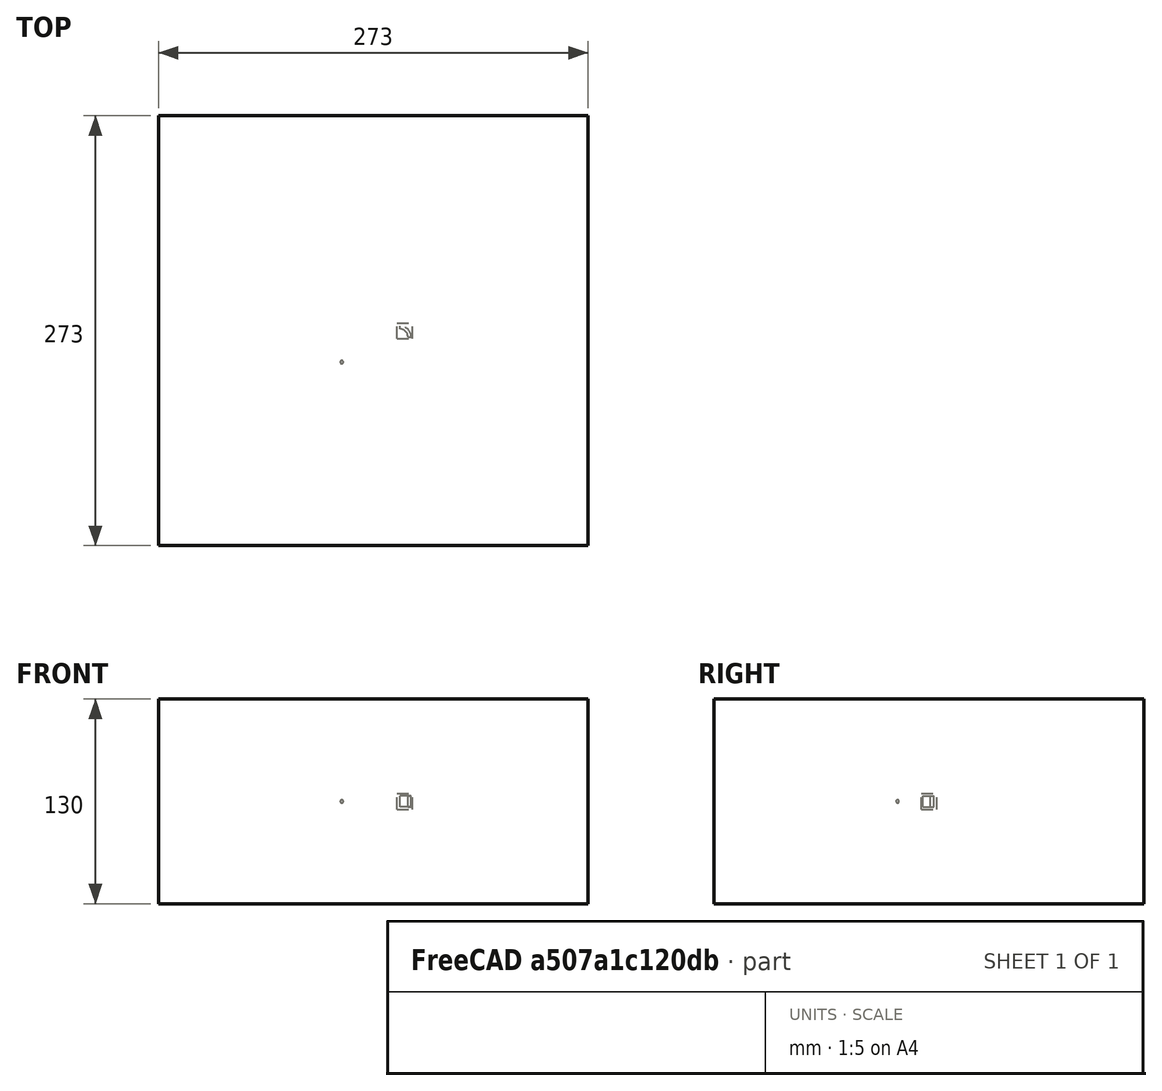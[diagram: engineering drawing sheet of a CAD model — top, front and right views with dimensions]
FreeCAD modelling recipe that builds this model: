
FCSTD DOCUMENT  (FreeCAD 0.21R33694 (Git))
Label: polarArray-of-Part-array-xformed
License: All rights reserved
LicenseURL: http://en.wikipedia.org/wiki/All_rights_reserved
objects: App::DocumentObjectGroupPython×1251, App::Part×5, Part::FeaturePython×4, Part::Sphere×1
note: 4 computed .brp shape members not serialized (recipe doc carries the construction recipe); baked Part::Feature solids carry a one-line shape summary decoded from their .brp

FEATURE [App::DocumentObjectGroupPython] HALFPI  # scripted group (container) (typed FeaturePython)
  name = HALFPI
  value = pi/2.
FEATURE [App::DocumentObjectGroupPython] PI  # scripted group (container) (typed FeaturePython)
  name = PI
  value = 1.*pi
FEATURE [App::DocumentObjectGroupPython] TWOPI  # scripted group (container) (typed FeaturePython)
  name = TWOPI
  value = 2.*pi
FEATURE [App::DocumentObjectGroupPython] Constants  # scripted group (container) (typed FeaturePython)
  Group = -> [HALFPI,PI,TWOPI]
FEATURE [App::DocumentObjectGroupPython] Variables  # scripted group (container) (typed FeaturePython)
FEATURE [App::DocumentObjectGroupPython] Quantities  # scripted group (container) (typed FeaturePython)
FEATURE [App::DocumentObjectGroupPython] Isotopes  # scripted group (container) (typed FeaturePython)
FEATURE [App::DocumentObjectGroupPython] Elements  # scripted group (container) (typed FeaturePython)
FEATURE [App::DocumentObjectGroupPython] Matrix  # scripted group (container) (typed FeaturePython)
FEATURE [App::DocumentObjectGroupPython] Surfaces  # scripted group (container) (typed FeaturePython)
FEATURE [App::DocumentObjectGroupPython] Opticals  # scripted group (container) (typed FeaturePython)
  Group = -> [Matrix,Surfaces]
FEATURE [App::DocumentObjectGroupPython] G4Isotopes  # scripted group (container) (typed FeaturePython)
FEATURE [App::DocumentObjectGroupPython] H_element  # scripted group (container) (typed FeaturePython)
  Z = 1
  atom_value = 1.008
  formula = H
  name = H_element
FEATURE [App::DocumentObjectGroupPython] He_element  # scripted group (container) (typed FeaturePython)
  Z = 2
  atom_value = 4.0026
  formula = He
  name = He_element
FEATURE [App::DocumentObjectGroupPython] Li_element  # scripted group (container) (typed FeaturePython)
  Z = 3
  atom_value = 6.94
  formula = Li
  name = Li_element
FEATURE [App::DocumentObjectGroupPython] Be_element  # scripted group (container) (typed FeaturePython)
  Z = 4
  atom_value = 9.01218
  formula = Be
  name = Be_element
FEATURE [App::DocumentObjectGroupPython] B_element  # scripted group (container) (typed FeaturePython)
  Z = 5
  atom_value = 10.81
  formula = B
  name = B_element
FEATURE [App::DocumentObjectGroupPython] C_element  # scripted group (container) (typed FeaturePython)
  Z = 6
  atom_value = 12.011
  formula = C
  name = C_element
FEATURE [App::DocumentObjectGroupPython] N_element  # scripted group (container) (typed FeaturePython)
  Z = 7
  atom_value = 14.007
  formula = N
  name = N_element
FEATURE [App::DocumentObjectGroupPython] O_element  # scripted group (container) (typed FeaturePython)
  Z = 8
  atom_value = 15.999
  formula = O
  name = O_element
FEATURE [App::DocumentObjectGroupPython] F_element  # scripted group (container) (typed FeaturePython)
  Z = 9
  atom_value = 18.9984
  formula = F
  name = F_element
FEATURE [App::DocumentObjectGroupPython] Ne_element  # scripted group (container) (typed FeaturePython)
  Z = 10
  atom_value = 20.1797
  formula = Ne
  name = Ne_element
FEATURE [App::DocumentObjectGroupPython] Na_element  # scripted group (container) (typed FeaturePython)
  Z = 11
  atom_value = 22.9898
  formula = Na
  name = Na_element
FEATURE [App::DocumentObjectGroupPython] Mg_element  # scripted group (container) (typed FeaturePython)
  Z = 12
  atom_value = 24.305
  formula = Mg
  name = Mg_element
FEATURE [App::DocumentObjectGroupPython] Al_element  # scripted group (container) (typed FeaturePython)
  Z = 13
  atom_value = 26.9815
  formula = Al
  name = Al_element
FEATURE [App::DocumentObjectGroupPython] Si_element  # scripted group (container) (typed FeaturePython)
  Z = 14
  atom_value = 28.085
  formula = Si
  name = Si_element
FEATURE [App::DocumentObjectGroupPython] P_element  # scripted group (container) (typed FeaturePython)
  Z = 15
  atom_value = 30.9738
  formula = P
  name = P_element
FEATURE [App::DocumentObjectGroupPython] S_element  # scripted group (container) (typed FeaturePython)
  Z = 16
  atom_value = 32.06
  formula = S
  name = S_element
FEATURE [App::DocumentObjectGroupPython] Cl_element  # scripted group (container) (typed FeaturePython)
  Z = 17
  atom_value = 35.45
  formula = Cl
  name = Cl_element
FEATURE [App::DocumentObjectGroupPython] Ar_element  # scripted group (container) (typed FeaturePython)
  Z = 18
  atom_value = 39.95
  formula = Ar
  name = Ar_element
FEATURE [App::DocumentObjectGroupPython] K_element  # scripted group (container) (typed FeaturePython)
  Z = 19
  atom_value = 39.0983
  formula = K
  name = K_element
FEATURE [App::DocumentObjectGroupPython] Ca_element  # scripted group (container) (typed FeaturePython)
  Z = 20
  atom_value = 40.078
  formula = Ca
  name = Ca_element
FEATURE [App::DocumentObjectGroupPython] Sc_element  # scripted group (container) (typed FeaturePython)
  Z = 21
  atom_value = 44.9559
  formula = Sc
  name = Sc_element
FEATURE [App::DocumentObjectGroupPython] Ti_element  # scripted group (container) (typed FeaturePython)
  Z = 22
  atom_value = 47.867
  formula = Ti
  name = Ti_element
FEATURE [App::DocumentObjectGroupPython] V_element  # scripted group (container) (typed FeaturePython)
  Z = 23
  atom_value = 50.9415
  formula = V
  name = V_element
FEATURE [App::DocumentObjectGroupPython] Cr_element  # scripted group (container) (typed FeaturePython)
  Z = 24
  atom_value = 51.9961
  formula = Cr
  name = Cr_element
FEATURE [App::DocumentObjectGroupPython] Mn_element  # scripted group (container) (typed FeaturePython)
  Z = 25
  atom_value = 54.938
  formula = Mn
  name = Mn_element
FEATURE [App::DocumentObjectGroupPython] Fe_element  # scripted group (container) (typed FeaturePython)
  Z = 26
  atom_value = 55.845
  formula = Fe
  name = Fe_element
FEATURE [App::DocumentObjectGroupPython] Co_element  # scripted group (container) (typed FeaturePython)
  Z = 27
  atom_value = 58.9332
  formula = Co
  name = Co_element
FEATURE [App::DocumentObjectGroupPython] Ni_element  # scripted group (container) (typed FeaturePython)
  Z = 28
  atom_value = 58.6934
  formula = Ni
  name = Ni_element
FEATURE [App::DocumentObjectGroupPython] Cu_element  # scripted group (container) (typed FeaturePython)
  Z = 29
  atom_value = 63.546
  formula = Cu
  name = Cu_element
FEATURE [App::DocumentObjectGroupPython] Zn_element  # scripted group (container) (typed FeaturePython)
  Z = 30
  atom_value = 65.38
  formula = Zn
  name = Zn_element
FEATURE [App::DocumentObjectGroupPython] Ga_element  # scripted group (container) (typed FeaturePython)
  Z = 31
  atom_value = 69.723
  formula = Ga
  name = Ga_element
FEATURE [App::DocumentObjectGroupPython] Ge_element  # scripted group (container) (typed FeaturePython)
  Z = 32
  atom_value = 72.63
  formula = Ge
  name = Ge_element
FEATURE [App::DocumentObjectGroupPython] As_element  # scripted group (container) (typed FeaturePython)
  Z = 33
  atom_value = 74.9216
  formula = As
  name = As_element
FEATURE [App::DocumentObjectGroupPython] Se_element  # scripted group (container) (typed FeaturePython)
  Z = 34
  atom_value = 78.971
  formula = Se
  name = Se_element
FEATURE [App::DocumentObjectGroupPython] Br_element  # scripted group (container) (typed FeaturePython)
  Z = 35
  atom_value = 79.904
  formula = Br
  name = Br_element
FEATURE [App::DocumentObjectGroupPython] Kr_element  # scripted group (container) (typed FeaturePython)
  Z = 36
  atom_value = 83.798
  formula = Kr
  name = Kr_element
FEATURE [App::DocumentObjectGroupPython] Rb_element  # scripted group (container) (typed FeaturePython)
  Z = 37
  atom_value = 85.4678
  formula = Rb
  name = Rb_element
FEATURE [App::DocumentObjectGroupPython] Sr_element  # scripted group (container) (typed FeaturePython)
  Z = 38
  atom_value = 87.62
  formula = Sr
  name = Sr_element
FEATURE [App::DocumentObjectGroupPython] Y_element  # scripted group (container) (typed FeaturePython)
  Z = 39
  atom_value = 88.9058
  formula = Y
  name = Y_element
FEATURE [App::DocumentObjectGroupPython] Zr_element  # scripted group (container) (typed FeaturePython)
  Z = 40
  atom_value = 91.224
  formula = Zr
  name = Zr_element
FEATURE [App::DocumentObjectGroupPython] Nb_element  # scripted group (container) (typed FeaturePython)
  Z = 41
  atom_value = 92.9064
  formula = Nb
  name = Nb_element
FEATURE [App::DocumentObjectGroupPython] Mo_element  # scripted group (container) (typed FeaturePython)
  Z = 42
  atom_value = 95.95
  formula = Mo
  name = Mo_element
FEATURE [App::DocumentObjectGroupPython] Tc_element  # scripted group (container) (typed FeaturePython)
  Z = 43
  atom_value = 97
  formula = Tc
  name = Tc_element
FEATURE [App::DocumentObjectGroupPython] Ru_element  # scripted group (container) (typed FeaturePython)
  Z = 44
  atom_value = 101.07
  formula = Ru
  name = Ru_element
FEATURE [App::DocumentObjectGroupPython] Rh_element  # scripted group (container) (typed FeaturePython)
  Z = 45
  atom_value = 102.905
  formula = Rh
  name = Rh_element
FEATURE [App::DocumentObjectGroupPython] Pd_element  # scripted group (container) (typed FeaturePython)
  Z = 46
  atom_value = 106.42
  formula = Pd
  name = Pd_element
FEATURE [App::DocumentObjectGroupPython] Ag_element  # scripted group (container) (typed FeaturePython)
  Z = 47
  atom_value = 107.868
  formula = Ag
  name = Ag_element
FEATURE [App::DocumentObjectGroupPython] Cd_element  # scripted group (container) (typed FeaturePython)
  Z = 48
  atom_value = 112.414
  formula = Cd
  name = Cd_element
FEATURE [App::DocumentObjectGroupPython] In_element  # scripted group (container) (typed FeaturePython)
  Z = 49
  atom_value = 114.818
  formula = In
  name = In_element
FEATURE [App::DocumentObjectGroupPython] Sn_element  # scripted group (container) (typed FeaturePython)
  Z = 50
  atom_value = 118.71
  formula = Sn
  name = Sn_element
FEATURE [App::DocumentObjectGroupPython] Sb_element  # scripted group (container) (typed FeaturePython)
  Z = 51
  atom_value = 121.76
  formula = Sb
  name = Sb_element
FEATURE [App::DocumentObjectGroupPython] Te_element  # scripted group (container) (typed FeaturePython)
  Z = 52
  atom_value = 127.6
  formula = Te
  name = Te_element
FEATURE [App::DocumentObjectGroupPython] I_element  # scripted group (container) (typed FeaturePython)
  Z = 53
  atom_value = 126.904
  formula = I
  name = I_element
FEATURE [App::DocumentObjectGroupPython] Xe_element  # scripted group (container) (typed FeaturePython)
  Z = 54
  atom_value = 131.293
  formula = Xe
  name = Xe_element
FEATURE [App::DocumentObjectGroupPython] Cs_element  # scripted group (container) (typed FeaturePython)
  Z = 55
  atom_value = 132.905
  formula = Cs
  name = Cs_element
FEATURE [App::DocumentObjectGroupPython] Ba_element  # scripted group (container) (typed FeaturePython)
  Z = 56
  atom_value = 137.327
  formula = Ba
  name = Ba_element
FEATURE [App::DocumentObjectGroupPython] La_element  # scripted group (container) (typed FeaturePython)
  Z = 57
  atom_value = 138.905
  formula = La
  name = La_element
FEATURE [App::DocumentObjectGroupPython] Ce_element  # scripted group (container) (typed FeaturePython)
  Z = 58
  atom_value = 140.116
  formula = Ce
  name = Ce_element
FEATURE [App::DocumentObjectGroupPython] Pr_element  # scripted group (container) (typed FeaturePython)
  Z = 59
  atom_value = 140.908
  formula = Pr
  name = Pr_element
FEATURE [App::DocumentObjectGroupPython] Nd_element  # scripted group (container) (typed FeaturePython)
  Z = 60
  atom_value = 144.242
  formula = Nd
  name = Nd_element
FEATURE [App::DocumentObjectGroupPython] Pm_element  # scripted group (container) (typed FeaturePython)
  Z = 61
  atom_value = 145
  formula = Pm
  name = Pm_element
FEATURE [App::DocumentObjectGroupPython] Sm_element  # scripted group (container) (typed FeaturePython)
  Z = 62
  atom_value = 150.36
  formula = Sm
  name = Sm_element
FEATURE [App::DocumentObjectGroupPython] Eu_element  # scripted group (container) (typed FeaturePython)
  Z = 63
  atom_value = 151.964
  formula = Eu
  name = Eu_element
FEATURE [App::DocumentObjectGroupPython] Gd_element  # scripted group (container) (typed FeaturePython)
  Z = 64
  atom_value = 157.25
  formula = Gd
  name = Gd_element
FEATURE [App::DocumentObjectGroupPython] Tb_element  # scripted group (container) (typed FeaturePython)
  Z = 65
  atom_value = 158.925
  formula = Tb
  name = Tb_element
FEATURE [App::DocumentObjectGroupPython] Dy_element  # scripted group (container) (typed FeaturePython)
  Z = 66
  atom_value = 162.5
  formula = Dy
  name = Dy_element
FEATURE [App::DocumentObjectGroupPython] Ho_element  # scripted group (container) (typed FeaturePython)
  Z = 67
  atom_value = 164.93
  formula = Ho
  name = Ho_element
FEATURE [App::DocumentObjectGroupPython] Er_element  # scripted group (container) (typed FeaturePython)
  Z = 68
  atom_value = 167.259
  formula = Er
  name = Er_element
FEATURE [App::DocumentObjectGroupPython] Tm_element  # scripted group (container) (typed FeaturePython)
  Z = 69
  atom_value = 168.934
  formula = Tm
  name = Tm_element
FEATURE [App::DocumentObjectGroupPython] Yb_element  # scripted group (container) (typed FeaturePython)
  Z = 70
  atom_value = 173.045
  formula = Yb
  name = Yb_element
FEATURE [App::DocumentObjectGroupPython] Lu_element  # scripted group (container) (typed FeaturePython)
  Z = 71
  atom_value = 174.967
  formula = Lu
  name = Lu_element
FEATURE [App::DocumentObjectGroupPython] Hf_element  # scripted group (container) (typed FeaturePython)
  Z = 72
  atom_value = 178.49
  formula = Hf
  name = Hf_element
FEATURE [App::DocumentObjectGroupPython] Ta_element  # scripted group (container) (typed FeaturePython)
  Z = 73
  atom_value = 180.948
  formula = Ta
  name = Ta_element
FEATURE [App::DocumentObjectGroupPython] W_element  # scripted group (container) (typed FeaturePython)
  Z = 74
  atom_value = 183.84
  formula = W
  name = W_element
FEATURE [App::DocumentObjectGroupPython] Re_element  # scripted group (container) (typed FeaturePython)
  Z = 75
  atom_value = 186.207
  formula = Re
  name = Re_element
FEATURE [App::DocumentObjectGroupPython] Os_element  # scripted group (container) (typed FeaturePython)
  Z = 76
  atom_value = 190.23
  formula = Os
  name = Os_element
FEATURE [App::DocumentObjectGroupPython] Ir_element  # scripted group (container) (typed FeaturePython)
  Z = 77
  atom_value = 192.217
  formula = Ir
  name = Ir_element
FEATURE [App::DocumentObjectGroupPython] Pt_element  # scripted group (container) (typed FeaturePython)
  Z = 78
  atom_value = 195.084
  formula = Pt
  name = Pt_element
FEATURE [App::DocumentObjectGroupPython] Au_element  # scripted group (container) (typed FeaturePython)
  Z = 79
  atom_value = 196.967
  formula = Au
  name = Au_element
FEATURE [App::DocumentObjectGroupPython] Hg_element  # scripted group (container) (typed FeaturePython)
  Z = 80
  atom_value = 200.592
  formula = Hg
  name = Hg_element
FEATURE [App::DocumentObjectGroupPython] Tl_element  # scripted group (container) (typed FeaturePython)
  Z = 81
  atom_value = 204.38
  formula = Tl
  name = Tl_element
FEATURE [App::DocumentObjectGroupPython] Pb_element  # scripted group (container) (typed FeaturePython)
  Z = 82
  atom_value = 207.2
  formula = Pb
  name = Pb_element
FEATURE [App::DocumentObjectGroupPython] Bi_element  # scripted group (container) (typed FeaturePython)
  Z = 83
  atom_value = 208.98
  formula = Bi
  name = Bi_element
FEATURE [App::DocumentObjectGroupPython] Po_element  # scripted group (container) (typed FeaturePython)
  Z = 84
  atom_value = 209
  formula = Po
  name = Po_element
FEATURE [App::DocumentObjectGroupPython] At_element  # scripted group (container) (typed FeaturePython)
  Z = 85
  atom_value = 210
  formula = At
  name = At_element
FEATURE [App::DocumentObjectGroupPython] Rn_element  # scripted group (container) (typed FeaturePython)
  Z = 86
  atom_value = 222
  formula = Rn
  name = Rn_element
FEATURE [App::DocumentObjectGroupPython] Fr_element  # scripted group (container) (typed FeaturePython)
  Z = 87
  atom_value = 223
  formula = Fr
  name = Fr_element
FEATURE [App::DocumentObjectGroupPython] Ra_element  # scripted group (container) (typed FeaturePython)
  Z = 88
  atom_value = 226
  formula = Ra
  name = Ra_element
FEATURE [App::DocumentObjectGroupPython] Ac_element  # scripted group (container) (typed FeaturePython)
  Z = 89
  atom_value = 227
  formula = Ac
  name = Ac_element
FEATURE [App::DocumentObjectGroupPython] Th_element  # scripted group (container) (typed FeaturePython)
  Z = 90
  atom_value = 232.038
  formula = Th
  name = Th_element
FEATURE [App::DocumentObjectGroupPython] Pa_element  # scripted group (container) (typed FeaturePython)
  Z = 91
  atom_value = 231.036
  formula = Pa
  name = Pa_element
FEATURE [App::DocumentObjectGroupPython] U_element  # scripted group (container) (typed FeaturePython)
  Z = 92
  atom_value = 238.029
  formula = U
  name = U_element
FEATURE [App::DocumentObjectGroupPython] Np_element  # scripted group (container) (typed FeaturePython)
  Z = 93
  atom_value = 237
  formula = Np
  name = Np_element
FEATURE [App::DocumentObjectGroupPython] Pu_element  # scripted group (container) (typed FeaturePython)
  Z = 94
  atom_value = 244
  formula = Pu
  name = Pu_element
FEATURE [App::DocumentObjectGroupPython] Am_element  # scripted group (container) (typed FeaturePython)
  Z = 95
  atom_value = 243
  formula = Am
  name = Am_element
FEATURE [App::DocumentObjectGroupPython] Cm_element  # scripted group (container) (typed FeaturePython)
  Z = 96
  atom_value = 247
  formula = Cm
  name = Cm_element
FEATURE [App::DocumentObjectGroupPython] Bk_element  # scripted group (container) (typed FeaturePython)
  Z = 97
  atom_value = 247
  formula = Bk
  name = Bk_element
FEATURE [App::DocumentObjectGroupPython] Cf_element  # scripted group (container) (typed FeaturePython)
  Z = 98
  atom_value = 251
  formula = Cf
  name = Cf_element
FEATURE [App::DocumentObjectGroupPython] G4Elements  # scripted group (container) (typed FeaturePython)
  Group = -> [H_element,He_element,Li_element,Be_element,B_element,C_element,N_element,O_element,F_element,Ne_element,Na_element,Mg_element,Al_element,Si_element,P_element,S_element,Cl_element,Ar_element,K_element,Ca_element,Sc_element,Ti_element,V_element,Cr_element,Mn_element,Fe_element,Co_element,Ni_element,Cu_element,Zn_element,Ga_element,Ge_element,As_element,Se_element,Br_element,Kr_element,Rb_element,+61 more]
FEATURE [App::DocumentObjectGroupPython] H_element001  label="H_element : 0.101"  # scripted group (container) (typed FeaturePython)
  n = 0.101327
FEATURE [App::DocumentObjectGroupPython] C_element001  label="C_element : 0.775"  # scripted group (container) (typed FeaturePython)
  n = 0.7755
FEATURE [App::DocumentObjectGroupPython] N_element001  label="N_element : 0.035"  # scripted group (container) (typed FeaturePython)
  n = 0.035057
FEATURE [App::DocumentObjectGroupPython] O_element001  label="O_element : 0.052"  # scripted group (container) (typed FeaturePython)
  n = 0.0523159
FEATURE [App::DocumentObjectGroupPython] F_element001  label="F_element : 0.017"  # scripted group (container) (typed FeaturePython)
  n = 0.017422
FEATURE [App::DocumentObjectGroupPython] Ca_element001  label="Ca_element : 0.018"  # scripted group (container) (typed FeaturePython)
  n = 0.018378
FEATURE [App::DocumentObjectGroupPython] G4_A_150_TISSUE  label="G4_A-150_TISSUE"  # scripted group (container) (typed FeaturePython)
  Dunit = g/cm3
  Dvalue = 1.127
  Group = -> [H_element001,C_element001,N_element001,O_element001,F_element001,Ca_element001]
  conduct = 2
  density = 1
  expand = 3
  formula = G4_A-150_TISSUE
  name = G4_A-150_TISSUE
  specific = 4
FEATURE [App::DocumentObjectGroupPython] C_element002  label="C_element : 3"  # scripted group (container) (typed FeaturePython)
  n = 3
  ref = C_element
FEATURE [App::DocumentObjectGroupPython] H_element002  label="H_element : 6"  # scripted group (container) (typed FeaturePython)
  n = 6
  ref = H_element
FEATURE [App::DocumentObjectGroupPython] O_element002  label="O_element : 1"  # scripted group (container) (typed FeaturePython)
  n = 1
  ref = O_element
FEATURE [App::DocumentObjectGroupPython] G4_ACETONE  # scripted group (container) (typed FeaturePython)
  Dunit = g/cm3
  Dvalue = 0.7899
  Group = -> [C_element002,H_element002,O_element002]
  conduct = 2
  density = 1
  expand = 3
  formula = G4_ACETONE
  name = G4_ACETONE
  specific = 4
FEATURE [App::DocumentObjectGroupPython] C_element003  label="C_element : 2"  # scripted group (container) (typed FeaturePython)
  n = 2
  ref = C_element
FEATURE [App::DocumentObjectGroupPython] H_element003  label="H_element : 2"  # scripted group (container) (typed FeaturePython)
  n = 2
  ref = H_element
FEATURE [App::DocumentObjectGroupPython] G4_ACETYLENE  # scripted group (container) (typed FeaturePython)
  Dunit = g/cm3
  Dvalue = 0.0010967
  Group = -> [C_element003,H_element003]
  conduct = 2
  density = 1
  expand = 3
  formula = G4_ACETYLENE
  name = G4_ACETYLENE
  specific = 4
FEATURE [App::DocumentObjectGroupPython] C_element004  label="C_element : 5"  # scripted group (container) (typed FeaturePython)
  n = 5
  ref = C_element
FEATURE [App::DocumentObjectGroupPython] H_element004  label="H_element : 5"  # scripted group (container) (typed FeaturePython)
  n = 5
  ref = H_element
FEATURE [App::DocumentObjectGroupPython] N_element002  label="N_element : 5"  # scripted group (container) (typed FeaturePython)
  n = 5
  ref = N_element
FEATURE [App::DocumentObjectGroupPython] G4_ADENINE  # scripted group (container) (typed FeaturePython)
  Dunit = g/cm3
  Dvalue = 1.6
  Group = -> [C_element004,H_element004,N_element002]
  conduct = 2
  density = 1
  expand = 3
  formula = G4_ADENINE
  name = G4_ADENINE
  specific = 4
FEATURE [App::DocumentObjectGroupPython] H_element005  label="H_element : 0.114"  # scripted group (container) (typed FeaturePython)
  n = 0.114
FEATURE [App::DocumentObjectGroupPython] C_element005  label="C_element : 0.598"  # scripted group (container) (typed FeaturePython)
  n = 0.598
FEATURE [App::DocumentObjectGroupPython] N_element003  label="N_element : 0.007"  # scripted group (container) (typed FeaturePython)
  n = 0.007
FEATURE [App::DocumentObjectGroupPython] O_element003  label="O_element : 0.278"  # scripted group (container) (typed FeaturePython)
  n = 0.278
FEATURE [App::DocumentObjectGroupPython] Na_element001  label="Na_element : 0.001"  # scripted group (container) (typed FeaturePython)
  n = 0.001
FEATURE [App::DocumentObjectGroupPython] S_element001  label="S_element : 0.001"  # scripted group (container) (typed FeaturePython)
  n = 0.001
FEATURE [App::DocumentObjectGroupPython] Cl_element001  label="Cl_element : 0.001"  # scripted group (container) (typed FeaturePython)
  n = 0.001
FEATURE [App::DocumentObjectGroupPython] G4_ADIPOSE_TISSUE_ICRP  # scripted group (container) (typed FeaturePython)
  Dunit = g/cm3
  Dvalue = 0.95
  Group = -> [H_element005,C_element005,N_element003,O_element003,Na_element001,S_element001,Cl_element001]
  conduct = 2
  density = 1
  expand = 3
  formula = G4_ADIPOSE_TISSUE_ICRP
  name = G4_ADIPOSE_TISSUE_ICRP
  specific = 4
FEATURE [App::DocumentObjectGroupPython] C_element006  label="C_element : 0.000"  # scripted group (container) (typed FeaturePython)
  n = 0.000124
FEATURE [App::DocumentObjectGroupPython] N_element004  label="N_element : 0.755"  # scripted group (container) (typed FeaturePython)
  n = 0.755268
FEATURE [App::DocumentObjectGroupPython] O_element004  label="O_element : 0.232"  # scripted group (container) (typed FeaturePython)
  n = 0.231781
FEATURE [App::DocumentObjectGroupPython] Ar_element001  label="Ar_element : 0.013"  # scripted group (container) (typed FeaturePython)
  n = 0.012827
FEATURE [App::DocumentObjectGroupPython] G4_AIR  # scripted group (container) (typed FeaturePython)
  Dunit = g/cm3
  Dvalue = 0.00120479
  Group = -> [C_element006,N_element004,O_element004,Ar_element001]
  conduct = 2
  density = 1
  expand = 3
  formula = G4_AIR
  name = G4_AIR
  specific = 4
FEATURE [App::DocumentObjectGroupPython] C_element007  label="C_element : 006"  # scripted group (container) (typed FeaturePython)
  n = 3
  ref = C_element
FEATURE [App::DocumentObjectGroupPython] H_element006  label="H_element : 7"  # scripted group (container) (typed FeaturePython)
  n = 7
  ref = H_element
FEATURE [App::DocumentObjectGroupPython] N_element005  label="N_element : 1"  # scripted group (container) (typed FeaturePython)
  n = 1
  ref = N_element
FEATURE [App::DocumentObjectGroupPython] O_element005  label="O_element : 2"  # scripted group (container) (typed FeaturePython)
  n = 2
  ref = O_element
FEATURE [App::DocumentObjectGroupPython] G4_ALANINE  # scripted group (container) (typed FeaturePython)
  Dunit = g/cm3
  Dvalue = 1.42
  Group = -> [C_element007,H_element006,N_element005,O_element005]
  conduct = 2
  density = 1
  expand = 3
  formula = G4_ALANINE
  name = G4_ALANINE
  specific = 4
FEATURE [App::DocumentObjectGroupPython] Al_element001  label="Al_element : 2"  # scripted group (container) (typed FeaturePython)
  n = 2
  ref = Al_element
FEATURE [App::DocumentObjectGroupPython] O_element006  label="O_element : 3"  # scripted group (container) (typed FeaturePython)
  n = 3
  ref = O_element
FEATURE [App::DocumentObjectGroupPython] G4_ALUMINUM_OXIDE  # scripted group (container) (typed FeaturePython)
  Dunit = g/cm3
  Dvalue = 3.97
  Group = -> [Al_element001,O_element006]
  conduct = 2
  density = 1
  expand = 3
  formula = G4_ALUMINUM_OXIDE
  name = G4_ALUMINUM_OXIDE
  specific = 4
FEATURE [App::DocumentObjectGroupPython] H_element007  label="H_element : 0.106"  # scripted group (container) (typed FeaturePython)
  n = 0.10593
FEATURE [App::DocumentObjectGroupPython] C_element008  label="C_element : 0.789"  # scripted group (container) (typed FeaturePython)
  n = 0.788974
FEATURE [App::DocumentObjectGroupPython] O_element007  label="O_element : 0.105"  # scripted group (container) (typed FeaturePython)
  n = 0.105096
FEATURE [App::DocumentObjectGroupPython] G4_AMBER  # scripted group (container) (typed FeaturePython)
  Dunit = g/cm3
  Dvalue = 1.1
  Group = -> [H_element007,C_element008,O_element007]
  conduct = 2
  density = 1
  expand = 3
  formula = G4_AMBER
  name = G4_AMBER
  specific = 4
FEATURE [App::DocumentObjectGroupPython] N_element006  label="N_element : 006"  # scripted group (container) (typed FeaturePython)
  n = 1
  ref = N_element
FEATURE [App::DocumentObjectGroupPython] H_element008  label="H_element : 3"  # scripted group (container) (typed FeaturePython)
  n = 3
  ref = H_element
FEATURE [App::DocumentObjectGroupPython] G4_AMMONIA  # scripted group (container) (typed FeaturePython)
  Dunit = g/cm3
  Dvalue = 0.000826019
  Group = -> [N_element006,H_element008]
  conduct = 2
  density = 1
  expand = 3
  formula = G4_AMMONIA
  name = G4_AMMONIA
  specific = 4
FEATURE [App::DocumentObjectGroupPython] C_element009  label="C_element : 6"  # scripted group (container) (typed FeaturePython)
  n = 6
  ref = C_element
FEATURE [App::DocumentObjectGroupPython] H_element009  label="H_element : 008"  # scripted group (container) (typed FeaturePython)
  n = 7
  ref = H_element
FEATURE [App::DocumentObjectGroupPython] N_element007  label="N_element : 007"  # scripted group (container) (typed FeaturePython)
  n = 1
  ref = N_element
FEATURE [App::DocumentObjectGroupPython] G4_ANILINE  # scripted group (container) (typed FeaturePython)
  Dunit = g/cm3
  Dvalue = 1.0235
  Group = -> [C_element009,H_element009,N_element007]
  conduct = 2
  density = 1
  expand = 3
  formula = G4_ANILINE
  name = G4_ANILINE
  specific = 4
FEATURE [App::DocumentObjectGroupPython] C_element010  label="C_element : 14"  # scripted group (container) (typed FeaturePython)
  n = 14
  ref = C_element
FEATURE [App::DocumentObjectGroupPython] H_element010  label="H_element : 10"  # scripted group (container) (typed FeaturePython)
  n = 10
  ref = H_element
FEATURE [App::DocumentObjectGroupPython] G4_ANTHRACENE  # scripted group (container) (typed FeaturePython)
  Dunit = g/cm3
  Dvalue = 1.283
  Group = -> [C_element010,H_element010]
  conduct = 2
  density = 1
  expand = 3
  formula = G4_ANTHRACENE
  name = G4_ANTHRACENE
  specific = 4
FEATURE [App::DocumentObjectGroupPython] H_element011  label="H_element : 0.065"  # scripted group (container) (typed FeaturePython)
  n = 0.0654709
FEATURE [App::DocumentObjectGroupPython] C_element011  label="C_element : 0.537"  # scripted group (container) (typed FeaturePython)
  n = 0.536944
FEATURE [App::DocumentObjectGroupPython] N_element008  label="N_element : 0.021"  # scripted group (container) (typed FeaturePython)
  n = 0.0215
FEATURE [App::DocumentObjectGroupPython] O_element008  label="O_element : 0.032"  # scripted group (container) (typed FeaturePython)
  n = 0.032085
FEATURE [App::DocumentObjectGroupPython] F_element002  label="F_element : 0.167"  # scripted group (container) (typed FeaturePython)
  n = 0.167411
FEATURE [App::DocumentObjectGroupPython] Ca_element002  label="Ca_element : 0.177"  # scripted group (container) (typed FeaturePython)
  n = 0.176589
FEATURE [App::DocumentObjectGroupPython] G4_B_100_BONE  label="G4_B-100_BONE"  # scripted group (container) (typed FeaturePython)
  Dunit = g/cm3
  Dvalue = 1.45
  Group = -> [H_element011,C_element011,N_element008,O_element008,F_element002,Ca_element002]
  conduct = 2
  density = 1
  expand = 3
  formula = G4_B-100_BONE
  name = G4_B-100_BONE
  specific = 4
FEATURE [App::DocumentObjectGroupPython] H_element012  label="H_element : 0.057"  # scripted group (container) (typed FeaturePython)
  n = 0.057441
FEATURE [App::DocumentObjectGroupPython] C_element012  label="C_element : 0.790"  # scripted group (container) (typed FeaturePython)
  n = 0.774591
FEATURE [App::DocumentObjectGroupPython] O_element009  label="O_element : 0.168"  # scripted group (container) (typed FeaturePython)
  n = 0.167968
FEATURE [App::DocumentObjectGroupPython] G4_BAKELITE  # scripted group (container) (typed FeaturePython)
  Dunit = g/cm3
  Dvalue = 1.25
  Group = -> [H_element012,C_element012,O_element009]
  conduct = 2
  density = 1
  expand = 3
  formula = G4_BAKELITE
  name = G4_BAKELITE
  specific = 4
FEATURE [App::DocumentObjectGroupPython] Ba_element001  label="Ba_element : 1"  # scripted group (container) (typed FeaturePython)
  n = 1
  ref = Ba_element
FEATURE [App::DocumentObjectGroupPython] F_element003  label="F_element : 2"  # scripted group (container) (typed FeaturePython)
  n = 2
  ref = F_element
FEATURE [App::DocumentObjectGroupPython] G4_BARIUM_FLUORIDE  # scripted group (container) (typed FeaturePython)
  Dunit = g/cm3
  Dvalue = 4.89
  Group = -> [Ba_element001,F_element003]
  conduct = 2
  density = 1
  expand = 3
  formula = G4_BARIUM_FLUORIDE
  name = G4_BARIUM_FLUORIDE
  specific = 4
FEATURE [App::DocumentObjectGroupPython] Ba_element002  label="Ba_element : 002"  # scripted group (container) (typed FeaturePython)
  n = 1
  ref = Ba_element
FEATURE [App::DocumentObjectGroupPython] S_element002  label="S_element : 1"  # scripted group (container) (typed FeaturePython)
  n = 1
  ref = S_element
FEATURE [App::DocumentObjectGroupPython] O_element010  label="O_element : 4"  # scripted group (container) (typed FeaturePython)
  n = 4
  ref = O_element
FEATURE [App::DocumentObjectGroupPython] G4_BARIUM_SULFATE  # scripted group (container) (typed FeaturePython)
  Dunit = g/cm3
  Dvalue = 4.5
  Group = -> [Ba_element002,S_element002,O_element010]
  conduct = 2
  density = 1
  expand = 3
  formula = G4_BARIUM_SULFATE
  name = G4_BARIUM_SULFATE
  specific = 4
FEATURE [App::DocumentObjectGroupPython] C_element013  label="C_element : 007"  # scripted group (container) (typed FeaturePython)
  n = 6
  ref = C_element
FEATURE [App::DocumentObjectGroupPython] H_element013  label="H_element : 009"  # scripted group (container) (typed FeaturePython)
  n = 6
  ref = H_element
FEATURE [App::DocumentObjectGroupPython] G4_BENZENE  # scripted group (container) (typed FeaturePython)
  Dunit = g/cm3
  Dvalue = 0.87865
  Group = -> [C_element013,H_element013]
  conduct = 2
  density = 1
  expand = 3
  formula = G4_BENZENE
  name = G4_BENZENE
  specific = 4
FEATURE [App::DocumentObjectGroupPython] Be_element001  label="Be_element : 1"  # scripted group (container) (typed FeaturePython)
  n = 1
  ref = Be_element
FEATURE [App::DocumentObjectGroupPython] O_element011  label="O_element : 005"  # scripted group (container) (typed FeaturePython)
  n = 1
  ref = O_element
FEATURE [App::DocumentObjectGroupPython] G4_BERYLLIUM_OXIDE  # scripted group (container) (typed FeaturePython)
  Dunit = g/cm3
  Dvalue = 3.01
  Group = -> [Be_element001,O_element011]
  conduct = 2
  density = 1
  expand = 3
  formula = G4_BERYLLIUM_OXIDE
  name = G4_BERYLLIUM_OXIDE
  specific = 4
FEATURE [App::DocumentObjectGroupPython] Bi_element001  label="Bi_element : 4"  # scripted group (container) (typed FeaturePython)
  n = 4
  ref = Bi_element
FEATURE [App::DocumentObjectGroupPython] Ge_element001  label="Ge_element : 3"  # scripted group (container) (typed FeaturePython)
  n = 3
  ref = Ge_element
FEATURE [App::DocumentObjectGroupPython] O_element012  label="O_element : 12"  # scripted group (container) (typed FeaturePython)
  n = 12
  ref = O_element
FEATURE [App::DocumentObjectGroupPython] G4_BGO  # scripted group (container) (typed FeaturePython)
  Dunit = g/cm3
  Dvalue = 7.13
  Group = -> [Bi_element001,Ge_element001,O_element012]
  conduct = 2
  density = 1
  expand = 3
  formula = G4_BGO
  name = G4_BGO
  specific = 4
FEATURE [App::DocumentObjectGroupPython] H_element014  label="H_element : 0.102"  # scripted group (container) (typed FeaturePython)
  n = 0.102
FEATURE [App::DocumentObjectGroupPython] C_element014  label="C_element : 0.110"  # scripted group (container) (typed FeaturePython)
  n = 0.11
FEATURE [App::DocumentObjectGroupPython] N_element009  label="N_element : 0.033"  # scripted group (container) (typed FeaturePython)
  n = 0.033
FEATURE [App::DocumentObjectGroupPython] O_element013  label="O_element : 0.745"  # scripted group (container) (typed FeaturePython)
  n = 0.745
FEATURE [App::DocumentObjectGroupPython] Na_element002  label="Na_element : 0.002"  # scripted group (container) (typed FeaturePython)
  n = 0.001
FEATURE [App::DocumentObjectGroupPython] P_element001  label="P_element : 0.001"  # scripted group (container) (typed FeaturePython)
  n = 0.001
FEATURE [App::DocumentObjectGroupPython] S_element003  label="S_element : 0.002"  # scripted group (container) (typed FeaturePython)
  n = 0.002
FEATURE [App::DocumentObjectGroupPython] Cl_element002  label="Cl_element : 0.003"  # scripted group (container) (typed FeaturePython)
  n = 0.003
FEATURE [App::DocumentObjectGroupPython] K_element001  label="K_element : 0.002"  # scripted group (container) (typed FeaturePython)
  n = 0.002
FEATURE [App::DocumentObjectGroupPython] Fe_element001  label="Fe_element : 0.001"  # scripted group (container) (typed FeaturePython)
  n = 0.001
FEATURE [App::DocumentObjectGroupPython] G4_BLOOD_ICRP  # scripted group (container) (typed FeaturePython)
  Dunit = g/cm3
  Dvalue = 1.06
  Group = -> [H_element014,C_element014,N_element009,O_element013,Na_element002,P_element001,S_element003,Cl_element002,K_element001,Fe_element001]
  conduct = 2
  density = 1
  expand = 3
  formula = G4_BLOOD_ICRP
  name = G4_BLOOD_ICRP
  specific = 4
FEATURE [App::DocumentObjectGroupPython] H_element015  label="H_element : 0.064"  # scripted group (container) (typed FeaturePython)
  n = 0.064
FEATURE [App::DocumentObjectGroupPython] C_element015  label="C_element : 0.278"  # scripted group (container) (typed FeaturePython)
  n = 0.278
FEATURE [App::DocumentObjectGroupPython] N_element010  label="N_element : 0.027"  # scripted group (container) (typed FeaturePython)
  n = 0.027
FEATURE [App::DocumentObjectGroupPython] O_element014  label="O_element : 0.410"  # scripted group (container) (typed FeaturePython)
  n = 0.41
FEATURE [App::DocumentObjectGroupPython] Mg_element001  label="Mg_element : 0.002"  # scripted group (container) (typed FeaturePython)
  n = 0.002
FEATURE [App::DocumentObjectGroupPython] P_element002  label="P_element : 0.070"  # scripted group (container) (typed FeaturePython)
  n = 0.07
FEATURE [App::DocumentObjectGroupPython] S_element004  label="S_element : 0.003"  # scripted group (container) (typed FeaturePython)
  n = 0.002
FEATURE [App::DocumentObjectGroupPython] Ca_element003  label="Ca_element : 0.147"  # scripted group (container) (typed FeaturePython)
  n = 0.147
FEATURE [App::DocumentObjectGroupPython] G4_BONE_COMPACT_ICRU  # scripted group (container) (typed FeaturePython)
  Dunit = g/cm3
  Dvalue = 1.85
  Group = -> [H_element015,C_element015,N_element010,O_element014,Mg_element001,P_element002,S_element004,Ca_element003]
  conduct = 2
  density = 1
  expand = 3
  formula = G4_BONE_COMPACT_ICRU
  name = G4_BONE_COMPACT_ICRU
  specific = 4
FEATURE [App::DocumentObjectGroupPython] H_element016  label="H_element : 0.034"  # scripted group (container) (typed FeaturePython)
  n = 0.034
FEATURE [App::DocumentObjectGroupPython] C_element016  label="C_element : 0.155"  # scripted group (container) (typed FeaturePython)
  n = 0.155
FEATURE [App::DocumentObjectGroupPython] N_element011  label="N_element : 0.042"  # scripted group (container) (typed FeaturePython)
  n = 0.042
FEATURE [App::DocumentObjectGroupPython] O_element015  label="O_element : 0.435"  # scripted group (container) (typed FeaturePython)
  n = 0.435
FEATURE [App::DocumentObjectGroupPython] Na_element003  label="Na_element : 0.003"  # scripted group (container) (typed FeaturePython)
  n = 0.001
FEATURE [App::DocumentObjectGroupPython] Mg_element002  label="Mg_element : 0.003"  # scripted group (container) (typed FeaturePython)
  n = 0.002
FEATURE [App::DocumentObjectGroupPython] P_element003  label="P_element : 0.103"  # scripted group (container) (typed FeaturePython)
  n = 0.103
FEATURE [App::DocumentObjectGroupPython] S_element005  label="S_element : 0.004"  # scripted group (container) (typed FeaturePython)
  n = 0.003
FEATURE [App::DocumentObjectGroupPython] Ca_element004  label="Ca_element : 0.225"  # scripted group (container) (typed FeaturePython)
  n = 0.225
FEATURE [App::DocumentObjectGroupPython] G4_BONE_CORTICAL_ICRP  # scripted group (container) (typed FeaturePython)
  Dunit = g/cm3
  Dvalue = 1.92
  Group = -> [H_element016,C_element016,N_element011,O_element015,Na_element003,Mg_element002,P_element003,S_element005,Ca_element004]
  conduct = 2
  density = 1
  expand = 3
  formula = G4_BONE_CORTICAL_ICRP
  name = G4_BONE_CORTICAL_ICRP
  specific = 4
FEATURE [App::DocumentObjectGroupPython] B_element001  label="B_element : 4"  # scripted group (container) (typed FeaturePython)
  n = 4
  ref = B_element
FEATURE [App::DocumentObjectGroupPython] C_element017  label="C_element : 1"  # scripted group (container) (typed FeaturePython)
  n = 1
  ref = C_element
FEATURE [App::DocumentObjectGroupPython] G4_BORON_CARBIDE  # scripted group (container) (typed FeaturePython)
  Dunit = g/cm3
  Dvalue = 2.52
  Group = -> [B_element001,C_element017]
  conduct = 2
  density = 1
  expand = 3
  formula = G4_BORON_CARBIDE
  name = G4_BORON_CARBIDE
  specific = 4
FEATURE [App::DocumentObjectGroupPython] B_element002  label="B_element : 2"  # scripted group (container) (typed FeaturePython)
  n = 2
  ref = B_element
FEATURE [App::DocumentObjectGroupPython] O_element016  label="O_element : 006"  # scripted group (container) (typed FeaturePython)
  n = 3
  ref = O_element
FEATURE [App::DocumentObjectGroupPython] G4_BORON_OXIDE  # scripted group (container) (typed FeaturePython)
  Dunit = g/cm3
  Dvalue = 1.812
  Group = -> [B_element002,O_element016]
  conduct = 2
  density = 1
  expand = 3
  formula = G4_BORON_OXIDE
  name = G4_BORON_OXIDE
  specific = 4
FEATURE [App::DocumentObjectGroupPython] H_element017  label="H_element : 0.107"  # scripted group (container) (typed FeaturePython)
  n = 0.107
FEATURE [App::DocumentObjectGroupPython] C_element018  label="C_element : 0.145"  # scripted group (container) (typed FeaturePython)
  n = 0.145
FEATURE [App::DocumentObjectGroupPython] N_element012  label="N_element : 0.022"  # scripted group (container) (typed FeaturePython)
  n = 0.022
FEATURE [App::DocumentObjectGroupPython] O_element017  label="O_element : 0.712"  # scripted group (container) (typed FeaturePython)
  n = 0.712
FEATURE [App::DocumentObjectGroupPython] Na_element004  label="Na_element : 0.004"  # scripted group (container) (typed FeaturePython)
  n = 0.002
FEATURE [App::DocumentObjectGroupPython] P_element004  label="P_element : 0.004"  # scripted group (container) (typed FeaturePython)
  n = 0.004
FEATURE [App::DocumentObjectGroupPython] S_element006  label="S_element : 0.005"  # scripted group (container) (typed FeaturePython)
  n = 0.002
FEATURE [App::DocumentObjectGroupPython] Cl_element003  label="Cl_element : 0.004"  # scripted group (container) (typed FeaturePython)
  n = 0.003
FEATURE [App::DocumentObjectGroupPython] K_element002  label="K_element : 0.003"  # scripted group (container) (typed FeaturePython)
  n = 0.003
FEATURE [App::DocumentObjectGroupPython] G4_BRAIN_ICRP  # scripted group (container) (typed FeaturePython)
  Dunit = g/cm3
  Dvalue = 1.04
  Group = -> [H_element017,C_element018,N_element012,O_element017,Na_element004,P_element004,S_element006,Cl_element003,K_element002]
  conduct = 2
  density = 1
  expand = 3
  formula = G4_BRAIN_ICRP
  name = G4_BRAIN_ICRP
  specific = 4
FEATURE [App::DocumentObjectGroupPython] C_element019  label="C_element : 4"  # scripted group (container) (typed FeaturePython)
  n = 4
  ref = C_element
FEATURE [App::DocumentObjectGroupPython] H_element018  label="H_element : 010"  # scripted group (container) (typed FeaturePython)
  n = 10
  ref = H_element
FEATURE [App::DocumentObjectGroupPython] G4_BUTANE  # scripted group (container) (typed FeaturePython)
  Dunit = g/cm3
  Dvalue = 0.00249343
  Group = -> [C_element019,H_element018]
  conduct = 2
  density = 1
  expand = 3
  formula = G4_BUTANE
  name = G4_BUTANE
  specific = 4
FEATURE [App::DocumentObjectGroupPython] C_element020  label="C_element : 008"  # scripted group (container) (typed FeaturePython)
  n = 4
  ref = C_element
FEATURE [App::DocumentObjectGroupPython] H_element019  label="H_element : 011"  # scripted group (container) (typed FeaturePython)
  n = 10
  ref = H_element
FEATURE [App::DocumentObjectGroupPython] O_element018  label="O_element : 007"  # scripted group (container) (typed FeaturePython)
  n = 1
  ref = O_element
FEATURE [App::DocumentObjectGroupPython] G4_N_BUTYL_ALCOHOL  label="G4_N-BUTYL_ALCOHOL"  # scripted group (container) (typed FeaturePython)
  Dunit = g/cm3
  Dvalue = 0.8098
  Group = -> [C_element020,H_element019,O_element018]
  conduct = 2
  density = 1
  expand = 3
  formula = G4_N-BUTYL_ALCOHOL
  name = G4_N-BUTYL_ALCOHOL
  specific = 4
FEATURE [App::DocumentObjectGroupPython] H_element020  label="H_element : 0.025"  # scripted group (container) (typed FeaturePython)
  n = 0.02468
FEATURE [App::DocumentObjectGroupPython] C_element021  label="C_element : 0.502"  # scripted group (container) (typed FeaturePython)
  n = 0.501611
FEATURE [App::DocumentObjectGroupPython] O_element019  label="O_element : 0.005"  # scripted group (container) (typed FeaturePython)
  n = 0.004527
FEATURE [App::DocumentObjectGroupPython] F_element004  label="F_element : 0.465"  # scripted group (container) (typed FeaturePython)
  n = 0.465209
FEATURE [App::DocumentObjectGroupPython] Si_element001  label="Si_element : 0.004"  # scripted group (container) (typed FeaturePython)
  n = 0.003973
FEATURE [App::DocumentObjectGroupPython] G4_C_552  label="G4_C-552"  # scripted group (container) (typed FeaturePython)
  Dunit = g/cm3
  Dvalue = 1.76
  Group = -> [H_element020,C_element021,O_element019,F_element004,Si_element001]
  conduct = 2
  density = 1
  expand = 3
  formula = G4_C-552
  name = G4_C-552
  specific = 4
FEATURE [App::DocumentObjectGroupPython] Cd_element001  label="Cd_element : 1"  # scripted group (container) (typed FeaturePython)
  n = 1
  ref = Cd_element
FEATURE [App::DocumentObjectGroupPython] Te_element001  label="Te_element : 1"  # scripted group (container) (typed FeaturePython)
  n = 1
  ref = Te_element
FEATURE [App::DocumentObjectGroupPython] G4_CADMIUM_TELLURIDE  # scripted group (container) (typed FeaturePython)
  Dunit = g/cm3
  Dvalue = 6.2
  Group = -> [Cd_element001,Te_element001]
  conduct = 2
  density = 1
  expand = 3
  formula = G4_CADMIUM_TELLURIDE
  name = G4_CADMIUM_TELLURIDE
  specific = 4
FEATURE [App::DocumentObjectGroupPython] Cd_element002  label="Cd_element : 002"  # scripted group (container) (typed FeaturePython)
  n = 1
  ref = Cd_element
FEATURE [App::DocumentObjectGroupPython] W_element001  label="W_element : 1"  # scripted group (container) (typed FeaturePython)
  n = 1
  ref = W_element
FEATURE [App::DocumentObjectGroupPython] O_element020  label="O_element : 008"  # scripted group (container) (typed FeaturePython)
  n = 4
  ref = O_element
FEATURE [App::DocumentObjectGroupPython] G4_CADMIUM_TUNGSTATE  # scripted group (container) (typed FeaturePython)
  Dunit = g/cm3
  Dvalue = 7.9
  Group = -> [Cd_element002,W_element001,O_element020]
  conduct = 2
  density = 1
  expand = 3
  formula = G4_CADMIUM_TUNGSTATE
  name = G4_CADMIUM_TUNGSTATE
  specific = 4
FEATURE [App::DocumentObjectGroupPython] Ca_element005  label="Ca_element : 1"  # scripted group (container) (typed FeaturePython)
  n = 1
  ref = Ca_element
FEATURE [App::DocumentObjectGroupPython] C_element022  label="C_element : 009"  # scripted group (container) (typed FeaturePython)
  n = 1
  ref = C_element
FEATURE [App::DocumentObjectGroupPython] O_element021  label="O_element : 009"  # scripted group (container) (typed FeaturePython)
  n = 3
  ref = O_element
FEATURE [App::DocumentObjectGroupPython] G4_CALCIUM_CARBONATE  # scripted group (container) (typed FeaturePython)
  Dunit = g/cm3
  Dvalue = 2.8
  Group = -> [Ca_element005,C_element022,O_element021]
  conduct = 2
  density = 1
  expand = 3
  formula = G4_CALCIUM_CARBONATE
  name = G4_CALCIUM_CARBONATE
  specific = 4
FEATURE [App::DocumentObjectGroupPython] Ca_element006  label="Ca_element : 002"  # scripted group (container) (typed FeaturePython)
  n = 1
  ref = Ca_element
FEATURE [App::DocumentObjectGroupPython] F_element005  label="F_element : 003"  # scripted group (container) (typed FeaturePython)
  n = 2
  ref = F_element
FEATURE [App::DocumentObjectGroupPython] G4_CALCIUM_FLUORIDE  # scripted group (container) (typed FeaturePython)
  Dunit = g/cm3
  Dvalue = 3.18
  Group = -> [Ca_element006,F_element005]
  conduct = 2
  density = 1
  expand = 3
  formula = G4_CALCIUM_FLUORIDE
  name = G4_CALCIUM_FLUORIDE
  specific = 4
FEATURE [App::DocumentObjectGroupPython] Ca_element007  label="Ca_element : 003"  # scripted group (container) (typed FeaturePython)
  n = 1
  ref = Ca_element
FEATURE [App::DocumentObjectGroupPython] O_element022  label="O_element : 010"  # scripted group (container) (typed FeaturePython)
  n = 1
  ref = O_element
FEATURE [App::DocumentObjectGroupPython] G4_CALCIUM_OXIDE  # scripted group (container) (typed FeaturePython)
  Dunit = g/cm3
  Dvalue = 3.3
  Group = -> [Ca_element007,O_element022]
  conduct = 2
  density = 1
  expand = 3
  formula = G4_CALCIUM_OXIDE
  name = G4_CALCIUM_OXIDE
  specific = 4
FEATURE [App::DocumentObjectGroupPython] Ca_element008  label="Ca_element : 004"  # scripted group (container) (typed FeaturePython)
  n = 1
  ref = Ca_element
FEATURE [App::DocumentObjectGroupPython] S_element007  label="S_element : 002"  # scripted group (container) (typed FeaturePython)
  n = 1
  ref = S_element
FEATURE [App::DocumentObjectGroupPython] O_element023  label="O_element : 011"  # scripted group (container) (typed FeaturePython)
  n = 4
  ref = O_element
FEATURE [App::DocumentObjectGroupPython] G4_CALCIUM_SULFATE  # scripted group (container) (typed FeaturePython)
  Dunit = g/cm3
  Dvalue = 2.96
  Group = -> [Ca_element008,S_element007,O_element023]
  conduct = 2
  density = 1
  expand = 3
  formula = G4_CALCIUM_SULFATE
  name = G4_CALCIUM_SULFATE
  specific = 4
FEATURE [App::DocumentObjectGroupPython] Ca_element009  label="Ca_element : 005"  # scripted group (container) (typed FeaturePython)
  n = 1
  ref = Ca_element
FEATURE [App::DocumentObjectGroupPython] W_element002  label="W_element : 002"  # scripted group (container) (typed FeaturePython)
  n = 1
  ref = W_element
FEATURE [App::DocumentObjectGroupPython] O_element024  label="O_element : 012"  # scripted group (container) (typed FeaturePython)
  n = 4
  ref = O_element
FEATURE [App::DocumentObjectGroupPython] G4_CALCIUM_TUNGSTATE  # scripted group (container) (typed FeaturePython)
  Dunit = g/cm3
  Dvalue = 6.062
  Group = -> [Ca_element009,W_element002,O_element024]
  conduct = 2
  density = 1
  expand = 3
  formula = G4_CALCIUM_TUNGSTATE
  name = G4_CALCIUM_TUNGSTATE
  specific = 4
FEATURE [App::DocumentObjectGroupPython] C_element023  label="C_element : 010"  # scripted group (container) (typed FeaturePython)
  n = 1
  ref = C_element
FEATURE [App::DocumentObjectGroupPython] O_element025  label="O_element : 013"  # scripted group (container) (typed FeaturePython)
  n = 2
  ref = O_element
FEATURE [App::DocumentObjectGroupPython] G4_CARBON_DIOXIDE  # scripted group (container) (typed FeaturePython)
  Dunit = g/cm3
  Dvalue = 0.00184212
  Group = -> [C_element023,O_element025]
  conduct = 2
  density = 1
  expand = 3
  formula = G4_CARBON_DIOXIDE
  name = G4_CARBON_DIOXIDE
  specific = 4
FEATURE [App::DocumentObjectGroupPython] C_element024  label="C_element : 011"  # scripted group (container) (typed FeaturePython)
  n = 1
  ref = C_element
FEATURE [App::DocumentObjectGroupPython] Cl_element004  label="Cl_element : 4"  # scripted group (container) (typed FeaturePython)
  n = 4
  ref = Cl_element
FEATURE [App::DocumentObjectGroupPython] G4_CARBON_TETRACHLORIDE  # scripted group (container) (typed FeaturePython)
  Dunit = g/cm3
  Dvalue = 1.594
  Group = -> [C_element024,Cl_element004]
  conduct = 2
  density = 1
  expand = 3
  formula = G4_CARBON_TETRACHLORIDE
  name = G4_CARBON_TETRACHLORIDE
  specific = 4
FEATURE [App::DocumentObjectGroupPython] C_element025  label="C_element : 012"  # scripted group (container) (typed FeaturePython)
  n = 6
  ref = C_element
FEATURE [App::DocumentObjectGroupPython] H_element021  label="H_element : 012"  # scripted group (container) (typed FeaturePython)
  n = 10
  ref = H_element
FEATURE [App::DocumentObjectGroupPython] O_element026  label="O_element : 5"  # scripted group (container) (typed FeaturePython)
  n = 5
  ref = O_element
FEATURE [App::DocumentObjectGroupPython] G4_CELLULOSE_CELLOPHANE  # scripted group (container) (typed FeaturePython)
  Dunit = g/cm3
  Dvalue = 1.42
  Group = -> [C_element025,H_element021,O_element026]
  conduct = 2
  density = 1
  expand = 3
  formula = G4_CELLULOSE_CELLOPHANE
  name = G4_CELLULOSE_CELLOPHANE
  specific = 4
FEATURE [App::DocumentObjectGroupPython] H_element022  label="H_element : 0.067"  # scripted group (container) (typed FeaturePython)
  n = 0.067125
FEATURE [App::DocumentObjectGroupPython] C_element026  label="C_element : 0.545"  # scripted group (container) (typed FeaturePython)
  n = 0.545403
FEATURE [App::DocumentObjectGroupPython] O_element027  label="O_element : 0.387"  # scripted group (container) (typed FeaturePython)
  n = 0.387472
FEATURE [App::DocumentObjectGroupPython] G4_CELLULOSE_BUTYRATE  # scripted group (container) (typed FeaturePython)
  Dunit = g/cm3
  Dvalue = 1.2
  Group = -> [H_element022,C_element026,O_element027]
  conduct = 2
  density = 1
  expand = 3
  formula = G4_CELLULOSE_BUTYRATE
  name = G4_CELLULOSE_BUTYRATE
  specific = 4
FEATURE [App::DocumentObjectGroupPython] H_element023  label="H_element : 0.029"  # scripted group (container) (typed FeaturePython)
  n = 0.029216
FEATURE [App::DocumentObjectGroupPython] C_element027  label="C_element : 0.271"  # scripted group (container) (typed FeaturePython)
  n = 0.271296
FEATURE [App::DocumentObjectGroupPython] N_element013  label="N_element : 0.121"  # scripted group (container) (typed FeaturePython)
  n = 0.121276
FEATURE [App::DocumentObjectGroupPython] O_element028  label="O_element : 0.578"  # scripted group (container) (typed FeaturePython)
  n = 0.578212
FEATURE [App::DocumentObjectGroupPython] G4_CELLULOSE_NITRATE  # scripted group (container) (typed FeaturePython)
  Dunit = g/cm3
  Dvalue = 1.49
  Group = -> [H_element023,C_element027,N_element013,O_element028]
  conduct = 2
  density = 1
  expand = 3
  formula = G4_CELLULOSE_NITRATE
  name = G4_CELLULOSE_NITRATE
  specific = 4
FEATURE [App::DocumentObjectGroupPython] H_element024  label="H_element : 0.108"  # scripted group (container) (typed FeaturePython)
  n = 0.107596
FEATURE [App::DocumentObjectGroupPython] N_element014  label="N_element : 0.001"  # scripted group (container) (typed FeaturePython)
  n = 0.0008
FEATURE [App::DocumentObjectGroupPython] O_element029  label="O_element : 0.875"  # scripted group (container) (typed FeaturePython)
  n = 0.874976
FEATURE [App::DocumentObjectGroupPython] S_element008  label="S_element : 0.015"  # scripted group (container) (typed FeaturePython)
  n = 0.014627
FEATURE [App::DocumentObjectGroupPython] Ce_element001  label="Ce_element : 0.002"  # scripted group (container) (typed FeaturePython)
  n = 0.002001
FEATURE [App::DocumentObjectGroupPython] G4_CERIC_SULFATE  # scripted group (container) (typed FeaturePython)
  Dunit = g/cm3
  Dvalue = 1.03
  Group = -> [H_element024,N_element014,O_element029,S_element008,Ce_element001]
  conduct = 2
  density = 1
  expand = 3
  formula = G4_CERIC_SULFATE
  name = G4_CERIC_SULFATE
  specific = 4
FEATURE [App::DocumentObjectGroupPython] Cs_element001  label="Cs_element : 1"  # scripted group (container) (typed FeaturePython)
  n = 1
  ref = Cs_element
FEATURE [App::DocumentObjectGroupPython] F_element006  label="F_element : 1"  # scripted group (container) (typed FeaturePython)
  n = 1
  ref = F_element
FEATURE [App::DocumentObjectGroupPython] G4_CESIUM_FLUORIDE  # scripted group (container) (typed FeaturePython)
  Dunit = g/cm3
  Dvalue = 4.115
  Group = -> [Cs_element001,F_element006]
  conduct = 2
  density = 1
  expand = 3
  formula = G4_CESIUM_FLUORIDE
  name = G4_CESIUM_FLUORIDE
  specific = 4
FEATURE [App::DocumentObjectGroupPython] Cs_element002  label="Cs_element : 002"  # scripted group (container) (typed FeaturePython)
  n = 1
  ref = Cs_element
FEATURE [App::DocumentObjectGroupPython] I_element001  label="I_element : 1"  # scripted group (container) (typed FeaturePython)
  n = 1
  ref = I_element
FEATURE [App::DocumentObjectGroupPython] G4_CESIUM_IODIDE  # scripted group (container) (typed FeaturePython)
  Dunit = g/cm3
  Dvalue = 4.51
  Group = -> [Cs_element002,I_element001]
  conduct = 2
  density = 1
  expand = 3
  formula = G4_CESIUM_IODIDE
  name = G4_CESIUM_IODIDE
  specific = 4
FEATURE [App::DocumentObjectGroupPython] C_element028  label="C_element : 013"  # scripted group (container) (typed FeaturePython)
  n = 6
  ref = C_element
FEATURE [App::DocumentObjectGroupPython] H_element025  label="H_element : 013"  # scripted group (container) (typed FeaturePython)
  n = 5
  ref = H_element
FEATURE [App::DocumentObjectGroupPython] Cl_element005  label="Cl_element : 1"  # scripted group (container) (typed FeaturePython)
  n = 1
  ref = Cl_element
FEATURE [App::DocumentObjectGroupPython] G4_CHLOROBENZENE  # scripted group (container) (typed FeaturePython)
  Dunit = g/cm3
  Dvalue = 1.1058
  Group = -> [C_element028,H_element025,Cl_element005]
  conduct = 2
  density = 1
  expand = 3
  formula = G4_CHLOROBENZENE
  name = G4_CHLOROBENZENE
  specific = 4
FEATURE [App::DocumentObjectGroupPython] C_element029  label="C_element : 014"  # scripted group (container) (typed FeaturePython)
  n = 1
  ref = C_element
FEATURE [App::DocumentObjectGroupPython] H_element026  label="H_element : 1"  # scripted group (container) (typed FeaturePython)
  n = 1
  ref = H_element
FEATURE [App::DocumentObjectGroupPython] Cl_element006  label="Cl_element : 3"  # scripted group (container) (typed FeaturePython)
  n = 3
  ref = Cl_element
FEATURE [App::DocumentObjectGroupPython] G4_CHLOROFORM  # scripted group (container) (typed FeaturePython)
  Dunit = g/cm3
  Dvalue = 1.4832
  Group = -> [C_element029,H_element026,Cl_element006]
  conduct = 2
  density = 1
  expand = 3
  formula = G4_CHLOROFORM
  name = G4_CHLOROFORM
  specific = 4
FEATURE [App::DocumentObjectGroupPython] H_element027  label="H_element : 0.010"  # scripted group (container) (typed FeaturePython)
  n = 0.01
FEATURE [App::DocumentObjectGroupPython] C_element030  label="C_element : 0.001"  # scripted group (container) (typed FeaturePython)
  n = 0.001
FEATURE [App::DocumentObjectGroupPython] O_element030  label="O_element : 0.529"  # scripted group (container) (typed FeaturePython)
  n = 0.529107
FEATURE [App::DocumentObjectGroupPython] Na_element005  label="Na_element : 0.016"  # scripted group (container) (typed FeaturePython)
  n = 0.016
FEATURE [App::DocumentObjectGroupPython] Mg_element003  label="Mg_element : 0.004"  # scripted group (container) (typed FeaturePython)
  n = 0.002
FEATURE [App::DocumentObjectGroupPython] Al_element002  label="Al_element : 0.034"  # scripted group (container) (typed FeaturePython)
  n = 0.033872
FEATURE [App::DocumentObjectGroupPython] Si_element002  label="Si_element : 0.337"  # scripted group (container) (typed FeaturePython)
  n = 0.337021
FEATURE [App::DocumentObjectGroupPython] K_element003  label="K_element : 0.013"  # scripted group (container) (typed FeaturePython)
  n = 0.013
FEATURE [App::DocumentObjectGroupPython] Ca_element010  label="Ca_element : 0.044"  # scripted group (container) (typed FeaturePython)
  n = 0.044
FEATURE [App::DocumentObjectGroupPython] Fe_element002  label="Fe_element : 0.014"  # scripted group (container) (typed FeaturePython)
  n = 0.014
FEATURE [App::DocumentObjectGroupPython] G4_CONCRETE  # scripted group (container) (typed FeaturePython)
  Dunit = g/cm3
  Dvalue = 2.3
  Group = -> [H_element027,C_element030,O_element030,Na_element005,Mg_element003,Al_element002,Si_element002,K_element003,Ca_element010,Fe_element002]
  conduct = 2
  density = 1
  expand = 3
  formula = G4_CONCRETE
  name = G4_CONCRETE
  specific = 4
FEATURE [App::DocumentObjectGroupPython] C_element031  label="C_element : 015"  # scripted group (container) (typed FeaturePython)
  n = 6
  ref = C_element
FEATURE [App::DocumentObjectGroupPython] H_element028  label="H_element : 12"  # scripted group (container) (typed FeaturePython)
  n = 12
  ref = H_element
FEATURE [App::DocumentObjectGroupPython] G4_CYCLOHEXANE  # scripted group (container) (typed FeaturePython)
  Dunit = g/cm3
  Dvalue = 0.779
  Group = -> [C_element031,H_element028]
  conduct = 2
  density = 1
  expand = 3
  formula = G4_CYCLOHEXANE
  name = G4_CYCLOHEXANE
  specific = 4
FEATURE [App::DocumentObjectGroupPython] C_element032  label="C_element : 016"  # scripted group (container) (typed FeaturePython)
  n = 6
  ref = C_element
FEATURE [App::DocumentObjectGroupPython] H_element029  label="H_element : 4"  # scripted group (container) (typed FeaturePython)
  n = 4
  ref = H_element
FEATURE [App::DocumentObjectGroupPython] Cl_element007  label="Cl_element : 2"  # scripted group (container) (typed FeaturePython)
  n = 2
  ref = Cl_element
FEATURE [App::DocumentObjectGroupPython] G4_1_2_DICHLOROBENZENE  label="G4_1.2-DICHLOROBENZENE"  # scripted group (container) (typed FeaturePython)
  Dunit = g/cm3
  Dvalue = 1.3048
  Group = -> [C_element032,H_element029,Cl_element007]
  conduct = 2
  density = 1
  expand = 3
  formula = G4_1.2-DICHLOROBENZENE
  name = G4_1.2-DICHLOROBENZENE
  specific = 4
FEATURE [App::DocumentObjectGroupPython] C_element033  label="C_element : 017"  # scripted group (container) (typed FeaturePython)
  n = 4
  ref = C_element
FEATURE [App::DocumentObjectGroupPython] H_element030  label="H_element : 8"  # scripted group (container) (typed FeaturePython)
  n = 8
  ref = H_element
FEATURE [App::DocumentObjectGroupPython] O_element031  label="O_element : 014"  # scripted group (container) (typed FeaturePython)
  n = 1
  ref = O_element
FEATURE [App::DocumentObjectGroupPython] Cl_element008  label="Cl_element : 005"  # scripted group (container) (typed FeaturePython)
  n = 2
  ref = Cl_element
FEATURE [App::DocumentObjectGroupPython] G4_DICHLORODIETHYL_ETHER  # scripted group (container) (typed FeaturePython)
  Dunit = g/cm3
  Dvalue = 1.2199
  Group = -> [C_element033,H_element030,O_element031,Cl_element008]
  conduct = 2
  density = 1
  expand = 3
  formula = G4_DICHLORODIETHYL_ETHER
  name = G4_DICHLORODIETHYL_ETHER
  specific = 4
FEATURE [App::DocumentObjectGroupPython] C_element034  label="C_element : 018"  # scripted group (container) (typed FeaturePython)
  n = 2
  ref = C_element
FEATURE [App::DocumentObjectGroupPython] H_element031  label="H_element : 014"  # scripted group (container) (typed FeaturePython)
  n = 4
  ref = H_element
FEATURE [App::DocumentObjectGroupPython] Cl_element009  label="Cl_element : 006"  # scripted group (container) (typed FeaturePython)
  n = 2
  ref = Cl_element
FEATURE [App::DocumentObjectGroupPython] G4_1_2_DICHLOROETHANE  label="G4_1.2-DICHLOROETHANE"  # scripted group (container) (typed FeaturePython)
  Dunit = g/cm3
  Dvalue = 1.2351
  Group = -> [C_element034,H_element031,Cl_element009]
  conduct = 2
  density = 1
  expand = 3
  formula = G4_1.2-DICHLOROETHANE
  name = G4_1.2-DICHLOROETHANE
  specific = 4
FEATURE [App::DocumentObjectGroupPython] C_element035  label="C_element : 019"  # scripted group (container) (typed FeaturePython)
  n = 4
  ref = C_element
FEATURE [App::DocumentObjectGroupPython] H_element032  label="H_element : 015"  # scripted group (container) (typed FeaturePython)
  n = 10
  ref = H_element
FEATURE [App::DocumentObjectGroupPython] O_element032  label="O_element : 015"  # scripted group (container) (typed FeaturePython)
  n = 1
  ref = O_element
FEATURE [App::DocumentObjectGroupPython] G4_DIETHYL_ETHER  # scripted group (container) (typed FeaturePython)
  Dunit = g/cm3
  Dvalue = 0.71378
  Group = -> [C_element035,H_element032,O_element032]
  conduct = 2
  density = 1
  expand = 3
  formula = G4_DIETHYL_ETHER
  name = G4_DIETHYL_ETHER
  specific = 4
FEATURE [App::DocumentObjectGroupPython] C_element036  label="C_element : 020"  # scripted group (container) (typed FeaturePython)
  n = 3
  ref = C_element
FEATURE [App::DocumentObjectGroupPython] H_element033  label="H_element : 016"  # scripted group (container) (typed FeaturePython)
  n = 7
  ref = H_element
FEATURE [App::DocumentObjectGroupPython] N_element015  label="N_element : 008"  # scripted group (container) (typed FeaturePython)
  n = 1
  ref = N_element
FEATURE [App::DocumentObjectGroupPython] O_element033  label="O_element : 016"  # scripted group (container) (typed FeaturePython)
  n = 1
  ref = O_element
FEATURE [App::DocumentObjectGroupPython] G4_N_N_DIMETHYL_FORMAMIDE  label="G4_N.N-DIMETHYL_FORMAMIDE"  # scripted group (container) (typed FeaturePython)
  Dunit = g/cm3
  Dvalue = 0.9487
  Group = -> [C_element036,H_element033,N_element015,O_element033]
  conduct = 2
  density = 1
  expand = 3
  formula = G4_N.N-DIMETHYL_FORMAMIDE
  name = G4_N.N-DIMETHYL_FORMAMIDE
  specific = 4
FEATURE [App::DocumentObjectGroupPython] C_element037  label="C_element : 021"  # scripted group (container) (typed FeaturePython)
  n = 2
  ref = C_element
FEATURE [App::DocumentObjectGroupPython] H_element034  label="H_element : 017"  # scripted group (container) (typed FeaturePython)
  n = 6
  ref = H_element
FEATURE [App::DocumentObjectGroupPython] O_element034  label="O_element : 017"  # scripted group (container) (typed FeaturePython)
  n = 1
  ref = O_element
FEATURE [App::DocumentObjectGroupPython] S_element009  label="S_element : 003"  # scripted group (container) (typed FeaturePython)
  n = 1
  ref = S_element
FEATURE [App::DocumentObjectGroupPython] G4_DIMETHYL_SULFOXIDE  # scripted group (container) (typed FeaturePython)
  Dunit = g/cm3
  Dvalue = 1.1014
  Group = -> [C_element037,H_element034,O_element034,S_element009]
  conduct = 2
  density = 1
  expand = 3
  formula = G4_DIMETHYL_SULFOXIDE
  name = G4_DIMETHYL_SULFOXIDE
  specific = 4
FEATURE [App::DocumentObjectGroupPython] C_element038  label="C_element : 022"  # scripted group (container) (typed FeaturePython)
  n = 2
  ref = C_element
FEATURE [App::DocumentObjectGroupPython] H_element035  label="H_element : 018"  # scripted group (container) (typed FeaturePython)
  n = 6
  ref = H_element
FEATURE [App::DocumentObjectGroupPython] G4_ETHANE  # scripted group (container) (typed FeaturePython)
  Dunit = g/cm3
  Dvalue = 0.00125324
  Group = -> [C_element038,H_element035]
  conduct = 2
  density = 1
  expand = 3
  formula = G4_ETHANE
  name = G4_ETHANE
  specific = 4
FEATURE [App::DocumentObjectGroupPython] C_element039  label="C_element : 023"  # scripted group (container) (typed FeaturePython)
  n = 2
  ref = C_element
FEATURE [App::DocumentObjectGroupPython] H_element036  label="H_element : 019"  # scripted group (container) (typed FeaturePython)
  n = 6
  ref = H_element
FEATURE [App::DocumentObjectGroupPython] O_element035  label="O_element : 018"  # scripted group (container) (typed FeaturePython)
  n = 1
  ref = O_element
FEATURE [App::DocumentObjectGroupPython] G4_ETHYL_ALCOHOL  # scripted group (container) (typed FeaturePython)
  Dunit = g/cm3
  Dvalue = 0.7893
  Group = -> [C_element039,H_element036,O_element035]
  conduct = 2
  density = 1
  expand = 3
  formula = G4_ETHYL_ALCOHOL
  name = G4_ETHYL_ALCOHOL
  specific = 4
FEATURE [App::DocumentObjectGroupPython] H_element037  label="H_element : 0.090"  # scripted group (container) (typed FeaturePython)
  n = 0.090027
FEATURE [App::DocumentObjectGroupPython] C_element040  label="C_element : 0.585"  # scripted group (container) (typed FeaturePython)
  n = 0.585182
FEATURE [App::DocumentObjectGroupPython] O_element036  label="O_element : 0.325"  # scripted group (container) (typed FeaturePython)
  n = 0.324791
FEATURE [App::DocumentObjectGroupPython] G4_ETHYL_CELLULOSE  # scripted group (container) (typed FeaturePython)
  Dunit = g/cm3
  Dvalue = 1.13
  Group = -> [H_element037,C_element040,O_element036]
  conduct = 2
  density = 1
  expand = 3
  formula = G4_ETHYL_CELLULOSE
  name = G4_ETHYL_CELLULOSE
  specific = 4
FEATURE [App::DocumentObjectGroupPython] C_element041  label="C_element : 024"  # scripted group (container) (typed FeaturePython)
  n = 2
  ref = C_element
FEATURE [App::DocumentObjectGroupPython] H_element038  label="H_element : 020"  # scripted group (container) (typed FeaturePython)
  n = 4
  ref = H_element
FEATURE [App::DocumentObjectGroupPython] G4_ETHYLENE  # scripted group (container) (typed FeaturePython)
  Dunit = g/cm3
  Dvalue = 0.00117497
  Group = -> [C_element041,H_element038]
  conduct = 2
  density = 1
  expand = 3
  formula = G4_ETHYLENE
  name = G4_ETHYLENE
  specific = 4
FEATURE [App::DocumentObjectGroupPython] H_element039  label="H_element : 0.096"  # scripted group (container) (typed FeaturePython)
  n = 0.096
FEATURE [App::DocumentObjectGroupPython] C_element042  label="C_element : 0.195"  # scripted group (container) (typed FeaturePython)
  n = 0.195
FEATURE [App::DocumentObjectGroupPython] N_element016  label="N_element : 0.057"  # scripted group (container) (typed FeaturePython)
  n = 0.057
FEATURE [App::DocumentObjectGroupPython] O_element037  label="O_element : 0.646"  # scripted group (container) (typed FeaturePython)
  n = 0.646
FEATURE [App::DocumentObjectGroupPython] Na_element006  label="Na_element : 0.017"  # scripted group (container) (typed FeaturePython)
  n = 0.001
FEATURE [App::DocumentObjectGroupPython] P_element005  label="P_element : 0.104"  # scripted group (container) (typed FeaturePython)
  n = 0.001
FEATURE [App::DocumentObjectGroupPython] S_element010  label="S_element : 0.016"  # scripted group (container) (typed FeaturePython)
  n = 0.003
FEATURE [App::DocumentObjectGroupPython] Cl_element010  label="Cl_element : 0.005"  # scripted group (container) (typed FeaturePython)
  n = 0.001
FEATURE [App::DocumentObjectGroupPython] G4_EYE_LENS_ICRP  # scripted group (container) (typed FeaturePython)
  Dunit = g/cm3
  Dvalue = 1.07
  Group = -> [H_element039,C_element042,N_element016,O_element037,Na_element006,P_element005,S_element010,Cl_element010]
  conduct = 2
  density = 1
  expand = 3
  formula = G4_EYE_LENS_ICRP
  name = G4_EYE_LENS_ICRP
  specific = 4
FEATURE [App::DocumentObjectGroupPython] Fe_element003  label="Fe_element : 2"  # scripted group (container) (typed FeaturePython)
  n = 2
  ref = Fe_element
FEATURE [App::DocumentObjectGroupPython] O_element038  label="O_element : 019"  # scripted group (container) (typed FeaturePython)
  n = 3
  ref = O_element
FEATURE [App::DocumentObjectGroupPython] G4_FERRIC_OXIDE  # scripted group (container) (typed FeaturePython)
  Dunit = g/cm3
  Dvalue = 5.2
  Group = -> [Fe_element003,O_element038]
  conduct = 2
  density = 1
  expand = 3
  formula = G4_FERRIC_OXIDE
  name = G4_FERRIC_OXIDE
  specific = 4
FEATURE [App::DocumentObjectGroupPython] Fe_element004  label="Fe_element : 1"  # scripted group (container) (typed FeaturePython)
  n = 1
  ref = Fe_element
FEATURE [App::DocumentObjectGroupPython] B_element003  label="B_element : 1"  # scripted group (container) (typed FeaturePython)
  n = 1
  ref = B_element
FEATURE [App::DocumentObjectGroupPython] G4_FERROBORIDE  # scripted group (container) (typed FeaturePython)
  Dunit = g/cm3
  Dvalue = 7.15
  Group = -> [Fe_element004,B_element003]
  conduct = 2
  density = 1
  expand = 3
  formula = G4_FERROBORIDE
  name = G4_FERROBORIDE
  specific = 4
FEATURE [App::DocumentObjectGroupPython] Fe_element005  label="Fe_element : 003"  # scripted group (container) (typed FeaturePython)
  n = 1
  ref = Fe_element
FEATURE [App::DocumentObjectGroupPython] O_element039  label="O_element : 020"  # scripted group (container) (typed FeaturePython)
  n = 1
  ref = O_element
FEATURE [App::DocumentObjectGroupPython] G4_FERROUS_OXIDE  # scripted group (container) (typed FeaturePython)
  Dunit = g/cm3
  Dvalue = 5.7
  Group = -> [Fe_element005,O_element039]
  conduct = 2
  density = 1
  expand = 3
  formula = G4_FERROUS_OXIDE
  name = G4_FERROUS_OXIDE
  specific = 4
FEATURE [App::DocumentObjectGroupPython] H_element040  label="H_element : 0.115"  # scripted group (container) (typed FeaturePython)
  n = 0.108259
FEATURE [App::DocumentObjectGroupPython] N_element017  label="N_element : 0.000"  # scripted group (container) (typed FeaturePython)
  n = 2.7e-05
FEATURE [App::DocumentObjectGroupPython] O_element040  label="O_element : 0.879"  # scripted group (container) (typed FeaturePython)
  n = 0.878636
FEATURE [App::DocumentObjectGroupPython] Na_element007  label="Na_element : 0.000"  # scripted group (container) (typed FeaturePython)
  n = 2.2e-05
FEATURE [App::DocumentObjectGroupPython] S_element011  label="S_element : 0.013"  # scripted group (container) (typed FeaturePython)
  n = 0.012968
FEATURE [App::DocumentObjectGroupPython] Cl_element011  label="Cl_element : 0.000"  # scripted group (container) (typed FeaturePython)
  n = 3.4e-05
FEATURE [App::DocumentObjectGroupPython] Fe_element006  label="Fe_element : 0.000"  # scripted group (container) (typed FeaturePython)
  n = 5.4e-05
FEATURE [App::DocumentObjectGroupPython] G4_FERROUS_SULFATE  # scripted group (container) (typed FeaturePython)
  Dunit = g/cm3
  Dvalue = 1.024
  Group = -> [H_element040,N_element017,O_element040,Na_element007,S_element011,Cl_element011,Fe_element006]
  conduct = 2
  density = 1
  expand = 3
  formula = G4_FERROUS_SULFATE
  name = G4_FERROUS_SULFATE
  specific = 4
FEATURE [App::DocumentObjectGroupPython] C_element043  label="C_element : 0.099"  # scripted group (container) (typed FeaturePython)
  n = 0.099335
FEATURE [App::DocumentObjectGroupPython] F_element007  label="F_element : 0.314"  # scripted group (container) (typed FeaturePython)
  n = 0.314247
FEATURE [App::DocumentObjectGroupPython] Cl_element012  label="Cl_element : 0.586"  # scripted group (container) (typed FeaturePython)
  n = 0.586418
FEATURE [App::DocumentObjectGroupPython] G4_FREON_12  label="G4_FREON-12"  # scripted group (container) (typed FeaturePython)
  Dunit = g/cm3
  Dvalue = 1.12
  Group = -> [C_element043,F_element007,Cl_element012]
  conduct = 2
  density = 1
  expand = 3
  formula = G4_FREON-12
  name = G4_FREON-12
  specific = 4
FEATURE [App::DocumentObjectGroupPython] C_element044  label="C_element : 0.057"  # scripted group (container) (typed FeaturePython)
  n = 0.057245
FEATURE [App::DocumentObjectGroupPython] F_element008  label="F_element : 0.181"  # scripted group (container) (typed FeaturePython)
  n = 0.181096
FEATURE [App::DocumentObjectGroupPython] Br_element001  label="Br_element : 0.762"  # scripted group (container) (typed FeaturePython)
  n = 0.761659
FEATURE [App::DocumentObjectGroupPython] G4_FREON_12B2  label="G4_FREON-12B2"  # scripted group (container) (typed FeaturePython)
  Dunit = g/cm3
  Dvalue = 1.8
  Group = -> [C_element044,F_element008,Br_element001]
  conduct = 2
  density = 1
  expand = 3
  formula = G4_FREON-12B2
  name = G4_FREON-12B2
  specific = 4
FEATURE [App::DocumentObjectGroupPython] C_element045  label="C_element : 0.115"  # scripted group (container) (typed FeaturePython)
  n = 0.114983
FEATURE [App::DocumentObjectGroupPython] F_element009  label="F_element : 0.546"  # scripted group (container) (typed FeaturePython)
  n = 0.545621
FEATURE [App::DocumentObjectGroupPython] Cl_element013  label="Cl_element : 0.339"  # scripted group (container) (typed FeaturePython)
  n = 0.339396
FEATURE [App::DocumentObjectGroupPython] G4_FREON_13  label="G4_FREON-13"  # scripted group (container) (typed FeaturePython)
  Dunit = g/cm3
  Dvalue = 0.95
  Group = -> [C_element045,F_element009,Cl_element013]
  conduct = 2
  density = 1
  expand = 3
  formula = G4_FREON-13
  name = G4_FREON-13
  specific = 4
FEATURE [App::DocumentObjectGroupPython] C_element046  label="C_element : 025"  # scripted group (container) (typed FeaturePython)
  n = 1
  ref = C_element
FEATURE [App::DocumentObjectGroupPython] F_element010  label="F_element : 3"  # scripted group (container) (typed FeaturePython)
  n = 3
  ref = F_element
FEATURE [App::DocumentObjectGroupPython] Br_element002  label="Br_element : 1"  # scripted group (container) (typed FeaturePython)
  n = 1
  ref = Br_element
FEATURE [App::DocumentObjectGroupPython] G4_FREON_13B1  label="G4_FREON-13B1"  # scripted group (container) (typed FeaturePython)
  Dunit = g/cm3
  Dvalue = 1.5
  Group = -> [C_element046,F_element010,Br_element002]
  conduct = 2
  density = 1
  expand = 3
  formula = G4_FREON-13B1
  name = G4_FREON-13B1
  specific = 4
FEATURE [App::DocumentObjectGroupPython] C_element047  label="C_element : 0.061"  # scripted group (container) (typed FeaturePython)
  n = 0.061309
FEATURE [App::DocumentObjectGroupPython] F_element011  label="F_element : 0.291"  # scripted group (container) (typed FeaturePython)
  n = 0.290924
FEATURE [App::DocumentObjectGroupPython] I_element002  label="I_element : 0.648"  # scripted group (container) (typed FeaturePython)
  n = 0.647767
FEATURE [App::DocumentObjectGroupPython] G4_FREON_13I1  label="G4_FREON-13I1"  # scripted group (container) (typed FeaturePython)
  Dunit = g/cm3
  Dvalue = 1.8
  Group = -> [C_element047,F_element011,I_element002]
  conduct = 2
  density = 1
  expand = 3
  formula = G4_FREON-13I1
  name = G4_FREON-13I1
  specific = 4
FEATURE [App::DocumentObjectGroupPython] Gd_element001  label="Gd_element : 2"  # scripted group (container) (typed FeaturePython)
  n = 2
  ref = Gd_element
FEATURE [App::DocumentObjectGroupPython] O_element041  label="O_element : 021"  # scripted group (container) (typed FeaturePython)
  n = 2
  ref = O_element
FEATURE [App::DocumentObjectGroupPython] S_element012  label="S_element : 004"  # scripted group (container) (typed FeaturePython)
  n = 1
  ref = S_element
FEATURE [App::DocumentObjectGroupPython] G4_GADOLINIUM_OXYSULFIDE  # scripted group (container) (typed FeaturePython)
  Dunit = g/cm3
  Dvalue = 7.44
  Group = -> [Gd_element001,O_element041,S_element012]
  conduct = 2
  density = 1
  expand = 3
  formula = G4_GADOLINIUM_OXYSULFIDE
  name = G4_GADOLINIUM_OXYSULFIDE
  specific = 4
FEATURE [App::DocumentObjectGroupPython] Ga_element001  label="Ga_element : 1"  # scripted group (container) (typed FeaturePython)
  n = 1
  ref = Ga_element
FEATURE [App::DocumentObjectGroupPython] As_element001  label="As_element : 1"  # scripted group (container) (typed FeaturePython)
  n = 1
  ref = As_element
FEATURE [App::DocumentObjectGroupPython] G4_GALLIUM_ARSENIDE  # scripted group (container) (typed FeaturePython)
  Dunit = g/cm3
  Dvalue = 5.31
  Group = -> [Ga_element001,As_element001]
  conduct = 2
  density = 1
  expand = 3
  formula = G4_GALLIUM_ARSENIDE
  name = G4_GALLIUM_ARSENIDE
  specific = 4
FEATURE [App::DocumentObjectGroupPython] H_element041  label="H_element : 0.081"  # scripted group (container) (typed FeaturePython)
  n = 0.08118
FEATURE [App::DocumentObjectGroupPython] C_element048  label="C_element : 0.416"  # scripted group (container) (typed FeaturePython)
  n = 0.41606
FEATURE [App::DocumentObjectGroupPython] N_element018  label="N_element : 0.111"  # scripted group (container) (typed FeaturePython)
  n = 0.11124
FEATURE [App::DocumentObjectGroupPython] O_element042  label="O_element : 0.381"  # scripted group (container) (typed FeaturePython)
  n = 0.38064
FEATURE [App::DocumentObjectGroupPython] S_element013  label="S_element : 0.011"  # scripted group (container) (typed FeaturePython)
  n = 0.01088
FEATURE [App::DocumentObjectGroupPython] G4_GEL_PHOTO_EMULSION  # scripted group (container) (typed FeaturePython)
  Dunit = g/cm3
  Dvalue = 1.2914
  Group = -> [H_element041,C_element048,N_element018,O_element042,S_element013]
  conduct = 2
  density = 1
  expand = 3
  formula = G4_GEL_PHOTO_EMULSION
  name = G4_GEL_PHOTO_EMULSION
  specific = 4
FEATURE [App::DocumentObjectGroupPython] B_element004  label="B_element : 0.040"  # scripted group (container) (typed FeaturePython)
  n = 0.0400639
FEATURE [App::DocumentObjectGroupPython] O_element043  label="O_element : 0.540"  # scripted group (container) (typed FeaturePython)
  n = 0.539561
FEATURE [App::DocumentObjectGroupPython] Na_element008  label="Na_element : 0.028"  # scripted group (container) (typed FeaturePython)
  n = 0.0281909
FEATURE [App::DocumentObjectGroupPython] Al_element003  label="Al_element : 0.012"  # scripted group (container) (typed FeaturePython)
  n = 0.011644
FEATURE [App::DocumentObjectGroupPython] Si_element003  label="Si_element : 0.377"  # scripted group (container) (typed FeaturePython)
  n = 0.377219
FEATURE [App::DocumentObjectGroupPython] K_element004  label="K_element : 0.014"  # scripted group (container) (typed FeaturePython)
  n = 0.00332099
FEATURE [App::DocumentObjectGroupPython] G4_Pyrex_Glass  # scripted group (container) (typed FeaturePython)
  Dunit = g/cm3
  Dvalue = 2.23
  Group = -> [B_element004,O_element043,Na_element008,Al_element003,Si_element003,K_element004]
  conduct = 2
  density = 1
  expand = 3
  formula = G4_Pyrex_Glass
  name = G4_Pyrex_Glass
  specific = 4
FEATURE [App::DocumentObjectGroupPython] O_element044  label="O_element : 0.156"  # scripted group (container) (typed FeaturePython)
  n = 0.156453
FEATURE [App::DocumentObjectGroupPython] Si_element004  label="Si_element : 0.081"  # scripted group (container) (typed FeaturePython)
  n = 0.080866
FEATURE [App::DocumentObjectGroupPython] Ti_element001  label="Ti_element : 0.008"  # scripted group (container) (typed FeaturePython)
  n = 0.008092
FEATURE [App::DocumentObjectGroupPython] As_element002  label="As_element : 0.003"  # scripted group (container) (typed FeaturePython)
  n = 0.002651
FEATURE [App::DocumentObjectGroupPython] Pb_element001  label="Pb_element : 0.752"  # scripted group (container) (typed FeaturePython)
  n = 0.751938
FEATURE [App::DocumentObjectGroupPython] G4_GLASS_LEAD  # scripted group (container) (typed FeaturePython)
  Dunit = g/cm3
  Dvalue = 6.22
  Group = -> [O_element044,Si_element004,Ti_element001,As_element002,Pb_element001]
  conduct = 2
  density = 1
  expand = 3
  formula = G4_GLASS_LEAD
  name = G4_GLASS_LEAD
  specific = 4
FEATURE [App::DocumentObjectGroupPython] O_element045  label="O_element : 0.460"  # scripted group (container) (typed FeaturePython)
  n = 0.4598
FEATURE [App::DocumentObjectGroupPython] Na_element009  label="Na_element : 0.096"  # scripted group (container) (typed FeaturePython)
  n = 0.0964411
FEATURE [App::DocumentObjectGroupPython] Si_element005  label="Si_element : 0.378"  # scripted group (container) (typed FeaturePython)
  n = 0.336553
FEATURE [App::DocumentObjectGroupPython] Ca_element011  label="Ca_element : 0.107"  # scripted group (container) (typed FeaturePython)
  n = 0.107205
FEATURE [App::DocumentObjectGroupPython] G4_GLASS_PLATE  # scripted group (container) (typed FeaturePython)
  Dunit = g/cm3
  Dvalue = 2.4
  Group = -> [O_element045,Na_element009,Si_element005,Ca_element011]
  conduct = 2
  density = 1
  expand = 3
  formula = G4_GLASS_PLATE
  name = G4_GLASS_PLATE
  specific = 4
FEATURE [App::DocumentObjectGroupPython] C_element049  label="C_element : 026"  # scripted group (container) (typed FeaturePython)
  n = 5
  ref = C_element
FEATURE [App::DocumentObjectGroupPython] H_element042  label="H_element : 021"  # scripted group (container) (typed FeaturePython)
  n = 10
  ref = H_element
FEATURE [App::DocumentObjectGroupPython] N_element019  label="N_element : 2"  # scripted group (container) (typed FeaturePython)
  n = 2
  ref = N_element
FEATURE [App::DocumentObjectGroupPython] O_element046  label="O_element : 022"  # scripted group (container) (typed FeaturePython)
  n = 3
  ref = O_element
FEATURE [App::DocumentObjectGroupPython] G4_GLUTAMINE  # scripted group (container) (typed FeaturePython)
  Dunit = g/cm3
  Dvalue = 1.46
  Group = -> [C_element049,H_element042,N_element019,O_element046]
  conduct = 2
  density = 1
  expand = 3
  formula = G4_GLUTAMINE
  name = G4_GLUTAMINE
  specific = 4
FEATURE [App::DocumentObjectGroupPython] C_element050  label="C_element : 027"  # scripted group (container) (typed FeaturePython)
  n = 3
  ref = C_element
FEATURE [App::DocumentObjectGroupPython] H_element043  label="H_element : 022"  # scripted group (container) (typed FeaturePython)
  n = 8
  ref = H_element
FEATURE [App::DocumentObjectGroupPython] O_element047  label="O_element : 023"  # scripted group (container) (typed FeaturePython)
  n = 3
  ref = O_element
FEATURE [App::DocumentObjectGroupPython] G4_GLYCEROL  # scripted group (container) (typed FeaturePython)
  Dunit = g/cm3
  Dvalue = 1.2613
  Group = -> [C_element050,H_element043,O_element047]
  conduct = 2
  density = 1
  expand = 3
  formula = G4_GLYCEROL
  name = G4_GLYCEROL
  specific = 4
FEATURE [App::DocumentObjectGroupPython] C_element051  label="C_element : 028"  # scripted group (container) (typed FeaturePython)
  n = 5
  ref = C_element
FEATURE [App::DocumentObjectGroupPython] H_element044  label="H_element : 023"  # scripted group (container) (typed FeaturePython)
  n = 5
  ref = H_element
FEATURE [App::DocumentObjectGroupPython] N_element020  label="N_element : 009"  # scripted group (container) (typed FeaturePython)
  n = 5
  ref = N_element
FEATURE [App::DocumentObjectGroupPython] O_element048  label="O_element : 024"  # scripted group (container) (typed FeaturePython)
  n = 1
  ref = O_element
FEATURE [App::DocumentObjectGroupPython] G4_GUANINE  # scripted group (container) (typed FeaturePython)
  Dunit = g/cm3
  Dvalue = 2.2
  Group = -> [C_element051,H_element044,N_element020,O_element048]
  conduct = 2
  density = 1
  expand = 3
  formula = G4_GUANINE
  name = G4_GUANINE
  specific = 4
FEATURE [App::DocumentObjectGroupPython] Ca_element012  label="Ca_element : 006"  # scripted group (container) (typed FeaturePython)
  n = 1
  ref = Ca_element
FEATURE [App::DocumentObjectGroupPython] S_element014  label="S_element : 005"  # scripted group (container) (typed FeaturePython)
  n = 1
  ref = S_element
FEATURE [App::DocumentObjectGroupPython] O_element049  label="O_element : 6"  # scripted group (container) (typed FeaturePython)
  n = 6
  ref = O_element
FEATURE [App::DocumentObjectGroupPython] H_element045  label="H_element : 024"  # scripted group (container) (typed FeaturePython)
  n = 4
  ref = H_element
FEATURE [App::DocumentObjectGroupPython] G4_GYPSUM  # scripted group (container) (typed FeaturePython)
  Dunit = g/cm3
  Dvalue = 2.32
  Group = -> [Ca_element012,S_element014,O_element049,H_element045]
  conduct = 2
  density = 1
  expand = 3
  formula = G4_GYPSUM
  name = G4_GYPSUM
  specific = 4
FEATURE [App::DocumentObjectGroupPython] C_element052  label="C_element : 7"  # scripted group (container) (typed FeaturePython)
  n = 7
  ref = C_element
FEATURE [App::DocumentObjectGroupPython] H_element046  label="H_element : 16"  # scripted group (container) (typed FeaturePython)
  n = 16
  ref = H_element
FEATURE [App::DocumentObjectGroupPython] G4_N_HEPTANE  label="G4_N-HEPTANE"  # scripted group (container) (typed FeaturePython)
  Dunit = g/cm3
  Dvalue = 0.68376
  Group = -> [C_element052,H_element046]
  conduct = 2
  density = 1
  expand = 3
  formula = G4_N-HEPTANE
  name = G4_N-HEPTANE
  specific = 4
FEATURE [App::DocumentObjectGroupPython] C_element053  label="C_element : 029"  # scripted group (container) (typed FeaturePython)
  n = 6
  ref = C_element
FEATURE [App::DocumentObjectGroupPython] H_element047  label="H_element : 14"  # scripted group (container) (typed FeaturePython)
  n = 14
  ref = H_element
FEATURE [App::DocumentObjectGroupPython] G4_N_HEXANE  label="G4_N-HEXANE"  # scripted group (container) (typed FeaturePython)
  Dunit = g/cm3
  Dvalue = 0.6603
  Group = -> [C_element053,H_element047]
  conduct = 2
  density = 1
  expand = 3
  formula = G4_N-HEXANE
  name = G4_N-HEXANE
  specific = 4
FEATURE [App::DocumentObjectGroupPython] C_element054  label="C_element : 22"  # scripted group (container) (typed FeaturePython)
  n = 22
  ref = C_element
FEATURE [App::DocumentObjectGroupPython] H_element048  label="H_element : 025"  # scripted group (container) (typed FeaturePython)
  n = 10
  ref = H_element
FEATURE [App::DocumentObjectGroupPython] N_element021  label="N_element : 010"  # scripted group (container) (typed FeaturePython)
  n = 2
  ref = N_element
FEATURE [App::DocumentObjectGroupPython] O_element050  label="O_element : 025"  # scripted group (container) (typed FeaturePython)
  n = 5
  ref = O_element
FEATURE [App::DocumentObjectGroupPython] G4_KAPTON  # scripted group (container) (typed FeaturePython)
  Dunit = g/cm3
  Dvalue = 1.42
  Group = -> [C_element054,H_element048,N_element021,O_element050]
  conduct = 2
  density = 1
  expand = 3
  formula = G4_KAPTON
  name = G4_KAPTON
  specific = 4
FEATURE [App::DocumentObjectGroupPython] La_element001  label="La_element : 1"  # scripted group (container) (typed FeaturePython)
  n = 1
  ref = La_element
FEATURE [App::DocumentObjectGroupPython] Br_element003  label="Br_element : 002"  # scripted group (container) (typed FeaturePython)
  n = 1
  ref = Br_element
FEATURE [App::DocumentObjectGroupPython] O_element051  label="O_element : 026"  # scripted group (container) (typed FeaturePython)
  n = 1
  ref = O_element
FEATURE [App::DocumentObjectGroupPython] G4_LANTHANUM_OXYBROMIDE  # scripted group (container) (typed FeaturePython)
  Dunit = g/cm3
  Dvalue = 6.28
  Group = -> [La_element001,Br_element003,O_element051]
  conduct = 2
  density = 1
  expand = 3
  formula = G4_LANTHANUM_OXYBROMIDE
  name = G4_LANTHANUM_OXYBROMIDE
  specific = 4
FEATURE [App::DocumentObjectGroupPython] La_element002  label="La_element : 2"  # scripted group (container) (typed FeaturePython)
  n = 2
  ref = La_element
FEATURE [App::DocumentObjectGroupPython] O_element052  label="O_element : 027"  # scripted group (container) (typed FeaturePython)
  n = 2
  ref = O_element
FEATURE [App::DocumentObjectGroupPython] S_element015  label="S_element : 006"  # scripted group (container) (typed FeaturePython)
  n = 1
  ref = S_element
FEATURE [App::DocumentObjectGroupPython] G4_LANTHANUM_OXYSULFIDE  # scripted group (container) (typed FeaturePython)
  Dunit = g/cm3
  Dvalue = 5.86
  Group = -> [La_element002,O_element052,S_element015]
  conduct = 2
  density = 1
  expand = 3
  formula = G4_LANTHANUM_OXYSULFIDE
  name = G4_LANTHANUM_OXYSULFIDE
  specific = 4
FEATURE [App::DocumentObjectGroupPython] O_element053  label="O_element : 0.072"  # scripted group (container) (typed FeaturePython)
  n = 0.071682
FEATURE [App::DocumentObjectGroupPython] Pb_element002  label="Pb_element : 0.928"  # scripted group (container) (typed FeaturePython)
  n = 0.928318
FEATURE [App::DocumentObjectGroupPython] G4_LEAD_OXIDE  # scripted group (container) (typed FeaturePython)
  Dunit = g/cm3
  Dvalue = 9.53
  Group = -> [O_element053,Pb_element002]
  conduct = 2
  density = 1
  expand = 3
  formula = G4_LEAD_OXIDE
  name = G4_LEAD_OXIDE
  specific = 4
FEATURE [App::DocumentObjectGroupPython] Li_element001  label="Li_element : 1"  # scripted group (container) (typed FeaturePython)
  n = 1
  ref = Li_element
FEATURE [App::DocumentObjectGroupPython] N_element022  label="N_element : 011"  # scripted group (container) (typed FeaturePython)
  n = 1
  ref = N_element
FEATURE [App::DocumentObjectGroupPython] H_element049  label="H_element : 026"  # scripted group (container) (typed FeaturePython)
  n = 2
  ref = H_element
FEATURE [App::DocumentObjectGroupPython] G4_LITHIUM_AMIDE  # scripted group (container) (typed FeaturePython)
  Dunit = g/cm3
  Dvalue = 1.178
  Group = -> [Li_element001,N_element022,H_element049]
  conduct = 2
  density = 1
  expand = 3
  formula = G4_LITHIUM_AMIDE
  name = G4_LITHIUM_AMIDE
  specific = 4
FEATURE [App::DocumentObjectGroupPython] Li_element002  label="Li_element : 2"  # scripted group (container) (typed FeaturePython)
  n = 2
  ref = Li_element
FEATURE [App::DocumentObjectGroupPython] C_element055  label="C_element : 030"  # scripted group (container) (typed FeaturePython)
  n = 1
  ref = C_element
FEATURE [App::DocumentObjectGroupPython] O_element054  label="O_element : 028"  # scripted group (container) (typed FeaturePython)
  n = 3
  ref = O_element
FEATURE [App::DocumentObjectGroupPython] G4_LITHIUM_CARBONATE  # scripted group (container) (typed FeaturePython)
  Dunit = g/cm3
  Dvalue = 2.11
  Group = -> [Li_element002,C_element055,O_element054]
  conduct = 2
  density = 1
  expand = 3
  formula = G4_LITHIUM_CARBONATE
  name = G4_LITHIUM_CARBONATE
  specific = 4
FEATURE [App::DocumentObjectGroupPython] Li_element003  label="Li_element : 003"  # scripted group (container) (typed FeaturePython)
  n = 1
  ref = Li_element
FEATURE [App::DocumentObjectGroupPython] F_element012  label="F_element : 004"  # scripted group (container) (typed FeaturePython)
  n = 1
  ref = F_element
FEATURE [App::DocumentObjectGroupPython] G4_LITHIUM_FLUORIDE  # scripted group (container) (typed FeaturePython)
  Dunit = g/cm3
  Dvalue = 2.635
  Group = -> [Li_element003,F_element012]
  conduct = 2
  density = 1
  expand = 3
  formula = G4_LITHIUM_FLUORIDE
  name = G4_LITHIUM_FLUORIDE
  specific = 4
FEATURE [App::DocumentObjectGroupPython] Li_element004  label="Li_element : 004"  # scripted group (container) (typed FeaturePython)
  n = 1
  ref = Li_element
FEATURE [App::DocumentObjectGroupPython] H_element050  label="H_element : 027"  # scripted group (container) (typed FeaturePython)
  n = 1
  ref = H_element
FEATURE [App::DocumentObjectGroupPython] G4_LITHIUM_HYDRIDE  # scripted group (container) (typed FeaturePython)
  Dunit = g/cm3
  Dvalue = 0.82
  Group = -> [Li_element004,H_element050]
  conduct = 2
  density = 1
  expand = 3
  formula = G4_LITHIUM_HYDRIDE
  name = G4_LITHIUM_HYDRIDE
  specific = 4
FEATURE [App::DocumentObjectGroupPython] Li_element005  label="Li_element : 005"  # scripted group (container) (typed FeaturePython)
  n = 1
  ref = Li_element
FEATURE [App::DocumentObjectGroupPython] I_element003  label="I_element : 002"  # scripted group (container) (typed FeaturePython)
  n = 1
  ref = I_element
FEATURE [App::DocumentObjectGroupPython] G4_LITHIUM_IODIDE  # scripted group (container) (typed FeaturePython)
  Dunit = g/cm3
  Dvalue = 3.494
  Group = -> [Li_element005,I_element003]
  conduct = 2
  density = 1
  expand = 3
  formula = G4_LITHIUM_IODIDE
  name = G4_LITHIUM_IODIDE
  specific = 4
FEATURE [App::DocumentObjectGroupPython] Li_element006  label="Li_element : 006"  # scripted group (container) (typed FeaturePython)
  n = 2
  ref = Li_element
FEATURE [App::DocumentObjectGroupPython] O_element055  label="O_element : 029"  # scripted group (container) (typed FeaturePython)
  n = 1
  ref = O_element
FEATURE [App::DocumentObjectGroupPython] G4_LITHIUM_OXIDE  # scripted group (container) (typed FeaturePython)
  Dunit = g/cm3
  Dvalue = 2.013
  Group = -> [Li_element006,O_element055]
  conduct = 2
  density = 1
  expand = 3
  formula = G4_LITHIUM_OXIDE
  name = G4_LITHIUM_OXIDE
  specific = 4
FEATURE [App::DocumentObjectGroupPython] Li_element007  label="Li_element : 007"  # scripted group (container) (typed FeaturePython)
  n = 2
  ref = Li_element
FEATURE [App::DocumentObjectGroupPython] B_element005  label="B_element : 005"  # scripted group (container) (typed FeaturePython)
  n = 4
  ref = B_element
FEATURE [App::DocumentObjectGroupPython] O_element056  label="O_element : 7"  # scripted group (container) (typed FeaturePython)
  n = 7
  ref = O_element
FEATURE [App::DocumentObjectGroupPython] G4_LITHIUM_TETRABORATE  # scripted group (container) (typed FeaturePython)
  Dunit = g/cm3
  Dvalue = 2.44
  Group = -> [Li_element007,B_element005,O_element056]
  conduct = 2
  density = 1
  expand = 3
  formula = G4_LITHIUM_TETRABORATE
  name = G4_LITHIUM_TETRABORATE
  specific = 4
FEATURE [App::DocumentObjectGroupPython] H_element051  label="H_element : 0.105"  # scripted group (container) (typed FeaturePython)
  n = 0.105
FEATURE [App::DocumentObjectGroupPython] C_element056  label="C_element : 0.083"  # scripted group (container) (typed FeaturePython)
  n = 0.083
FEATURE [App::DocumentObjectGroupPython] N_element023  label="N_element : 0.023"  # scripted group (container) (typed FeaturePython)
  n = 0.023
FEATURE [App::DocumentObjectGroupPython] O_element057  label="O_element : 0.779"  # scripted group (container) (typed FeaturePython)
  n = 0.779
FEATURE [App::DocumentObjectGroupPython] Na_element010  label="Na_element : 0.097"  # scripted group (container) (typed FeaturePython)
  n = 0.002
FEATURE [App::DocumentObjectGroupPython] P_element006  label="P_element : 0.105"  # scripted group (container) (typed FeaturePython)
  n = 0.001
FEATURE [App::DocumentObjectGroupPython] S_element016  label="S_element : 0.017"  # scripted group (container) (typed FeaturePython)
  n = 0.002
FEATURE [App::DocumentObjectGroupPython] Cl_element014  label="Cl_element : 0.587"  # scripted group (container) (typed FeaturePython)
  n = 0.003
FEATURE [App::DocumentObjectGroupPython] K_element005  label="K_element : 0.015"  # scripted group (container) (typed FeaturePython)
  n = 0.002
FEATURE [App::DocumentObjectGroupPython] G4_LUNG_ICRP  # scripted group (container) (typed FeaturePython)
  Dunit = g/cm3
  Dvalue = 1.04
  Group = -> [H_element051,C_element056,N_element023,O_element057,Na_element010,P_element006,S_element016,Cl_element014,K_element005]
  conduct = 2
  density = 1
  expand = 3
  formula = G4_LUNG_ICRP
  name = G4_LUNG_ICRP
  specific = 4
FEATURE [App::DocumentObjectGroupPython] H_element052  label="H_element : 0.116"  # scripted group (container) (typed FeaturePython)
  n = 0.114318
FEATURE [App::DocumentObjectGroupPython] C_element057  label="C_element : 0.656"  # scripted group (container) (typed FeaturePython)
  n = 0.655824
FEATURE [App::DocumentObjectGroupPython] O_element058  label="O_element : 0.092"  # scripted group (container) (typed FeaturePython)
  n = 0.0921831
FEATURE [App::DocumentObjectGroupPython] Mg_element004  label="Mg_element : 0.135"  # scripted group (container) (typed FeaturePython)
  n = 0.134792
FEATURE [App::DocumentObjectGroupPython] Ca_element013  label="Ca_element : 0.003"  # scripted group (container) (typed FeaturePython)
  n = 0.002883
FEATURE [App::DocumentObjectGroupPython] G4_M3_WAX  # scripted group (container) (typed FeaturePython)
  Dunit = g/cm3
  Dvalue = 1.05
  Group = -> [H_element052,C_element057,O_element058,Mg_element004,Ca_element013]
  conduct = 2
  density = 1
  expand = 3
  formula = G4_M3_WAX
  name = G4_M3_WAX
  specific = 4
FEATURE [App::DocumentObjectGroupPython] Mg_element005  label="Mg_element : 1"  # scripted group (container) (typed FeaturePython)
  n = 1
  ref = Mg_element
FEATURE [App::DocumentObjectGroupPython] C_element058  label="C_element : 031"  # scripted group (container) (typed FeaturePython)
  n = 1
  ref = C_element
FEATURE [App::DocumentObjectGroupPython] O_element059  label="O_element : 030"  # scripted group (container) (typed FeaturePython)
  n = 3
  ref = O_element
FEATURE [App::DocumentObjectGroupPython] G4_MAGNESIUM_CARBONATE  # scripted group (container) (typed FeaturePython)
  Dunit = g/cm3
  Dvalue = 2.958
  Group = -> [Mg_element005,C_element058,O_element059]
  conduct = 2
  density = 1
  expand = 3
  formula = G4_MAGNESIUM_CARBONATE
  name = G4_MAGNESIUM_CARBONATE
  specific = 4
FEATURE [App::DocumentObjectGroupPython] Mg_element006  label="Mg_element : 002"  # scripted group (container) (typed FeaturePython)
  n = 1
  ref = Mg_element
FEATURE [App::DocumentObjectGroupPython] F_element013  label="F_element : 005"  # scripted group (container) (typed FeaturePython)
  n = 2
  ref = F_element
FEATURE [App::DocumentObjectGroupPython] G4_MAGNESIUM_FLUORIDE  # scripted group (container) (typed FeaturePython)
  Dunit = g/cm3
  Dvalue = 3
  Group = -> [Mg_element006,F_element013]
  conduct = 2
  density = 1
  expand = 3
  formula = G4_MAGNESIUM_FLUORIDE
  name = G4_MAGNESIUM_FLUORIDE
  specific = 4
FEATURE [App::DocumentObjectGroupPython] Mg_element007  label="Mg_element : 003"  # scripted group (container) (typed FeaturePython)
  n = 1
  ref = Mg_element
FEATURE [App::DocumentObjectGroupPython] O_element060  label="O_element : 031"  # scripted group (container) (typed FeaturePython)
  n = 1
  ref = O_element
FEATURE [App::DocumentObjectGroupPython] G4_MAGNESIUM_OXIDE  # scripted group (container) (typed FeaturePython)
  Dunit = g/cm3
  Dvalue = 3.58
  Group = -> [Mg_element007,O_element060]
  conduct = 2
  density = 1
  expand = 3
  formula = G4_MAGNESIUM_OXIDE
  name = G4_MAGNESIUM_OXIDE
  specific = 4
FEATURE [App::DocumentObjectGroupPython] Mg_element008  label="Mg_element : 004"  # scripted group (container) (typed FeaturePython)
  n = 1
  ref = Mg_element
FEATURE [App::DocumentObjectGroupPython] B_element006  label="B_element : 006"  # scripted group (container) (typed FeaturePython)
  n = 4
  ref = B_element
FEATURE [App::DocumentObjectGroupPython] O_element061  label="O_element : 032"  # scripted group (container) (typed FeaturePython)
  n = 7
  ref = O_element
FEATURE [App::DocumentObjectGroupPython] G4_MAGNESIUM_TETRABORATE  # scripted group (container) (typed FeaturePython)
  Dunit = g/cm3
  Dvalue = 2.53
  Group = -> [Mg_element008,B_element006,O_element061]
  conduct = 2
  density = 1
  expand = 3
  formula = G4_MAGNESIUM_TETRABORATE
  name = G4_MAGNESIUM_TETRABORATE
  specific = 4
FEATURE [App::DocumentObjectGroupPython] Hg_element001  label="Hg_element : 1"  # scripted group (container) (typed FeaturePython)
  n = 1
  ref = Hg_element
FEATURE [App::DocumentObjectGroupPython] I_element004  label="I_element : 2"  # scripted group (container) (typed FeaturePython)
  n = 2
  ref = I_element
FEATURE [App::DocumentObjectGroupPython] G4_MERCURIC_IODIDE  # scripted group (container) (typed FeaturePython)
  Dunit = g/cm3
  Dvalue = 6.36
  Group = -> [Hg_element001,I_element004]
  conduct = 2
  density = 1
  expand = 3
  formula = G4_MERCURIC_IODIDE
  name = G4_MERCURIC_IODIDE
  specific = 4
FEATURE [App::DocumentObjectGroupPython] C_element059  label="C_element : 032"  # scripted group (container) (typed FeaturePython)
  n = 1
  ref = C_element
FEATURE [App::DocumentObjectGroupPython] H_element053  label="H_element : 028"  # scripted group (container) (typed FeaturePython)
  n = 4
  ref = H_element
FEATURE [App::DocumentObjectGroupPython] G4_METHANE  # scripted group (container) (typed FeaturePython)
  Dunit = g/cm3
  Dvalue = 0.000667151
  Group = -> [C_element059,H_element053]
  conduct = 2
  density = 1
  expand = 3
  formula = G4_METHANE
  name = G4_METHANE
  specific = 4
FEATURE [App::DocumentObjectGroupPython] C_element060  label="C_element : 033"  # scripted group (container) (typed FeaturePython)
  n = 1
  ref = C_element
FEATURE [App::DocumentObjectGroupPython] H_element054  label="H_element : 029"  # scripted group (container) (typed FeaturePython)
  n = 4
  ref = H_element
FEATURE [App::DocumentObjectGroupPython] O_element062  label="O_element : 033"  # scripted group (container) (typed FeaturePython)
  n = 1
  ref = O_element
FEATURE [App::DocumentObjectGroupPython] G4_METHANOL  # scripted group (container) (typed FeaturePython)
  Dunit = g/cm3
  Dvalue = 0.7914
  Group = -> [C_element060,H_element054,O_element062]
  conduct = 2
  density = 1
  expand = 3
  formula = G4_METHANOL
  name = G4_METHANOL
  specific = 4
FEATURE [App::DocumentObjectGroupPython] H_element055  label="H_element : 0.134"  # scripted group (container) (typed FeaturePython)
  n = 0.13404
FEATURE [App::DocumentObjectGroupPython] C_element061  label="C_element : 0.778"  # scripted group (container) (typed FeaturePython)
  n = 0.77796
FEATURE [App::DocumentObjectGroupPython] O_element063  label="O_element : 0.035"  # scripted group (container) (typed FeaturePython)
  n = 0.03502
FEATURE [App::DocumentObjectGroupPython] Mg_element009  label="Mg_element : 0.039"  # scripted group (container) (typed FeaturePython)
  n = 0.038594
FEATURE [App::DocumentObjectGroupPython] Ti_element002  label="Ti_element : 0.014"  # scripted group (container) (typed FeaturePython)
  n = 0.014386
FEATURE [App::DocumentObjectGroupPython] G4_MIX_D_WAX  # scripted group (container) (typed FeaturePython)
  Dunit = g/cm3
  Dvalue = 0.99
  Group = -> [H_element055,C_element061,O_element063,Mg_element009,Ti_element002]
  conduct = 2
  density = 1
  expand = 3
  formula = G4_MIX_D_WAX
  name = G4_MIX_D_WAX
  specific = 4
FEATURE [App::DocumentObjectGroupPython] H_element056  label="H_element : 0.135"  # scripted group (container) (typed FeaturePython)
  n = 0.081192
FEATURE [App::DocumentObjectGroupPython] C_element062  label="C_element : 0.583"  # scripted group (container) (typed FeaturePython)
  n = 0.583442
FEATURE [App::DocumentObjectGroupPython] N_element024  label="N_element : 0.018"  # scripted group (container) (typed FeaturePython)
  n = 0.017798
FEATURE [App::DocumentObjectGroupPython] O_element064  label="O_element : 0.186"  # scripted group (container) (typed FeaturePython)
  n = 0.186381
FEATURE [App::DocumentObjectGroupPython] Mg_element010  label="Mg_element : 0.130"  # scripted group (container) (typed FeaturePython)
  n = 0.130287
FEATURE [App::DocumentObjectGroupPython] Cl_element015  label="Cl_element : 0.588"  # scripted group (container) (typed FeaturePython)
  n = 0.0009
FEATURE [App::DocumentObjectGroupPython] G4_MS20_TISSUE  # scripted group (container) (typed FeaturePython)
  Dunit = g/cm3
  Dvalue = 1
  Group = -> [H_element056,C_element062,N_element024,O_element064,Mg_element010,Cl_element015]
  conduct = 2
  density = 1
  expand = 3
  formula = G4_MS20_TISSUE
  name = G4_MS20_TISSUE
  specific = 4
FEATURE [App::DocumentObjectGroupPython] H_element057  label="H_element : 0.136"  # scripted group (container) (typed FeaturePython)
  n = 0.102
FEATURE [App::DocumentObjectGroupPython] C_element063  label="C_element : 0.143"  # scripted group (container) (typed FeaturePython)
  n = 0.143
FEATURE [App::DocumentObjectGroupPython] N_element025  label="N_element : 0.034"  # scripted group (container) (typed FeaturePython)
  n = 0.034
FEATURE [App::DocumentObjectGroupPython] O_element065  label="O_element : 0.710"  # scripted group (container) (typed FeaturePython)
  n = 0.71
FEATURE [App::DocumentObjectGroupPython] Na_element011  label="Na_element : 0.098"  # scripted group (container) (typed FeaturePython)
  n = 0.001
FEATURE [App::DocumentObjectGroupPython] P_element007  label="P_element : 0.002"  # scripted group (container) (typed FeaturePython)
  n = 0.002
FEATURE [App::DocumentObjectGroupPython] S_element017  label="S_element : 0.018"  # scripted group (container) (typed FeaturePython)
  n = 0.003
FEATURE [App::DocumentObjectGroupPython] Cl_element016  label="Cl_element : 0.589"  # scripted group (container) (typed FeaturePython)
  n = 0.001
FEATURE [App::DocumentObjectGroupPython] K_element006  label="K_element : 0.004"  # scripted group (container) (typed FeaturePython)
  n = 0.004
FEATURE [App::DocumentObjectGroupPython] G4_MUSCLE_SKELETAL_ICRP  # scripted group (container) (typed FeaturePython)
  Dunit = g/cm3
  Dvalue = 1.05
  Group = -> [H_element057,C_element063,N_element025,O_element065,Na_element011,P_element007,S_element017,Cl_element016,K_element006]
  conduct = 2
  density = 1
  expand = 3
  formula = G4_MUSCLE_SKELETAL_ICRP
  name = G4_MUSCLE_SKELETAL_ICRP
  specific = 4
FEATURE [App::DocumentObjectGroupPython] H_element058  label="H_element : 0.137"  # scripted group (container) (typed FeaturePython)
  n = 0.102102
FEATURE [App::DocumentObjectGroupPython] C_element064  label="C_element : 0.123"  # scripted group (container) (typed FeaturePython)
  n = 0.123123
FEATURE [App::DocumentObjectGroupPython] N_element026  label="N_element : 0.756"  # scripted group (container) (typed FeaturePython)
  n = 0.035035
FEATURE [App::DocumentObjectGroupPython] O_element066  label="O_element : 0.730"  # scripted group (container) (typed FeaturePython)
  n = 0.72973
FEATURE [App::DocumentObjectGroupPython] Na_element012  label="Na_element : 0.099"  # scripted group (container) (typed FeaturePython)
  n = 0.001001
FEATURE [App::DocumentObjectGroupPython] P_element008  label="P_element : 0.106"  # scripted group (container) (typed FeaturePython)
  n = 0.002002
FEATURE [App::DocumentObjectGroupPython] S_element018  label="S_element : 0.019"  # scripted group (container) (typed FeaturePython)
  n = 0.004004
FEATURE [App::DocumentObjectGroupPython] K_element007  label="K_element : 0.016"  # scripted group (container) (typed FeaturePython)
  n = 0.003003
FEATURE [App::DocumentObjectGroupPython] G4_MUSCLE_STRIATED_ICRU  # scripted group (container) (typed FeaturePython)
  Dunit = g/cm3
  Dvalue = 1.04
  Group = -> [H_element058,C_element064,N_element026,O_element066,Na_element012,P_element008,S_element018,K_element007]
  conduct = 2
  density = 1
  expand = 3
  formula = G4_MUSCLE_STRIATED_ICRU
  name = G4_MUSCLE_STRIATED_ICRU
  specific = 4
FEATURE [App::DocumentObjectGroupPython] H_element059  label="H_element : 0.098"  # scripted group (container) (typed FeaturePython)
  n = 0.0982341
FEATURE [App::DocumentObjectGroupPython] C_element065  label="C_element : 0.156"  # scripted group (container) (typed FeaturePython)
  n = 0.156214
FEATURE [App::DocumentObjectGroupPython] N_element027  label="N_element : 0.757"  # scripted group (container) (typed FeaturePython)
  n = 0.035451
FEATURE [App::DocumentObjectGroupPython] O_element067  label="O_element : 0.880"  # scripted group (container) (typed FeaturePython)
  n = 0.710101
FEATURE [App::DocumentObjectGroupPython] G4_MUSCLE_WITH_SUCROSE  # scripted group (container) (typed FeaturePython)
  Dunit = g/cm3
  Dvalue = 1.11
  Group = -> [H_element059,C_element065,N_element027,O_element067]
  conduct = 2
  density = 1
  expand = 3
  formula = G4_MUSCLE_WITH_SUCROSE
  name = G4_MUSCLE_WITH_SUCROSE
  specific = 4
FEATURE [App::DocumentObjectGroupPython] H_element060  label="H_element : 0.138"  # scripted group (container) (typed FeaturePython)
  n = 0.101969
FEATURE [App::DocumentObjectGroupPython] C_element066  label="C_element : 0.120"  # scripted group (container) (typed FeaturePython)
  n = 0.120058
FEATURE [App::DocumentObjectGroupPython] N_element028  label="N_element : 0.758"  # scripted group (container) (typed FeaturePython)
  n = 0.035451
FEATURE [App::DocumentObjectGroupPython] O_element068  label="O_element : 0.743"  # scripted group (container) (typed FeaturePython)
  n = 0.742522
FEATURE [App::DocumentObjectGroupPython] G4_MUSCLE_WITHOUT_SUCROSE  # scripted group (container) (typed FeaturePython)
  Dunit = g/cm3
  Dvalue = 1.07
  Group = -> [H_element060,C_element066,N_element028,O_element068]
  conduct = 2
  density = 1
  expand = 3
  formula = G4_MUSCLE_WITHOUT_SUCROSE
  name = G4_MUSCLE_WITHOUT_SUCROSE
  specific = 4
FEATURE [App::DocumentObjectGroupPython] C_element067  label="C_element : 10"  # scripted group (container) (typed FeaturePython)
  n = 10
  ref = C_element
FEATURE [App::DocumentObjectGroupPython] H_element061  label="H_element : 030"  # scripted group (container) (typed FeaturePython)
  n = 8
  ref = H_element
FEATURE [App::DocumentObjectGroupPython] G4_NAPHTHALENE  # scripted group (container) (typed FeaturePython)
  Dunit = g/cm3
  Dvalue = 1.145
  Group = -> [C_element067,H_element061]
  conduct = 2
  density = 1
  expand = 3
  formula = G4_NAPHTHALENE
  name = G4_NAPHTHALENE
  specific = 4
FEATURE [App::DocumentObjectGroupPython] C_element068  label="C_element : 034"  # scripted group (container) (typed FeaturePython)
  n = 6
  ref = C_element
FEATURE [App::DocumentObjectGroupPython] H_element062  label="H_element : 031"  # scripted group (container) (typed FeaturePython)
  n = 5
  ref = H_element
FEATURE [App::DocumentObjectGroupPython] N_element029  label="N_element : 012"  # scripted group (container) (typed FeaturePython)
  n = 1
  ref = N_element
FEATURE [App::DocumentObjectGroupPython] O_element069  label="O_element : 034"  # scripted group (container) (typed FeaturePython)
  n = 2
  ref = O_element
FEATURE [App::DocumentObjectGroupPython] G4_NITROBENZENE  # scripted group (container) (typed FeaturePython)
  Dunit = g/cm3
  Dvalue = 1.19867
  Group = -> [C_element068,H_element062,N_element029,O_element069]
  conduct = 2
  density = 1
  expand = 3
  formula = G4_NITROBENZENE
  name = G4_NITROBENZENE
  specific = 4
FEATURE [App::DocumentObjectGroupPython] N_element030  label="N_element : 013"  # scripted group (container) (typed FeaturePython)
  n = 2
  ref = N_element
FEATURE [App::DocumentObjectGroupPython] O_element070  label="O_element : 035"  # scripted group (container) (typed FeaturePython)
  n = 1
  ref = O_element
FEATURE [App::DocumentObjectGroupPython] G4_NITROUS_OXIDE  # scripted group (container) (typed FeaturePython)
  Dunit = g/cm3
  Dvalue = 0.00183094
  Group = -> [N_element030,O_element070]
  conduct = 2
  density = 1
  expand = 3
  formula = G4_NITROUS_OXIDE
  name = G4_NITROUS_OXIDE
  specific = 4
FEATURE [App::DocumentObjectGroupPython] H_element063  label="H_element : 0.104"  # scripted group (container) (typed FeaturePython)
  n = 0.103509
FEATURE [App::DocumentObjectGroupPython] C_element069  label="C_element : 0.648"  # scripted group (container) (typed FeaturePython)
  n = 0.648416
FEATURE [App::DocumentObjectGroupPython] N_element031  label="N_element : 0.100"  # scripted group (container) (typed FeaturePython)
  n = 0.0995361
FEATURE [App::DocumentObjectGroupPython] O_element071  label="O_element : 0.149"  # scripted group (container) (typed FeaturePython)
  n = 0.148539
FEATURE [App::DocumentObjectGroupPython] G4_NYLON_8062  label="G4_NYLON-8062"  # scripted group (container) (typed FeaturePython)
  Dunit = g/cm3
  Dvalue = 1.08
  Group = -> [H_element063,C_element069,N_element031,O_element071]
  conduct = 2
  density = 1
  expand = 3
  formula = G4_NYLON-8062
  name = G4_NYLON-8062
  specific = 4
FEATURE [App::DocumentObjectGroupPython] C_element070  label="C_element : 035"  # scripted group (container) (typed FeaturePython)
  n = 6
  ref = C_element
FEATURE [App::DocumentObjectGroupPython] H_element064  label="H_element : 11"  # scripted group (container) (typed FeaturePython)
  n = 11
  ref = H_element
FEATURE [App::DocumentObjectGroupPython] N_element032  label="N_element : 014"  # scripted group (container) (typed FeaturePython)
  n = 1
  ref = N_element
FEATURE [App::DocumentObjectGroupPython] O_element072  label="O_element : 036"  # scripted group (container) (typed FeaturePython)
  n = 1
  ref = O_element
FEATURE [App::DocumentObjectGroupPython] G4_NYLON_6_6  label="G4_NYLON-6-6"  # scripted group (container) (typed FeaturePython)
  Dunit = g/cm3
  Dvalue = 1.14
  Group = -> [C_element070,H_element064,N_element032,O_element072]
  conduct = 2
  density = 1
  expand = 3
  formula = G4_NYLON-6-6
  name = G4_NYLON-6-6
  specific = 4
FEATURE [App::DocumentObjectGroupPython] H_element065  label="H_element : 0.139"  # scripted group (container) (typed FeaturePython)
  n = 0.107062
FEATURE [App::DocumentObjectGroupPython] C_element071  label="C_element : 0.680"  # scripted group (container) (typed FeaturePython)
  n = 0.680449
FEATURE [App::DocumentObjectGroupPython] N_element033  label="N_element : 0.099"  # scripted group (container) (typed FeaturePython)
  n = 0.099189
FEATURE [App::DocumentObjectGroupPython] O_element073  label="O_element : 0.113"  # scripted group (container) (typed FeaturePython)
  n = 0.1133
FEATURE [App::DocumentObjectGroupPython] G4_NYLON_6_10  label="G4_NYLON-6-10"  # scripted group (container) (typed FeaturePython)
  Dunit = g/cm3
  Dvalue = 1.14
  Group = -> [H_element065,C_element071,N_element033,O_element073]
  conduct = 2
  density = 1
  expand = 3
  formula = G4_NYLON-6-10
  name = G4_NYLON-6-10
  specific = 4
FEATURE [App::DocumentObjectGroupPython] H_element066  label="H_element : 0.140"  # scripted group (container) (typed FeaturePython)
  n = 0.115476
FEATURE [App::DocumentObjectGroupPython] C_element072  label="C_element : 0.721"  # scripted group (container) (typed FeaturePython)
  n = 0.720818
FEATURE [App::DocumentObjectGroupPython] N_element034  label="N_element : 0.076"  # scripted group (container) (typed FeaturePython)
  n = 0.0764169
FEATURE [App::DocumentObjectGroupPython] O_element074  label="O_element : 0.087"  # scripted group (container) (typed FeaturePython)
  n = 0.0872889
FEATURE [App::DocumentObjectGroupPython] G4_NYLON_11_RILSAN  label="G4_NYLON-11_RILSAN"  # scripted group (container) (typed FeaturePython)
  Dunit = g/cm3
  Dvalue = 1.425
  Group = -> [H_element066,C_element072,N_element034,O_element074]
  conduct = 2
  density = 1
  expand = 3
  formula = G4_NYLON-11_RILSAN
  name = G4_NYLON-11_RILSAN
  specific = 4
FEATURE [App::DocumentObjectGroupPython] C_element073  label="C_element : 8"  # scripted group (container) (typed FeaturePython)
  n = 8
  ref = C_element
FEATURE [App::DocumentObjectGroupPython] H_element067  label="H_element : 18"  # scripted group (container) (typed FeaturePython)
  n = 18
  ref = H_element
FEATURE [App::DocumentObjectGroupPython] G4_OCTANE  # scripted group (container) (typed FeaturePython)
  Dunit = g/cm3
  Dvalue = 0.7026
  Group = -> [C_element073,H_element067]
  conduct = 2
  density = 1
  expand = 3
  formula = G4_OCTANE
  name = G4_OCTANE
  specific = 4
FEATURE [App::DocumentObjectGroupPython] C_element074  label="C_element : 25"  # scripted group (container) (typed FeaturePython)
  n = 25
  ref = C_element
FEATURE [App::DocumentObjectGroupPython] H_element068  label="H_element : 52"  # scripted group (container) (typed FeaturePython)
  n = 52
  ref = H_element
FEATURE [App::DocumentObjectGroupPython] G4_PARAFFIN  # scripted group (container) (typed FeaturePython)
  Dunit = g/cm3
  Dvalue = 0.93
  Group = -> [C_element074,H_element068]
  conduct = 2
  density = 1
  expand = 3
  formula = G4_PARAFFIN
  name = G4_PARAFFIN
  specific = 4
FEATURE [App::DocumentObjectGroupPython] C_element075  label="C_element : 036"  # scripted group (container) (typed FeaturePython)
  n = 5
  ref = C_element
FEATURE [App::DocumentObjectGroupPython] H_element069  label="H_element : 032"  # scripted group (container) (typed FeaturePython)
  n = 12
  ref = H_element
FEATURE [App::DocumentObjectGroupPython] G4_N_PENTANE  label="G4_N-PENTANE"  # scripted group (container) (typed FeaturePython)
  Dunit = g/cm3
  Dvalue = 0.6262
  Group = -> [C_element075,H_element069]
  conduct = 2
  density = 1
  expand = 3
  formula = G4_N-PENTANE
  name = G4_N-PENTANE
  specific = 4
FEATURE [App::DocumentObjectGroupPython] H_element070  label="H_element : 0.014"  # scripted group (container) (typed FeaturePython)
  n = 0.0141
FEATURE [App::DocumentObjectGroupPython] C_element076  label="C_element : 0.072"  # scripted group (container) (typed FeaturePython)
  n = 0.072261
FEATURE [App::DocumentObjectGroupPython] N_element035  label="N_element : 0.019"  # scripted group (container) (typed FeaturePython)
  n = 0.01932
FEATURE [App::DocumentObjectGroupPython] O_element075  label="O_element : 0.066"  # scripted group (container) (typed FeaturePython)
  n = 0.066101
FEATURE [App::DocumentObjectGroupPython] S_element019  label="S_element : 0.020"  # scripted group (container) (typed FeaturePython)
  n = 0.00189
FEATURE [App::DocumentObjectGroupPython] Br_element004  label="Br_element : 0.349"  # scripted group (container) (typed FeaturePython)
  n = 0.349103
FEATURE [App::DocumentObjectGroupPython] Ag_element001  label="Ag_element : 0.474"  # scripted group (container) (typed FeaturePython)
  n = 0.474105
FEATURE [App::DocumentObjectGroupPython] I_element005  label="I_element : 0.003"  # scripted group (container) (typed FeaturePython)
  n = 0.00312
FEATURE [App::DocumentObjectGroupPython] G4_PHOTO_EMULSION  # scripted group (container) (typed FeaturePython)
  Dunit = g/cm3
  Dvalue = 3.815
  Group = -> [H_element070,C_element076,N_element035,O_element075,S_element019,Br_element004,Ag_element001,I_element005]
  conduct = 2
  density = 1
  expand = 3
  formula = G4_PHOTO_EMULSION
  name = G4_PHOTO_EMULSION
  specific = 4
FEATURE [App::DocumentObjectGroupPython] C_element077  label="C_element : 9"  # scripted group (container) (typed FeaturePython)
  n = 9
  ref = C_element
FEATURE [App::DocumentObjectGroupPython] H_element071  label="H_element : 033"  # scripted group (container) (typed FeaturePython)
  n = 10
  ref = H_element
FEATURE [App::DocumentObjectGroupPython] G4_PLASTIC_SC_VINYLTOLUENE  # scripted group (container) (typed FeaturePython)
  Dunit = g/cm3
  Dvalue = 1.032
  Group = -> [C_element077,H_element071]
  conduct = 2
  density = 1
  expand = 3
  formula = G4_PLASTIC_SC_VINYLTOLUENE
  name = G4_PLASTIC_SC_VINYLTOLUENE
  specific = 4
FEATURE [App::DocumentObjectGroupPython] Pu_element001  label="Pu_element : 1"  # scripted group (container) (typed FeaturePython)
  n = 1
  ref = Pu_element
FEATURE [App::DocumentObjectGroupPython] O_element076  label="O_element : 037"  # scripted group (container) (typed FeaturePython)
  n = 2
  ref = O_element
FEATURE [App::DocumentObjectGroupPython] G4_PLUTONIUM_DIOXIDE  # scripted group (container) (typed FeaturePython)
  Dunit = g/cm3
  Dvalue = 11.46
  Group = -> [Pu_element001,O_element076]
  conduct = 2
  density = 1
  expand = 3
  formula = G4_PLUTONIUM_DIOXIDE
  name = G4_PLUTONIUM_DIOXIDE
  specific = 4
FEATURE [App::DocumentObjectGroupPython] C_element078  label="C_element : 037"  # scripted group (container) (typed FeaturePython)
  n = 3
  ref = C_element
FEATURE [App::DocumentObjectGroupPython] H_element072  label="H_element : 034"  # scripted group (container) (typed FeaturePython)
  n = 3
  ref = H_element
FEATURE [App::DocumentObjectGroupPython] N_element036  label="N_element : 015"  # scripted group (container) (typed FeaturePython)
  n = 1
  ref = N_element
FEATURE [App::DocumentObjectGroupPython] G4_POLYACRYLONITRILE  # scripted group (container) (typed FeaturePython)
  Dunit = g/cm3
  Dvalue = 1.17
  Group = -> [C_element078,H_element072,N_element036]
  conduct = 2
  density = 1
  expand = 3
  formula = G4_POLYACRYLONITRILE
  name = G4_POLYACRYLONITRILE
  specific = 4
FEATURE [App::DocumentObjectGroupPython] C_element079  label="C_element : 16"  # scripted group (container) (typed FeaturePython)
  n = 16
  ref = C_element
FEATURE [App::DocumentObjectGroupPython] H_element073  label="H_element : 035"  # scripted group (container) (typed FeaturePython)
  n = 14
  ref = H_element
FEATURE [App::DocumentObjectGroupPython] O_element077  label="O_element : 038"  # scripted group (container) (typed FeaturePython)
  n = 3
  ref = O_element
FEATURE [App::DocumentObjectGroupPython] G4_POLYCARBONATE  # scripted group (container) (typed FeaturePython)
  Dunit = g/cm3
  Dvalue = 1.2
  Group = -> [C_element079,H_element073,O_element077]
  conduct = 2
  density = 1
  expand = 3
  formula = G4_POLYCARBONATE
  name = G4_POLYCARBONATE
  specific = 4
FEATURE [App::DocumentObjectGroupPython] C_element080  label="C_element : 038"  # scripted group (container) (typed FeaturePython)
  n = 8
  ref = C_element
FEATURE [App::DocumentObjectGroupPython] H_element074  label="H_element : 036"  # scripted group (container) (typed FeaturePython)
  n = 7
  ref = H_element
FEATURE [App::DocumentObjectGroupPython] Cl_element017  label="Cl_element : 007"  # scripted group (container) (typed FeaturePython)
  n = 1
  ref = Cl_element
FEATURE [App::DocumentObjectGroupPython] G4_POLYCHLOROSTYRENE  # scripted group (container) (typed FeaturePython)
  Dunit = g/cm3
  Dvalue = 1.3
  Group = -> [C_element080,H_element074,Cl_element017]
  conduct = 2
  density = 1
  expand = 3
  formula = G4_POLYCHLOROSTYRENE
  name = G4_POLYCHLOROSTYRENE
  specific = 4
FEATURE [App::DocumentObjectGroupPython] C_element081  label="C_element : 039"  # scripted group (container) (typed FeaturePython)
  n = 1
  ref = C_element
FEATURE [App::DocumentObjectGroupPython] H_element075  label="H_element : 037"  # scripted group (container) (typed FeaturePython)
  n = 2
  ref = H_element
FEATURE [App::DocumentObjectGroupPython] G4_POLYETHYLENE  # scripted group (container) (typed FeaturePython)
  Dunit = g/cm3
  Dvalue = 0.94
  Group = -> [C_element081,H_element075]
  conduct = 2
  density = 1
  expand = 3
  formula = G4_POLYETHYLENE
  name = G4_POLYETHYLENE
  specific = 4
FEATURE [App::DocumentObjectGroupPython] C_element082  label="C_element : 040"  # scripted group (container) (typed FeaturePython)
  n = 10
  ref = C_element
FEATURE [App::DocumentObjectGroupPython] H_element076  label="H_element : 038"  # scripted group (container) (typed FeaturePython)
  n = 8
  ref = H_element
FEATURE [App::DocumentObjectGroupPython] O_element078  label="O_element : 039"  # scripted group (container) (typed FeaturePython)
  n = 4
  ref = O_element
FEATURE [App::DocumentObjectGroupPython] G4_MYLAR  # scripted group (container) (typed FeaturePython)
  Dunit = g/cm3
  Dvalue = 1.4
  Group = -> [C_element082,H_element076,O_element078]
  conduct = 2
  density = 1
  expand = 3
  formula = G4_MYLAR
  name = G4_MYLAR
  specific = 4
FEATURE [App::DocumentObjectGroupPython] C_element083  label="C_element : 041"  # scripted group (container) (typed FeaturePython)
  n = 5
  ref = C_element
FEATURE [App::DocumentObjectGroupPython] H_element077  label="H_element : 039"  # scripted group (container) (typed FeaturePython)
  n = 8
  ref = H_element
FEATURE [App::DocumentObjectGroupPython] O_element079  label="O_element : 040"  # scripted group (container) (typed FeaturePython)
  n = 2
  ref = O_element
FEATURE [App::DocumentObjectGroupPython] G4_PLEXIGLASS  # scripted group (container) (typed FeaturePython)
  Dunit = g/cm3
  Dvalue = 1.19
  Group = -> [C_element083,H_element077,O_element079]
  conduct = 2
  density = 1
  expand = 3
  formula = G4_PLEXIGLASS
  name = G4_PLEXIGLASS
  specific = 4
FEATURE [App::DocumentObjectGroupPython] C_element084  label="C_element : 042"  # scripted group (container) (typed FeaturePython)
  n = 1
  ref = C_element
FEATURE [App::DocumentObjectGroupPython] H_element078  label="H_element : 040"  # scripted group (container) (typed FeaturePython)
  n = 2
  ref = H_element
FEATURE [App::DocumentObjectGroupPython] O_element080  label="O_element : 041"  # scripted group (container) (typed FeaturePython)
  n = 1
  ref = O_element
FEATURE [App::DocumentObjectGroupPython] G4_POLYOXYMETHYLENE  # scripted group (container) (typed FeaturePython)
  Dunit = g/cm3
  Dvalue = 1.425
  Group = -> [C_element084,H_element078,O_element080]
  conduct = 2
  density = 1
  expand = 3
  formula = G4_POLYOXYMETHYLENE
  name = G4_POLYOXYMETHYLENE
  specific = 4
FEATURE [App::DocumentObjectGroupPython] C_element085  label="C_element : 043"  # scripted group (container) (typed FeaturePython)
  n = 2
  ref = C_element
FEATURE [App::DocumentObjectGroupPython] H_element079  label="H_element : 041"  # scripted group (container) (typed FeaturePython)
  n = 4
  ref = H_element
FEATURE [App::DocumentObjectGroupPython] G4_POLYPROPYLENE  # scripted group (container) (typed FeaturePython)
  Dunit = g/cm3
  Dvalue = 0.9
  Group = -> [C_element085,H_element079]
  conduct = 2
  density = 1
  expand = 3
  formula = G4_POLYPROPYLENE
  name = G4_POLYPROPYLENE
  specific = 4
FEATURE [App::DocumentObjectGroupPython] C_element086  label="C_element : 044"  # scripted group (container) (typed FeaturePython)
  n = 8
  ref = C_element
FEATURE [App::DocumentObjectGroupPython] H_element080  label="H_element : 042"  # scripted group (container) (typed FeaturePython)
  n = 8
  ref = H_element
FEATURE [App::DocumentObjectGroupPython] G4_POLYSTYRENE  # scripted group (container) (typed FeaturePython)
  Dunit = g/cm3
  Dvalue = 1.06
  Group = -> [C_element086,H_element080]
  conduct = 2
  density = 1
  expand = 3
  formula = G4_POLYSTYRENE
  name = G4_POLYSTYRENE
  specific = 4
FEATURE [App::DocumentObjectGroupPython] C_element087  label="C_element : 045"  # scripted group (container) (typed FeaturePython)
  n = 2
  ref = C_element
FEATURE [App::DocumentObjectGroupPython] F_element014  label="F_element : 4"  # scripted group (container) (typed FeaturePython)
  n = 4
  ref = F_element
FEATURE [App::DocumentObjectGroupPython] G4_TEFLON  # scripted group (container) (typed FeaturePython)
  Dunit = g/cm3
  Dvalue = 2.2
  Group = -> [C_element087,F_element014]
  conduct = 2
  density = 1
  expand = 3
  formula = G4_TEFLON
  name = G4_TEFLON
  specific = 4
FEATURE [App::DocumentObjectGroupPython] C_element088  label="C_element : 046"  # scripted group (container) (typed FeaturePython)
  n = 2
  ref = C_element
FEATURE [App::DocumentObjectGroupPython] F_element015  label="F_element : 006"  # scripted group (container) (typed FeaturePython)
  n = 3
  ref = F_element
FEATURE [App::DocumentObjectGroupPython] Cl_element018  label="Cl_element : 008"  # scripted group (container) (typed FeaturePython)
  n = 1
  ref = Cl_element
FEATURE [App::DocumentObjectGroupPython] G4_POLYTRIFLUOROCHLOROETHYLENE  # scripted group (container) (typed FeaturePython)
  Dunit = g/cm3
  Dvalue = 2.1
  Group = -> [C_element088,F_element015,Cl_element018]
  conduct = 2
  density = 1
  expand = 3
  formula = G4_POLYTRIFLUOROCHLOROETHYLENE
  name = G4_POLYTRIFLUOROCHLOROETHYLENE
  specific = 4
FEATURE [App::DocumentObjectGroupPython] C_element089  label="C_element : 047"  # scripted group (container) (typed FeaturePython)
  n = 4
  ref = C_element
FEATURE [App::DocumentObjectGroupPython] H_element081  label="H_element : 043"  # scripted group (container) (typed FeaturePython)
  n = 6
  ref = H_element
FEATURE [App::DocumentObjectGroupPython] O_element081  label="O_element : 042"  # scripted group (container) (typed FeaturePython)
  n = 2
  ref = O_element
FEATURE [App::DocumentObjectGroupPython] G4_POLYVINYL_ACETATE  # scripted group (container) (typed FeaturePython)
  Dunit = g/cm3
  Dvalue = 1.19
  Group = -> [C_element089,H_element081,O_element081]
  conduct = 2
  density = 1
  expand = 3
  formula = G4_POLYVINYL_ACETATE
  name = G4_POLYVINYL_ACETATE
  specific = 4
FEATURE [App::DocumentObjectGroupPython] C_element090  label="C_element : 048"  # scripted group (container) (typed FeaturePython)
  n = 2
  ref = C_element
FEATURE [App::DocumentObjectGroupPython] H_element082  label="H_element : 044"  # scripted group (container) (typed FeaturePython)
  n = 4
  ref = H_element
FEATURE [App::DocumentObjectGroupPython] O_element082  label="O_element : 043"  # scripted group (container) (typed FeaturePython)
  n = 1
  ref = O_element
FEATURE [App::DocumentObjectGroupPython] G4_POLYVINYL_ALCOHOL  # scripted group (container) (typed FeaturePython)
  Dunit = g/cm3
  Dvalue = 1.3
  Group = -> [C_element090,H_element082,O_element082]
  conduct = 2
  density = 1
  expand = 3
  formula = G4_POLYVINYL_ALCOHOL
  name = G4_POLYVINYL_ALCOHOL
  specific = 4
FEATURE [App::DocumentObjectGroupPython] C_element091  label="C_element : 049"  # scripted group (container) (typed FeaturePython)
  n = 8
  ref = C_element
FEATURE [App::DocumentObjectGroupPython] H_element083  label="H_element : 045"  # scripted group (container) (typed FeaturePython)
  n = 14
  ref = H_element
FEATURE [App::DocumentObjectGroupPython] O_element083  label="O_element : 044"  # scripted group (container) (typed FeaturePython)
  n = 2
  ref = O_element
FEATURE [App::DocumentObjectGroupPython] G4_POLYVINYL_BUTYRAL  # scripted group (container) (typed FeaturePython)
  Dunit = g/cm3
  Dvalue = 1.12
  Group = -> [C_element091,H_element083,O_element083]
  conduct = 2
  density = 1
  expand = 3
  formula = G4_POLYVINYL_BUTYRAL
  name = G4_POLYVINYL_BUTYRAL
  specific = 4
FEATURE [App::DocumentObjectGroupPython] C_element092  label="C_element : 050"  # scripted group (container) (typed FeaturePython)
  n = 2
  ref = C_element
FEATURE [App::DocumentObjectGroupPython] H_element084  label="H_element : 046"  # scripted group (container) (typed FeaturePython)
  n = 3
  ref = H_element
FEATURE [App::DocumentObjectGroupPython] Cl_element019  label="Cl_element : 009"  # scripted group (container) (typed FeaturePython)
  n = 1
  ref = Cl_element
FEATURE [App::DocumentObjectGroupPython] G4_POLYVINYL_CHLORIDE  # scripted group (container) (typed FeaturePython)
  Dunit = g/cm3
  Dvalue = 1.3
  Group = -> [C_element092,H_element084,Cl_element019]
  conduct = 2
  density = 1
  expand = 3
  formula = G4_POLYVINYL_CHLORIDE
  name = G4_POLYVINYL_CHLORIDE
  specific = 4
FEATURE [App::DocumentObjectGroupPython] C_element093  label="C_element : 051"  # scripted group (container) (typed FeaturePython)
  n = 2
  ref = C_element
FEATURE [App::DocumentObjectGroupPython] H_element085  label="H_element : 047"  # scripted group (container) (typed FeaturePython)
  n = 2
  ref = H_element
FEATURE [App::DocumentObjectGroupPython] Cl_element020  label="Cl_element : 010"  # scripted group (container) (typed FeaturePython)
  n = 2
  ref = Cl_element
FEATURE [App::DocumentObjectGroupPython] G4_POLYVINYLIDENE_CHLORIDE  # scripted group (container) (typed FeaturePython)
  Dunit = g/cm3
  Dvalue = 1.7
  Group = -> [C_element093,H_element085,Cl_element020]
  conduct = 2
  density = 1
  expand = 3
  formula = G4_POLYVINYLIDENE_CHLORIDE
  name = G4_POLYVINYLIDENE_CHLORIDE
  specific = 4
FEATURE [App::DocumentObjectGroupPython] C_element094  label="C_element : 052"  # scripted group (container) (typed FeaturePython)
  n = 2
  ref = C_element
FEATURE [App::DocumentObjectGroupPython] H_element086  label="H_element : 048"  # scripted group (container) (typed FeaturePython)
  n = 2
  ref = H_element
FEATURE [App::DocumentObjectGroupPython] F_element016  label="F_element : 007"  # scripted group (container) (typed FeaturePython)
  n = 2
  ref = F_element
FEATURE [App::DocumentObjectGroupPython] G4_POLYVINYLIDENE_FLUORIDE  # scripted group (container) (typed FeaturePython)
  Dunit = g/cm3
  Dvalue = 1.76
  Group = -> [C_element094,H_element086,F_element016]
  conduct = 2
  density = 1
  expand = 3
  formula = G4_POLYVINYLIDENE_FLUORIDE
  name = G4_POLYVINYLIDENE_FLUORIDE
  specific = 4
FEATURE [App::DocumentObjectGroupPython] C_element095  label="C_element : 053"  # scripted group (container) (typed FeaturePython)
  n = 6
  ref = C_element
FEATURE [App::DocumentObjectGroupPython] H_element087  label="H_element : 9"  # scripted group (container) (typed FeaturePython)
  n = 9
  ref = H_element
FEATURE [App::DocumentObjectGroupPython] N_element037  label="N_element : 016"  # scripted group (container) (typed FeaturePython)
  n = 1
  ref = N_element
FEATURE [App::DocumentObjectGroupPython] O_element084  label="O_element : 045"  # scripted group (container) (typed FeaturePython)
  n = 1
  ref = O_element
FEATURE [App::DocumentObjectGroupPython] G4_POLYVINYL_PYRROLIDONE  # scripted group (container) (typed FeaturePython)
  Dunit = g/cm3
  Dvalue = 1.25
  Group = -> [C_element095,H_element087,N_element037,O_element084]
  conduct = 2
  density = 1
  expand = 3
  formula = G4_POLYVINYL_PYRROLIDONE
  name = G4_POLYVINYL_PYRROLIDONE
  specific = 4
FEATURE [App::DocumentObjectGroupPython] K_element008  label="K_element : 1"  # scripted group (container) (typed FeaturePython)
  n = 1
  ref = K_element
FEATURE [App::DocumentObjectGroupPython] I_element006  label="I_element : 003"  # scripted group (container) (typed FeaturePython)
  n = 1
  ref = I_element
FEATURE [App::DocumentObjectGroupPython] G4_POTASSIUM_IODIDE  # scripted group (container) (typed FeaturePython)
  Dunit = g/cm3
  Dvalue = 3.13
  Group = -> [K_element008,I_element006]
  conduct = 2
  density = 1
  expand = 3
  formula = G4_POTASSIUM_IODIDE
  name = G4_POTASSIUM_IODIDE
  specific = 4
FEATURE [App::DocumentObjectGroupPython] K_element009  label="K_element : 2"  # scripted group (container) (typed FeaturePython)
  n = 2
  ref = K_element
FEATURE [App::DocumentObjectGroupPython] O_element085  label="O_element : 046"  # scripted group (container) (typed FeaturePython)
  n = 1
  ref = O_element
FEATURE [App::DocumentObjectGroupPython] G4_POTASSIUM_OXIDE  # scripted group (container) (typed FeaturePython)
  Dunit = g/cm3
  Dvalue = 2.32
  Group = -> [K_element009,O_element085]
  conduct = 2
  density = 1
  expand = 3
  formula = G4_POTASSIUM_OXIDE
  name = G4_POTASSIUM_OXIDE
  specific = 4
FEATURE [App::DocumentObjectGroupPython] C_element096  label="C_element : 054"  # scripted group (container) (typed FeaturePython)
  n = 3
  ref = C_element
FEATURE [App::DocumentObjectGroupPython] H_element088  label="H_element : 049"  # scripted group (container) (typed FeaturePython)
  n = 8
  ref = H_element
FEATURE [App::DocumentObjectGroupPython] G4_PROPANE  # scripted group (container) (typed FeaturePython)
  Dunit = g/cm3
  Dvalue = 0.00187939
  Group = -> [C_element096,H_element088]
  conduct = 2
  density = 1
  expand = 3
  formula = G4_PROPANE
  name = G4_PROPANE
  specific = 4
FEATURE [App::DocumentObjectGroupPython] C_element097  label="C_element : 055"  # scripted group (container) (typed FeaturePython)
  n = 3
  ref = C_element
FEATURE [App::DocumentObjectGroupPython] H_element089  label="H_element : 050"  # scripted group (container) (typed FeaturePython)
  n = 8
  ref = H_element
FEATURE [App::DocumentObjectGroupPython] G4_lPROPANE  # scripted group (container) (typed FeaturePython)
  Dunit = g/cm3
  Dvalue = 0.43
  Group = -> [C_element097,H_element089]
  conduct = 2
  density = 1
  expand = 3
  formula = G4_lPROPANE
  name = G4_lPROPANE
  specific = 4
FEATURE [App::DocumentObjectGroupPython] C_element098  label="C_element : 056"  # scripted group (container) (typed FeaturePython)
  n = 3
  ref = C_element
FEATURE [App::DocumentObjectGroupPython] H_element090  label="H_element : 051"  # scripted group (container) (typed FeaturePython)
  n = 8
  ref = H_element
FEATURE [App::DocumentObjectGroupPython] O_element086  label="O_element : 047"  # scripted group (container) (typed FeaturePython)
  n = 1
  ref = O_element
FEATURE [App::DocumentObjectGroupPython] G4_N_PROPYL_ALCOHOL  label="G4_N-PROPYL_ALCOHOL"  # scripted group (container) (typed FeaturePython)
  Dunit = g/cm3
  Dvalue = 0.8035
  Group = -> [C_element098,H_element090,O_element086]
  conduct = 2
  density = 1
  expand = 3
  formula = G4_N-PROPYL_ALCOHOL
  name = G4_N-PROPYL_ALCOHOL
  specific = 4
FEATURE [App::DocumentObjectGroupPython] C_element099  label="C_element : 057"  # scripted group (container) (typed FeaturePython)
  n = 5
  ref = C_element
FEATURE [App::DocumentObjectGroupPython] H_element091  label="H_element : 052"  # scripted group (container) (typed FeaturePython)
  n = 5
  ref = H_element
FEATURE [App::DocumentObjectGroupPython] N_element038  label="N_element : 017"  # scripted group (container) (typed FeaturePython)
  n = 1
  ref = N_element
FEATURE [App::DocumentObjectGroupPython] G4_PYRIDINE  # scripted group (container) (typed FeaturePython)
  Dunit = g/cm3
  Dvalue = 0.9819
  Group = -> [C_element099,H_element091,N_element038]
  conduct = 2
  density = 1
  expand = 3
  formula = G4_PYRIDINE
  name = G4_PYRIDINE
  specific = 4
FEATURE [App::DocumentObjectGroupPython] H_element092  label="H_element : 0.144"  # scripted group (container) (typed FeaturePython)
  n = 0.143711
FEATURE [App::DocumentObjectGroupPython] C_element100  label="C_element : 0.856"  # scripted group (container) (typed FeaturePython)
  n = 0.856289
FEATURE [App::DocumentObjectGroupPython] G4_RUBBER_BUTYL  # scripted group (container) (typed FeaturePython)
  Dunit = g/cm3
  Dvalue = 0.92
  Group = -> [H_element092,C_element100]
  conduct = 2
  density = 1
  expand = 3
  formula = G4_RUBBER_BUTYL
  name = G4_RUBBER_BUTYL
  specific = 4
FEATURE [App::DocumentObjectGroupPython] H_element093  label="H_element : 0.118"  # scripted group (container) (typed FeaturePython)
  n = 0.118371
FEATURE [App::DocumentObjectGroupPython] C_element101  label="C_element : 0.882"  # scripted group (container) (typed FeaturePython)
  n = 0.881629
FEATURE [App::DocumentObjectGroupPython] G4_RUBBER_NATURAL  # scripted group (container) (typed FeaturePython)
  Dunit = g/cm3
  Dvalue = 0.92
  Group = -> [H_element093,C_element101]
  conduct = 2
  density = 1
  expand = 3
  formula = G4_RUBBER_NATURAL
  name = G4_RUBBER_NATURAL
  specific = 4
FEATURE [App::DocumentObjectGroupPython] H_element094  label="H_element : 0.145"  # scripted group (container) (typed FeaturePython)
  n = 0.05692
FEATURE [App::DocumentObjectGroupPython] C_element102  label="C_element : 0.543"  # scripted group (container) (typed FeaturePython)
  n = 0.542646
FEATURE [App::DocumentObjectGroupPython] Cl_element021  label="Cl_element : 0.400"  # scripted group (container) (typed FeaturePython)
  n = 0.400434
FEATURE [App::DocumentObjectGroupPython] G4_RUBBER_NEOPRENE  # scripted group (container) (typed FeaturePython)
  Dunit = g/cm3
  Dvalue = 1.23
  Group = -> [H_element094,C_element102,Cl_element021]
  conduct = 2
  density = 1
  expand = 3
  formula = G4_RUBBER_NEOPRENE
  name = G4_RUBBER_NEOPRENE
  specific = 4
FEATURE [App::DocumentObjectGroupPython] Si_element006  label="Si_element : 1"  # scripted group (container) (typed FeaturePython)
  n = 1
  ref = Si_element
FEATURE [App::DocumentObjectGroupPython] O_element087  label="O_element : 048"  # scripted group (container) (typed FeaturePython)
  n = 2
  ref = O_element
FEATURE [App::DocumentObjectGroupPython] G4_SILICON_DIOXIDE  # scripted group (container) (typed FeaturePython)
  Dunit = g/cm3
  Dvalue = 2.32
  Group = -> [Si_element006,O_element087]
  conduct = 2
  density = 1
  expand = 3
  formula = G4_SILICON_DIOXIDE
  name = G4_SILICON_DIOXIDE
  specific = 4
FEATURE [App::DocumentObjectGroupPython] Ag_element002  label="Ag_element : 1"  # scripted group (container) (typed FeaturePython)
  n = 1
  ref = Ag_element
FEATURE [App::DocumentObjectGroupPython] Br_element005  label="Br_element : 003"  # scripted group (container) (typed FeaturePython)
  n = 1
  ref = Br_element
FEATURE [App::DocumentObjectGroupPython] G4_SILVER_BROMIDE  # scripted group (container) (typed FeaturePython)
  Dunit = g/cm3
  Dvalue = 6.473
  Group = -> [Ag_element002,Br_element005]
  conduct = 2
  density = 1
  expand = 3
  formula = G4_SILVER_BROMIDE
  name = G4_SILVER_BROMIDE
  specific = 4
FEATURE [App::DocumentObjectGroupPython] Ag_element003  label="Ag_element : 002"  # scripted group (container) (typed FeaturePython)
  n = 1
  ref = Ag_element
FEATURE [App::DocumentObjectGroupPython] Cl_element022  label="Cl_element : 011"  # scripted group (container) (typed FeaturePython)
  n = 1
  ref = Cl_element
FEATURE [App::DocumentObjectGroupPython] G4_SILVER_CHLORIDE  # scripted group (container) (typed FeaturePython)
  Dunit = g/cm3
  Dvalue = 5.56
  Group = -> [Ag_element003,Cl_element022]
  conduct = 2
  density = 1
  expand = 3
  formula = G4_SILVER_CHLORIDE
  name = G4_SILVER_CHLORIDE
  specific = 4
FEATURE [App::DocumentObjectGroupPython] Br_element006  label="Br_element : 0.423"  # scripted group (container) (typed FeaturePython)
  n = 0.422895
FEATURE [App::DocumentObjectGroupPython] Ag_element004  label="Ag_element : 0.574"  # scripted group (container) (typed FeaturePython)
  n = 0.573748
FEATURE [App::DocumentObjectGroupPython] I_element007  label="I_element : 0.649"  # scripted group (container) (typed FeaturePython)
  n = 0.003357
FEATURE [App::DocumentObjectGroupPython] G4_SILVER_HALIDES  # scripted group (container) (typed FeaturePython)
  Dunit = g/cm3
  Dvalue = 6.47
  Group = -> [Br_element006,Ag_element004,I_element007]
  conduct = 2
  density = 1
  expand = 3
  formula = G4_SILVER_HALIDES
  name = G4_SILVER_HALIDES
  specific = 4
FEATURE [App::DocumentObjectGroupPython] Ag_element005  label="Ag_element : 003"  # scripted group (container) (typed FeaturePython)
  n = 1
  ref = Ag_element
FEATURE [App::DocumentObjectGroupPython] I_element008  label="I_element : 004"  # scripted group (container) (typed FeaturePython)
  n = 1
  ref = I_element
FEATURE [App::DocumentObjectGroupPython] G4_SILVER_IODIDE  # scripted group (container) (typed FeaturePython)
  Dunit = g/cm3
  Dvalue = 6.01
  Group = -> [Ag_element005,I_element008]
  conduct = 2
  density = 1
  expand = 3
  formula = G4_SILVER_IODIDE
  name = G4_SILVER_IODIDE
  specific = 4
FEATURE [App::DocumentObjectGroupPython] H_element095  label="H_element : 0.100"  # scripted group (container) (typed FeaturePython)
  n = 0.1
FEATURE [App::DocumentObjectGroupPython] C_element103  label="C_element : 0.204"  # scripted group (container) (typed FeaturePython)
  n = 0.204
FEATURE [App::DocumentObjectGroupPython] N_element039  label="N_element : 0.759"  # scripted group (container) (typed FeaturePython)
  n = 0.042
FEATURE [App::DocumentObjectGroupPython] O_element088  label="O_element : 0.645"  # scripted group (container) (typed FeaturePython)
  n = 0.645
FEATURE [App::DocumentObjectGroupPython] Na_element013  label="Na_element : 0.100"  # scripted group (container) (typed FeaturePython)
  n = 0.002
FEATURE [App::DocumentObjectGroupPython] P_element009  label="P_element : 0.107"  # scripted group (container) (typed FeaturePython)
  n = 0.001
FEATURE [App::DocumentObjectGroupPython] S_element020  label="S_element : 0.021"  # scripted group (container) (typed FeaturePython)
  n = 0.002
FEATURE [App::DocumentObjectGroupPython] Cl_element023  label="Cl_element : 0.590"  # scripted group (container) (typed FeaturePython)
  n = 0.003
FEATURE [App::DocumentObjectGroupPython] K_element010  label="K_element : 0.001"  # scripted group (container) (typed FeaturePython)
  n = 0.001
FEATURE [App::DocumentObjectGroupPython] G4_SKIN_ICRP  # scripted group (container) (typed FeaturePython)
  Dunit = g/cm3
  Dvalue = 1.09
  Group = -> [H_element095,C_element103,N_element039,O_element088,Na_element013,P_element009,S_element020,Cl_element023,K_element010]
  conduct = 2
  density = 1
  expand = 3
  formula = G4_SKIN_ICRP
  name = G4_SKIN_ICRP
  specific = 4
FEATURE [App::DocumentObjectGroupPython] Na_element014  label="Na_element : 2"  # scripted group (container) (typed FeaturePython)
  n = 2
  ref = Na_element
FEATURE [App::DocumentObjectGroupPython] C_element104  label="C_element : 058"  # scripted group (container) (typed FeaturePython)
  n = 1
  ref = C_element
FEATURE [App::DocumentObjectGroupPython] O_element089  label="O_element : 049"  # scripted group (container) (typed FeaturePython)
  n = 3
  ref = O_element
FEATURE [App::DocumentObjectGroupPython] G4_SODIUM_CARBONATE  # scripted group (container) (typed FeaturePython)
  Dunit = g/cm3
  Dvalue = 2.532
  Group = -> [Na_element014,C_element104,O_element089]
  conduct = 2
  density = 1
  expand = 3
  formula = G4_SODIUM_CARBONATE
  name = G4_SODIUM_CARBONATE
  specific = 4
FEATURE [App::DocumentObjectGroupPython] Na_element015  label="Na_element : 1"  # scripted group (container) (typed FeaturePython)
  n = 1
  ref = Na_element
FEATURE [App::DocumentObjectGroupPython] I_element009  label="I_element : 005"  # scripted group (container) (typed FeaturePython)
  n = 1
  ref = I_element
FEATURE [App::DocumentObjectGroupPython] G4_SODIUM_IODIDE  # scripted group (container) (typed FeaturePython)
  Dunit = g/cm3
  Dvalue = 3.667
  Group = -> [Na_element015,I_element009]
  conduct = 2
  density = 1
  expand = 3
  formula = G4_SODIUM_IODIDE
  name = G4_SODIUM_IODIDE
  specific = 4
FEATURE [App::DocumentObjectGroupPython] Na_element016  label="Na_element : 003"  # scripted group (container) (typed FeaturePython)
  n = 2
  ref = Na_element
FEATURE [App::DocumentObjectGroupPython] O_element090  label="O_element : 050"  # scripted group (container) (typed FeaturePython)
  n = 1
  ref = O_element
FEATURE [App::DocumentObjectGroupPython] G4_SODIUM_MONOXIDE  # scripted group (container) (typed FeaturePython)
  Dunit = g/cm3
  Dvalue = 2.27
  Group = -> [Na_element016,O_element090]
  conduct = 2
  density = 1
  expand = 3
  formula = G4_SODIUM_MONOXIDE
  name = G4_SODIUM_MONOXIDE
  specific = 4
FEATURE [App::DocumentObjectGroupPython] Na_element017  label="Na_element : 004"  # scripted group (container) (typed FeaturePython)
  n = 1
  ref = Na_element
FEATURE [App::DocumentObjectGroupPython] N_element040  label="N_element : 018"  # scripted group (container) (typed FeaturePython)
  n = 1
  ref = N_element
FEATURE [App::DocumentObjectGroupPython] O_element091  label="O_element : 051"  # scripted group (container) (typed FeaturePython)
  n = 3
  ref = O_element
FEATURE [App::DocumentObjectGroupPython] G4_SODIUM_NITRATE  # scripted group (container) (typed FeaturePython)
  Dunit = g/cm3
  Dvalue = 2.261
  Group = -> [Na_element017,N_element040,O_element091]
  conduct = 2
  density = 1
  expand = 3
  formula = G4_SODIUM_NITRATE
  name = G4_SODIUM_NITRATE
  specific = 4
FEATURE [App::DocumentObjectGroupPython] C_element105  label="C_element : 059"  # scripted group (container) (typed FeaturePython)
  n = 14
  ref = C_element
FEATURE [App::DocumentObjectGroupPython] H_element096  label="H_element : 053"  # scripted group (container) (typed FeaturePython)
  n = 12
  ref = H_element
FEATURE [App::DocumentObjectGroupPython] G4_STILBENE  # scripted group (container) (typed FeaturePython)
  Dunit = g/cm3
  Dvalue = 0.9707
  Group = -> [C_element105,H_element096]
  conduct = 2
  density = 1
  expand = 3
  formula = G4_STILBENE
  name = G4_STILBENE
  specific = 4
FEATURE [App::DocumentObjectGroupPython] C_element106  label="C_element : 12"  # scripted group (container) (typed FeaturePython)
  n = 12
  ref = C_element
FEATURE [App::DocumentObjectGroupPython] H_element097  label="H_element : 22"  # scripted group (container) (typed FeaturePython)
  n = 22
  ref = H_element
FEATURE [App::DocumentObjectGroupPython] O_element092  label="O_element : 11"  # scripted group (container) (typed FeaturePython)
  n = 11
  ref = O_element
FEATURE [App::DocumentObjectGroupPython] G4_SUCROSE  # scripted group (container) (typed FeaturePython)
  Dunit = g/cm3
  Dvalue = 1.5805
  Group = -> [C_element106,H_element097,O_element092]
  conduct = 2
  density = 1
  expand = 3
  formula = G4_SUCROSE
  name = G4_SUCROSE
  specific = 4
FEATURE [App::DocumentObjectGroupPython] C_element107  label="C_element : 18"  # scripted group (container) (typed FeaturePython)
  n = 18
  ref = C_element
FEATURE [App::DocumentObjectGroupPython] H_element098  label="H_element : 054"  # scripted group (container) (typed FeaturePython)
  n = 14
  ref = H_element
FEATURE [App::DocumentObjectGroupPython] G4_TERPHENYL  # scripted group (container) (typed FeaturePython)
  Dunit = g/cm3
  Dvalue = 1.24
  Group = -> [C_element107,H_element098]
  conduct = 2
  density = 1
  expand = 3
  formula = G4_TERPHENYL
  name = G4_TERPHENYL
  specific = 4
FEATURE [App::DocumentObjectGroupPython] H_element099  label="H_element : 0.146"  # scripted group (container) (typed FeaturePython)
  n = 0.106
FEATURE [App::DocumentObjectGroupPython] C_element108  label="C_element : 0.883"  # scripted group (container) (typed FeaturePython)
  n = 0.099
FEATURE [App::DocumentObjectGroupPython] N_element041  label="N_element : 0.020"  # scripted group (container) (typed FeaturePython)
  n = 0.02
FEATURE [App::DocumentObjectGroupPython] O_element093  label="O_element : 0.766"  # scripted group (container) (typed FeaturePython)
  n = 0.766
FEATURE [App::DocumentObjectGroupPython] Na_element018  label="Na_element : 0.101"  # scripted group (container) (typed FeaturePython)
  n = 0.002
FEATURE [App::DocumentObjectGroupPython] P_element010  label="P_element : 0.108"  # scripted group (container) (typed FeaturePython)
  n = 0.001
FEATURE [App::DocumentObjectGroupPython] S_element021  label="S_element : 0.022"  # scripted group (container) (typed FeaturePython)
  n = 0.002
FEATURE [App::DocumentObjectGroupPython] Cl_element024  label="Cl_element : 0.002"  # scripted group (container) (typed FeaturePython)
  n = 0.002
FEATURE [App::DocumentObjectGroupPython] K_element011  label="K_element : 0.017"  # scripted group (container) (typed FeaturePython)
  n = 0.002
FEATURE [App::DocumentObjectGroupPython] G4_TESTIS_ICRP  # scripted group (container) (typed FeaturePython)
  Dunit = g/cm3
  Dvalue = 1.04
  Group = -> [H_element099,C_element108,N_element041,O_element093,Na_element018,P_element010,S_element021,Cl_element024,K_element011]
  conduct = 2
  density = 1
  expand = 3
  formula = G4_TESTIS_ICRP
  name = G4_TESTIS_ICRP
  specific = 4
FEATURE [App::DocumentObjectGroupPython] C_element109  label="C_element : 060"  # scripted group (container) (typed FeaturePython)
  n = 2
  ref = C_element
FEATURE [App::DocumentObjectGroupPython] Cl_element025  label="Cl_element : 012"  # scripted group (container) (typed FeaturePython)
  n = 4
  ref = Cl_element
FEATURE [App::DocumentObjectGroupPython] G4_TETRACHLOROETHYLENE  # scripted group (container) (typed FeaturePython)
  Dunit = g/cm3
  Dvalue = 1.625
  Group = -> [C_element109,Cl_element025]
  conduct = 2
  density = 1
  expand = 3
  formula = G4_TETRACHLOROETHYLENE
  name = G4_TETRACHLOROETHYLENE
  specific = 4
FEATURE [App::DocumentObjectGroupPython] Tl_element001  label="Tl_element : 1"  # scripted group (container) (typed FeaturePython)
  n = 1
  ref = Tl_element
FEATURE [App::DocumentObjectGroupPython] Cl_element026  label="Cl_element : 013"  # scripted group (container) (typed FeaturePython)
  n = 1
  ref = Cl_element
FEATURE [App::DocumentObjectGroupPython] G4_THALLIUM_CHLORIDE  # scripted group (container) (typed FeaturePython)
  Dunit = g/cm3
  Dvalue = 7.004
  Group = -> [Tl_element001,Cl_element026]
  conduct = 2
  density = 1
  expand = 3
  formula = G4_THALLIUM_CHLORIDE
  name = G4_THALLIUM_CHLORIDE
  specific = 4
FEATURE [App::DocumentObjectGroupPython] H_element100  label="H_element : 0.147"  # scripted group (container) (typed FeaturePython)
  n = 0.105
FEATURE [App::DocumentObjectGroupPython] C_element110  label="C_element : 0.256"  # scripted group (container) (typed FeaturePython)
  n = 0.256
FEATURE [App::DocumentObjectGroupPython] N_element042  label="N_element : 0.760"  # scripted group (container) (typed FeaturePython)
  n = 0.027
FEATURE [App::DocumentObjectGroupPython] O_element094  label="O_element : 0.602"  # scripted group (container) (typed FeaturePython)
  n = 0.602
FEATURE [App::DocumentObjectGroupPython] Na_element019  label="Na_element : 0.102"  # scripted group (container) (typed FeaturePython)
  n = 0.001
FEATURE [App::DocumentObjectGroupPython] P_element011  label="P_element : 0.109"  # scripted group (container) (typed FeaturePython)
  n = 0.002
FEATURE [App::DocumentObjectGroupPython] S_element022  label="S_element : 0.023"  # scripted group (container) (typed FeaturePython)
  n = 0.003
FEATURE [App::DocumentObjectGroupPython] Cl_element027  label="Cl_element : 0.591"  # scripted group (container) (typed FeaturePython)
  n = 0.002
FEATURE [App::DocumentObjectGroupPython] K_element012  label="K_element : 0.018"  # scripted group (container) (typed FeaturePython)
  n = 0.002
FEATURE [App::DocumentObjectGroupPython] G4_TISSUE_SOFT_ICRP  # scripted group (container) (typed FeaturePython)
  Dunit = g/cm3
  Dvalue = 1.03
  Group = -> [H_element100,C_element110,N_element042,O_element094,Na_element019,P_element011,S_element022,Cl_element027,K_element012]
  conduct = 2
  density = 1
  expand = 3
  formula = G4_TISSUE_SOFT_ICRP
  name = G4_TISSUE_SOFT_ICRP
  specific = 4
FEATURE [App::DocumentObjectGroupPython] H_element101  label="H_element : 0.148"  # scripted group (container) (typed FeaturePython)
  n = 0.101
FEATURE [App::DocumentObjectGroupPython] C_element111  label="C_element : 0.111"  # scripted group (container) (typed FeaturePython)
  n = 0.111
FEATURE [App::DocumentObjectGroupPython] N_element043  label="N_element : 0.026"  # scripted group (container) (typed FeaturePython)
  n = 0.026
FEATURE [App::DocumentObjectGroupPython] O_element095  label="O_element : 0.762"  # scripted group (container) (typed FeaturePython)
  n = 0.762
FEATURE [App::DocumentObjectGroupPython] G4_TISSUE_SOFT_ICRU_4  label="G4_TISSUE_SOFT_ICRU-4"  # scripted group (container) (typed FeaturePython)
  Dunit = g/cm3
  Dvalue = 1
  Group = -> [H_element101,C_element111,N_element043,O_element095]
  conduct = 2
  density = 1
  expand = 3
  formula = G4_TISSUE_SOFT_ICRU-4
  name = G4_TISSUE_SOFT_ICRU-4
  specific = 4
FEATURE [App::DocumentObjectGroupPython] H_element102  label="H_element : 0.149"  # scripted group (container) (typed FeaturePython)
  n = 0.101869
FEATURE [App::DocumentObjectGroupPython] C_element112  label="C_element : 0.456"  # scripted group (container) (typed FeaturePython)
  n = 0.456179
FEATURE [App::DocumentObjectGroupPython] N_element044  label="N_element : 0.761"  # scripted group (container) (typed FeaturePython)
  n = 0.035172
FEATURE [App::DocumentObjectGroupPython] O_element096  label="O_element : 0.407"  # scripted group (container) (typed FeaturePython)
  n = 0.40678
FEATURE [App::DocumentObjectGroupPython] G4_TISSUE_METHANE  label="G4_TISSUE-METHANE"  # scripted group (container) (typed FeaturePython)
  Dunit = g/cm3
  Dvalue = 0.00106409
  Group = -> [H_element102,C_element112,N_element044,O_element096]
  conduct = 2
  density = 1
  expand = 3
  formula = G4_TISSUE-METHANE
  name = G4_TISSUE-METHANE
  specific = 4
FEATURE [App::DocumentObjectGroupPython] H_element103  label="H_element : 0.103"  # scripted group (container) (typed FeaturePython)
  n = 0.102672
FEATURE [App::DocumentObjectGroupPython] C_element113  label="C_element : 0.569"  # scripted group (container) (typed FeaturePython)
  n = 0.56894
FEATURE [App::DocumentObjectGroupPython] N_element045  label="N_element : 0.762"  # scripted group (container) (typed FeaturePython)
  n = 0.035022
FEATURE [App::DocumentObjectGroupPython] O_element097  label="O_element : 0.293"  # scripted group (container) (typed FeaturePython)
  n = 0.293366
FEATURE [App::DocumentObjectGroupPython] G4_TISSUE_PROPANE  label="G4_TISSUE-PROPANE"  # scripted group (container) (typed FeaturePython)
  Dunit = g/cm3
  Dvalue = 0.00182628
  Group = -> [H_element103,C_element113,N_element045,O_element097]
  conduct = 2
  density = 1
  expand = 3
  formula = G4_TISSUE-PROPANE
  name = G4_TISSUE-PROPANE
  specific = 4
FEATURE [App::DocumentObjectGroupPython] Ti_element003  label="Ti_element : 1"  # scripted group (container) (typed FeaturePython)
  n = 1
  ref = Ti_element
FEATURE [App::DocumentObjectGroupPython] O_element098  label="O_element : 052"  # scripted group (container) (typed FeaturePython)
  n = 2
  ref = O_element
FEATURE [App::DocumentObjectGroupPython] G4_TITANIUM_DIOXIDE  # scripted group (container) (typed FeaturePython)
  Dunit = g/cm3
  Dvalue = 4.26
  Group = -> [Ti_element003,O_element098]
  conduct = 2
  density = 1
  expand = 3
  formula = G4_TITANIUM_DIOXIDE
  name = G4_TITANIUM_DIOXIDE
  specific = 4
FEATURE [App::DocumentObjectGroupPython] C_element114  label="C_element : 061"  # scripted group (container) (typed FeaturePython)
  n = 7
  ref = C_element
FEATURE [App::DocumentObjectGroupPython] H_element104  label="H_element : 055"  # scripted group (container) (typed FeaturePython)
  n = 8
  ref = H_element
FEATURE [App::DocumentObjectGroupPython] G4_TOLUENE  # scripted group (container) (typed FeaturePython)
  Dunit = g/cm3
  Dvalue = 0.8669
  Group = -> [C_element114,H_element104]
  conduct = 2
  density = 1
  expand = 3
  formula = G4_TOLUENE
  name = G4_TOLUENE
  specific = 4
FEATURE [App::DocumentObjectGroupPython] C_element115  label="C_element : 062"  # scripted group (container) (typed FeaturePython)
  n = 2
  ref = C_element
FEATURE [App::DocumentObjectGroupPython] H_element105  label="H_element : 056"  # scripted group (container) (typed FeaturePython)
  n = 1
  ref = H_element
FEATURE [App::DocumentObjectGroupPython] Cl_element028  label="Cl_element : 014"  # scripted group (container) (typed FeaturePython)
  n = 3
  ref = Cl_element
FEATURE [App::DocumentObjectGroupPython] G4_TRICHLOROETHYLENE  # scripted group (container) (typed FeaturePython)
  Dunit = g/cm3
  Dvalue = 1.46
  Group = -> [C_element115,H_element105,Cl_element028]
  conduct = 2
  density = 1
  expand = 3
  formula = G4_TRICHLOROETHYLENE
  name = G4_TRICHLOROETHYLENE
  specific = 4
FEATURE [App::DocumentObjectGroupPython] C_element116  label="C_element : 063"  # scripted group (container) (typed FeaturePython)
  n = 6
  ref = C_element
FEATURE [App::DocumentObjectGroupPython] H_element106  label="H_element : 15"  # scripted group (container) (typed FeaturePython)
  n = 15
  ref = H_element
FEATURE [App::DocumentObjectGroupPython] O_element099  label="O_element : 053"  # scripted group (container) (typed FeaturePython)
  n = 4
  ref = O_element
FEATURE [App::DocumentObjectGroupPython] P_element012  label="P_element : 1"  # scripted group (container) (typed FeaturePython)
  n = 1
  ref = P_element
FEATURE [App::DocumentObjectGroupPython] G4_TRIETHYL_PHOSPHATE  # scripted group (container) (typed FeaturePython)
  Dunit = g/cm3
  Dvalue = 1.07
  Group = -> [C_element116,H_element106,O_element099,P_element012]
  conduct = 2
  density = 1
  expand = 3
  formula = G4_TRIETHYL_PHOSPHATE
  name = G4_TRIETHYL_PHOSPHATE
  specific = 4
FEATURE [App::DocumentObjectGroupPython] W_element003  label="W_element : 003"  # scripted group (container) (typed FeaturePython)
  n = 1
  ref = W_element
FEATURE [App::DocumentObjectGroupPython] F_element017  label="F_element : 6"  # scripted group (container) (typed FeaturePython)
  n = 6
  ref = F_element
FEATURE [App::DocumentObjectGroupPython] G4_TUNGSTEN_HEXAFLUORIDE  # scripted group (container) (typed FeaturePython)
  Dunit = g/cm3
  Dvalue = 2.4
  Group = -> [W_element003,F_element017]
  conduct = 2
  density = 1
  expand = 3
  formula = G4_TUNGSTEN_HEXAFLUORIDE
  name = G4_TUNGSTEN_HEXAFLUORIDE
  specific = 4
FEATURE [App::DocumentObjectGroupPython] U_element001  label="U_element : 1"  # scripted group (container) (typed FeaturePython)
  n = 1
  ref = U_element
FEATURE [App::DocumentObjectGroupPython] C_element117  label="C_element : 064"  # scripted group (container) (typed FeaturePython)
  n = 2
  ref = C_element
FEATURE [App::DocumentObjectGroupPython] G4_URANIUM_DICARBIDE  # scripted group (container) (typed FeaturePython)
  Dunit = g/cm3
  Dvalue = 11.28
  Group = -> [U_element001,C_element117]
  conduct = 2
  density = 1
  expand = 3
  formula = G4_URANIUM_DICARBIDE
  name = G4_URANIUM_DICARBIDE
  specific = 4
FEATURE [App::DocumentObjectGroupPython] U_element002  label="U_element : 002"  # scripted group (container) (typed FeaturePython)
  n = 1
  ref = U_element
FEATURE [App::DocumentObjectGroupPython] C_element118  label="C_element : 065"  # scripted group (container) (typed FeaturePython)
  n = 1
  ref = C_element
FEATURE [App::DocumentObjectGroupPython] G4_URANIUM_MONOCARBIDE  # scripted group (container) (typed FeaturePython)
  Dunit = g/cm3
  Dvalue = 13.63
  Group = -> [U_element002,C_element118]
  conduct = 2
  density = 1
  expand = 3
  formula = G4_URANIUM_MONOCARBIDE
  name = G4_URANIUM_MONOCARBIDE
  specific = 4
FEATURE [App::DocumentObjectGroupPython] U_element003  label="U_element : 003"  # scripted group (container) (typed FeaturePython)
  n = 1
  ref = U_element
FEATURE [App::DocumentObjectGroupPython] O_element100  label="O_element : 054"  # scripted group (container) (typed FeaturePython)
  n = 2
  ref = O_element
FEATURE [App::DocumentObjectGroupPython] G4_URANIUM_OXIDE  # scripted group (container) (typed FeaturePython)
  Dunit = g/cm3
  Dvalue = 10.96
  Group = -> [U_element003,O_element100]
  conduct = 2
  density = 1
  expand = 3
  formula = G4_URANIUM_OXIDE
  name = G4_URANIUM_OXIDE
  specific = 4
FEATURE [App::DocumentObjectGroupPython] C_element119  label="C_element : 066"  # scripted group (container) (typed FeaturePython)
  n = 1
  ref = C_element
FEATURE [App::DocumentObjectGroupPython] H_element107  label="H_element : 057"  # scripted group (container) (typed FeaturePython)
  n = 4
  ref = H_element
FEATURE [App::DocumentObjectGroupPython] N_element046  label="N_element : 019"  # scripted group (container) (typed FeaturePython)
  n = 2
  ref = N_element
FEATURE [App::DocumentObjectGroupPython] O_element101  label="O_element : 055"  # scripted group (container) (typed FeaturePython)
  n = 1
  ref = O_element
FEATURE [App::DocumentObjectGroupPython] G4_UREA  # scripted group (container) (typed FeaturePython)
  Dunit = g/cm3
  Dvalue = 1.323
  Group = -> [C_element119,H_element107,N_element046,O_element101]
  conduct = 2
  density = 1
  expand = 3
  formula = G4_UREA
  name = G4_UREA
  specific = 4
FEATURE [App::DocumentObjectGroupPython] C_element120  label="C_element : 067"  # scripted group (container) (typed FeaturePython)
  n = 5
  ref = C_element
FEATURE [App::DocumentObjectGroupPython] H_element108  label="H_element : 058"  # scripted group (container) (typed FeaturePython)
  n = 11
  ref = H_element
FEATURE [App::DocumentObjectGroupPython] N_element047  label="N_element : 020"  # scripted group (container) (typed FeaturePython)
  n = 1
  ref = N_element
FEATURE [App::DocumentObjectGroupPython] O_element102  label="O_element : 056"  # scripted group (container) (typed FeaturePython)
  n = 2
  ref = O_element
FEATURE [App::DocumentObjectGroupPython] G4_VALINE  # scripted group (container) (typed FeaturePython)
  Dunit = g/cm3
  Dvalue = 1.23
  Group = -> [C_element120,H_element108,N_element047,O_element102]
  conduct = 2
  density = 1
  expand = 3
  formula = G4_VALINE
  name = G4_VALINE
  specific = 4
FEATURE [App::DocumentObjectGroupPython] H_element109  label="H_element : 0.009"  # scripted group (container) (typed FeaturePython)
  n = 0.009417
FEATURE [App::DocumentObjectGroupPython] C_element121  label="C_element : 0.281"  # scripted group (container) (typed FeaturePython)
  n = 0.280555
FEATURE [App::DocumentObjectGroupPython] F_element018  label="F_element : 0.710"  # scripted group (container) (typed FeaturePython)
  n = 0.710028
FEATURE [App::DocumentObjectGroupPython] G4_VITON  # scripted group (container) (typed FeaturePython)
  Dunit = g/cm3
  Dvalue = 1.8
  Group = -> [H_element109,C_element121,F_element018]
  conduct = 2
  density = 1
  expand = 3
  formula = G4_VITON
  name = G4_VITON
  specific = 4
FEATURE [App::DocumentObjectGroupPython] H_element110  label="H_element : 059"  # scripted group (container) (typed FeaturePython)
  n = 2
  ref = H_element
FEATURE [App::DocumentObjectGroupPython] O_element103  label="O_element : 057"  # scripted group (container) (typed FeaturePython)
  n = 1
  ref = O_element
FEATURE [App::DocumentObjectGroupPython] G4_WATER  # scripted group (container) (typed FeaturePython)
  Dunit = g/cm3
  Dvalue = 1
  Group = -> [H_element110,O_element103]
  conduct = 2
  density = 1
  expand = 3
  formula = G4_WATER
  name = G4_WATER
  specific = 4
FEATURE [App::DocumentObjectGroupPython] H_element111  label="H_element : 060"  # scripted group (container) (typed FeaturePython)
  n = 2
  ref = H_element
FEATURE [App::DocumentObjectGroupPython] O_element104  label="O_element : 058"  # scripted group (container) (typed FeaturePython)
  n = 1
  ref = O_element
FEATURE [App::DocumentObjectGroupPython] G4_WATER_VAPOR  # scripted group (container) (typed FeaturePython)
  Dunit = g/cm3
  Dvalue = 0.000756182
  Group = -> [H_element111,O_element104]
  conduct = 2
  density = 1
  expand = 3
  formula = G4_WATER_VAPOR
  name = G4_WATER_VAPOR
  specific = 4
FEATURE [App::DocumentObjectGroupPython] C_element122  label="C_element : 068"  # scripted group (container) (typed FeaturePython)
  n = 8
  ref = C_element
FEATURE [App::DocumentObjectGroupPython] H_element112  label="H_element : 061"  # scripted group (container) (typed FeaturePython)
  n = 10
  ref = H_element
FEATURE [App::DocumentObjectGroupPython] G4_XYLENE  # scripted group (container) (typed FeaturePython)
  Dunit = g/cm3
  Dvalue = 0.87
  Group = -> [C_element122,H_element112]
  conduct = 2
  density = 1
  expand = 3
  formula = G4_XYLENE
  name = G4_XYLENE
  specific = 4
FEATURE [App::DocumentObjectGroupPython] C_element123  label="C_element : 069"  # scripted group (container) (typed FeaturePython)
  n = 1
  ref = C_element
FEATURE [App::DocumentObjectGroupPython] G4_GRAPHITE  # scripted group (container) (typed FeaturePython)
  Dunit = g/cm3
  Dvalue = 2.21
  Group = -> [C_element123]
  conduct = 2
  density = 1
  expand = 3
  formula = G4_GRAPHITE
  name = G4_GRAPHITE
  specific = 4
FEATURE [App::DocumentObjectGroupPython] NIST  # scripted group (container) (typed FeaturePython)
  Group = -> [G4_A_150_TISSUE,G4_ACETONE,G4_ACETYLENE,G4_ADENINE,G4_ADIPOSE_TISSUE_ICRP,G4_AIR,G4_ALANINE,G4_ALUMINUM_OXIDE,G4_AMBER,G4_AMMONIA,G4_ANILINE,G4_ANTHRACENE,G4_B_100_BONE,G4_BAKELITE,G4_BARIUM_FLUORIDE,G4_BARIUM_SULFATE,G4_BENZENE,G4_BERYLLIUM_OXIDE,G4_BGO,G4_BLOOD_ICRP,G4_BONE_COMPACT_ICRU,G4_BONE_CORTICAL_ICRP,G4_BORON_CARBIDE,G4_BORON_OXIDE,G4_BRAIN_ICRP,G4_BUTANE,G4_N_BUTYL_ALCOHOL,G4_C_552,+152 more]
FEATURE [App::DocumentObjectGroupPython] H_element113  label="H_element : 062"  # scripted group (container) (typed FeaturePython)
  n = 1
  ref = H_element
FEATURE [App::DocumentObjectGroupPython] G4_H  # scripted group (container) (typed FeaturePython)
  Dunit = g/cm3
  Dvalue = 8.3748e-05
  Group = -> [H_element113]
  conduct = 2
  density = 1
  expand = 3
  formula = H
  name = G4_H
  specific = 4
FEATURE [App::DocumentObjectGroupPython] He_element001  label="He_element : 1"  # scripted group (container) (typed FeaturePython)
  n = 1
  ref = He_element
FEATURE [App::DocumentObjectGroupPython] G4_He  # scripted group (container) (typed FeaturePython)
  Dunit = g/cm3
  Dvalue = 0.000166322
  Group = -> [He_element001]
  conduct = 2
  density = 1
  expand = 3
  formula = He
  name = G4_He
  specific = 4
FEATURE [App::DocumentObjectGroupPython] Li_element008  label="Li_element : 008"  # scripted group (container) (typed FeaturePython)
  n = 1
  ref = Li_element
FEATURE [App::DocumentObjectGroupPython] G4_Li  # scripted group (container) (typed FeaturePython)
  Dunit = g/cm3
  Dvalue = 0.534
  Group = -> [Li_element008]
  conduct = 2
  density = 1
  expand = 3
  formula = Li
  name = G4_Li
  specific = 4
FEATURE [App::DocumentObjectGroupPython] Be_element002  label="Be_element : 002"  # scripted group (container) (typed FeaturePython)
  n = 1
  ref = Be_element
FEATURE [App::DocumentObjectGroupPython] G4_Be  # scripted group (container) (typed FeaturePython)
  Dunit = g/cm3
  Dvalue = 1.848
  Group = -> [Be_element002]
  conduct = 2
  density = 1
  expand = 3
  formula = Be
  name = G4_Be
  specific = 4
FEATURE [App::DocumentObjectGroupPython] B_element007  label="B_element : 007"  # scripted group (container) (typed FeaturePython)
  n = 1
  ref = B_element
FEATURE [App::DocumentObjectGroupPython] G4_B  # scripted group (container) (typed FeaturePython)
  Dunit = g/cm3
  Dvalue = 2.37
  Group = -> [B_element007]
  conduct = 2
  density = 1
  expand = 3
  formula = B
  name = G4_B
  specific = 4
FEATURE [App::DocumentObjectGroupPython] C_element124  label="C_element : 070"  # scripted group (container) (typed FeaturePython)
  n = 1
  ref = C_element
FEATURE [App::DocumentObjectGroupPython] G4_C  # scripted group (container) (typed FeaturePython)
  Dunit = g/cm3
  Dvalue = 2
  Group = -> [C_element124]
  conduct = 2
  density = 1
  expand = 3
  formula = C
  name = G4_C
  specific = 4
FEATURE [App::DocumentObjectGroupPython] N_element048  label="N_element : 021"  # scripted group (container) (typed FeaturePython)
  n = 1
  ref = N_element
FEATURE [App::DocumentObjectGroupPython] G4_N  # scripted group (container) (typed FeaturePython)
  Dunit = g/cm3
  Dvalue = 0.0011652
  Group = -> [N_element048]
  conduct = 2
  density = 1
  expand = 3
  formula = N
  name = G4_N
  specific = 4
FEATURE [App::DocumentObjectGroupPython] O_element105  label="O_element : 059"  # scripted group (container) (typed FeaturePython)
  n = 1
  ref = O_element
FEATURE [App::DocumentObjectGroupPython] G4_O  # scripted group (container) (typed FeaturePython)
  Dunit = g/cm3
  Dvalue = 0.00133151
  Group = -> [O_element105]
  conduct = 2
  density = 1
  expand = 3
  formula = O
  name = G4_O
  specific = 4
FEATURE [App::DocumentObjectGroupPython] F_element019  label="F_element : 008"  # scripted group (container) (typed FeaturePython)
  n = 1
  ref = F_element
FEATURE [App::DocumentObjectGroupPython] G4_F  # scripted group (container) (typed FeaturePython)
  Dunit = g/cm3
  Dvalue = 0.00158029
  Group = -> [F_element019]
  conduct = 2
  density = 1
  expand = 3
  formula = F
  name = G4_F
  specific = 4
FEATURE [App::DocumentObjectGroupPython] Ne_element001  label="Ne_element : 1"  # scripted group (container) (typed FeaturePython)
  n = 1
  ref = Ne_element
FEATURE [App::DocumentObjectGroupPython] G4_Ne  # scripted group (container) (typed FeaturePython)
  Dunit = g/cm3
  Dvalue = 0.000838505
  Group = -> [Ne_element001]
  conduct = 2
  density = 1
  expand = 3
  formula = Ne
  name = G4_Ne
  specific = 4
FEATURE [App::DocumentObjectGroupPython] Na_element020  label="Na_element : 005"  # scripted group (container) (typed FeaturePython)
  n = 1
  ref = Na_element
FEATURE [App::DocumentObjectGroupPython] G4_Na  # scripted group (container) (typed FeaturePython)
  Dunit = g/cm3
  Dvalue = 0.971
  Group = -> [Na_element020]
  conduct = 2
  density = 1
  expand = 3
  formula = Na
  name = G4_Na
  specific = 4
FEATURE [App::DocumentObjectGroupPython] Mg_element011  label="Mg_element : 005"  # scripted group (container) (typed FeaturePython)
  n = 1
  ref = Mg_element
FEATURE [App::DocumentObjectGroupPython] G4_Mg  # scripted group (container) (typed FeaturePython)
  Dunit = g/cm3
  Dvalue = 1.74
  Group = -> [Mg_element011]
  conduct = 2
  density = 1
  expand = 3
  formula = Mg
  name = G4_Mg
  specific = 4
FEATURE [App::DocumentObjectGroupPython] Al_element004  label="Al_element : 1"  # scripted group (container) (typed FeaturePython)
  n = 1
  ref = Al_element
FEATURE [App::DocumentObjectGroupPython] G4_Al  # scripted group (container) (typed FeaturePython)
  Dunit = g/cm3
  Dvalue = 2.699
  Group = -> [Al_element004]
  conduct = 2
  density = 1
  expand = 3
  formula = Al
  name = G4_Al
  specific = 4
FEATURE [App::DocumentObjectGroupPython] Si_element007  label="Si_element : 002"  # scripted group (container) (typed FeaturePython)
  n = 1
  ref = Si_element
FEATURE [App::DocumentObjectGroupPython] G4_Si  # scripted group (container) (typed FeaturePython)
  Dunit = g/cm3
  Dvalue = 2.33
  Group = -> [Si_element007]
  conduct = 2
  density = 1
  expand = 3
  formula = Si
  name = G4_Si
  specific = 4
FEATURE [App::DocumentObjectGroupPython] P_element013  label="P_element : 002"  # scripted group (container) (typed FeaturePython)
  n = 1
  ref = P_element
FEATURE [App::DocumentObjectGroupPython] G4_P  # scripted group (container) (typed FeaturePython)
  Dunit = g/cm3
  Dvalue = 2.2
  Group = -> [P_element013]
  conduct = 2
  density = 1
  expand = 3
  formula = P
  name = G4_P
  specific = 4
FEATURE [App::DocumentObjectGroupPython] S_element023  label="S_element : 007"  # scripted group (container) (typed FeaturePython)
  n = 1
  ref = S_element
FEATURE [App::DocumentObjectGroupPython] G4_S  # scripted group (container) (typed FeaturePython)
  Dunit = g/cm3
  Dvalue = 2
  Group = -> [S_element023]
  conduct = 2
  density = 1
  expand = 3
  formula = S
  name = G4_S
  specific = 4
FEATURE [App::DocumentObjectGroupPython] Cl_element029  label="Cl_element : 015"  # scripted group (container) (typed FeaturePython)
  n = 1
  ref = Cl_element
FEATURE [App::DocumentObjectGroupPython] G4_Cl  # scripted group (container) (typed FeaturePython)
  Dunit = g/cm3
  Dvalue = 0.00299473
  Group = -> [Cl_element029]
  conduct = 2
  density = 1
  expand = 3
  formula = Cl
  name = G4_Cl
  specific = 4
FEATURE [App::DocumentObjectGroupPython] Ar_element002  label="Ar_element : 1"  # scripted group (container) (typed FeaturePython)
  n = 1
  ref = Ar_element
FEATURE [App::DocumentObjectGroupPython] G4_Ar  # scripted group (container) (typed FeaturePython)
  Dunit = g/cm3
  Dvalue = 0.00166201
  Group = -> [Ar_element002]
  conduct = 2
  density = 1
  expand = 3
  formula = Ar
  name = G4_Ar
  specific = 4
FEATURE [App::DocumentObjectGroupPython] K_element013  label="K_element : 003"  # scripted group (container) (typed FeaturePython)
  n = 1
  ref = K_element
FEATURE [App::DocumentObjectGroupPython] G4_K  # scripted group (container) (typed FeaturePython)
  Dunit = g/cm3
  Dvalue = 0.862
  Group = -> [K_element013]
  conduct = 2
  density = 1
  expand = 3
  formula = K
  name = G4_K
  specific = 4
FEATURE [App::DocumentObjectGroupPython] Ca_element014  label="Ca_element : 007"  # scripted group (container) (typed FeaturePython)
  n = 1
  ref = Ca_element
FEATURE [App::DocumentObjectGroupPython] G4_Ca  # scripted group (container) (typed FeaturePython)
  Dunit = g/cm3
  Dvalue = 1.55
  Group = -> [Ca_element014]
  conduct = 2
  density = 1
  expand = 3
  formula = Ca
  name = G4_Ca
  specific = 4
FEATURE [App::DocumentObjectGroupPython] Sc_element001  label="Sc_element : 1"  # scripted group (container) (typed FeaturePython)
  n = 1
  ref = Sc_element
FEATURE [App::DocumentObjectGroupPython] G4_Sc  # scripted group (container) (typed FeaturePython)
  Dunit = g/cm3
  Dvalue = 2.989
  Group = -> [Sc_element001]
  conduct = 2
  density = 1
  expand = 3
  formula = Sc
  name = G4_Sc
  specific = 4
FEATURE [App::DocumentObjectGroupPython] Ti_element004  label="Ti_element : 002"  # scripted group (container) (typed FeaturePython)
  n = 1
  ref = Ti_element
FEATURE [App::DocumentObjectGroupPython] G4_Ti  # scripted group (container) (typed FeaturePython)
  Dunit = g/cm3
  Dvalue = 4.54
  Group = -> [Ti_element004]
  conduct = 2
  density = 1
  expand = 3
  formula = Ti
  name = G4_Ti
  specific = 4
FEATURE [App::DocumentObjectGroupPython] V_element001  label="V_element : 1"  # scripted group (container) (typed FeaturePython)
  n = 1
  ref = V_element
FEATURE [App::DocumentObjectGroupPython] G4_V  # scripted group (container) (typed FeaturePython)
  Dunit = g/cm3
  Dvalue = 6.11
  Group = -> [V_element001]
  conduct = 2
  density = 1
  expand = 3
  formula = V
  name = G4_V
  specific = 4
FEATURE [App::DocumentObjectGroupPython] Cr_element001  label="Cr_element : 1"  # scripted group (container) (typed FeaturePython)
  n = 1
  ref = Cr_element
FEATURE [App::DocumentObjectGroupPython] G4_Cr  # scripted group (container) (typed FeaturePython)
  Dunit = g/cm3
  Dvalue = 7.18
  Group = -> [Cr_element001]
  conduct = 2
  density = 1
  expand = 3
  formula = Cr
  name = G4_Cr
  specific = 4
FEATURE [App::DocumentObjectGroupPython] Mn_element001  label="Mn_element : 1"  # scripted group (container) (typed FeaturePython)
  n = 1
  ref = Mn_element
FEATURE [App::DocumentObjectGroupPython] G4_Mn  # scripted group (container) (typed FeaturePython)
  Dunit = g/cm3
  Dvalue = 7.44
  Group = -> [Mn_element001]
  conduct = 2
  density = 1
  expand = 3
  formula = Mn
  name = G4_Mn
  specific = 4
FEATURE [App::DocumentObjectGroupPython] Fe_element007  label="Fe_element : 004"  # scripted group (container) (typed FeaturePython)
  n = 1
  ref = Fe_element
FEATURE [App::DocumentObjectGroupPython] G4_Fe  # scripted group (container) (typed FeaturePython)
  Dunit = g/cm3
  Dvalue = 7.874
  Group = -> [Fe_element007]
  conduct = 2
  density = 1
  expand = 3
  formula = Fe
  name = G4_Fe
  specific = 4
FEATURE [App::DocumentObjectGroupPython] Co_element001  label="Co_element : 1"  # scripted group (container) (typed FeaturePython)
  n = 1
  ref = Co_element
FEATURE [App::DocumentObjectGroupPython] G4_Co  # scripted group (container) (typed FeaturePython)
  Dunit = g/cm3
  Dvalue = 8.9
  Group = -> [Co_element001]
  conduct = 2
  density = 1
  expand = 3
  formula = Co
  name = G4_Co
  specific = 4
FEATURE [App::DocumentObjectGroupPython] Ni_element001  label="Ni_element : 1"  # scripted group (container) (typed FeaturePython)
  n = 1
  ref = Ni_element
FEATURE [App::DocumentObjectGroupPython] G4_Ni  # scripted group (container) (typed FeaturePython)
  Dunit = g/cm3
  Dvalue = 8.902
  Group = -> [Ni_element001]
  conduct = 2
  density = 1
  expand = 3
  formula = Ni
  name = G4_Ni
  specific = 4
FEATURE [App::DocumentObjectGroupPython] Cu_element001  label="Cu_element : 1"  # scripted group (container) (typed FeaturePython)
  n = 1
  ref = Cu_element
FEATURE [App::DocumentObjectGroupPython] G4_Cu  # scripted group (container) (typed FeaturePython)
  Dunit = g/cm3
  Dvalue = 8.96
  Group = -> [Cu_element001]
  conduct = 2
  density = 1
  expand = 3
  formula = Cu
  name = G4_Cu
  specific = 4
FEATURE [App::DocumentObjectGroupPython] Zn_element001  label="Zn_element : 1"  # scripted group (container) (typed FeaturePython)
  n = 1
  ref = Zn_element
FEATURE [App::DocumentObjectGroupPython] G4_Zn  # scripted group (container) (typed FeaturePython)
  Dunit = g/cm3
  Dvalue = 7.133
  Group = -> [Zn_element001]
  conduct = 2
  density = 1
  expand = 3
  formula = Zn
  name = G4_Zn
  specific = 4
FEATURE [App::DocumentObjectGroupPython] Ga_element002  label="Ga_element : 002"  # scripted group (container) (typed FeaturePython)
  n = 1
  ref = Ga_element
FEATURE [App::DocumentObjectGroupPython] G4_Ga  # scripted group (container) (typed FeaturePython)
  Dunit = g/cm3
  Dvalue = 5.904
  Group = -> [Ga_element002]
  conduct = 2
  density = 1
  expand = 3
  formula = Ga
  name = G4_Ga
  specific = 4
FEATURE [App::DocumentObjectGroupPython] Ge_element002  label="Ge_element : 1"  # scripted group (container) (typed FeaturePython)
  n = 1
  ref = Ge_element
FEATURE [App::DocumentObjectGroupPython] G4_Ge  # scripted group (container) (typed FeaturePython)
  Dunit = g/cm3
  Dvalue = 5.323
  Group = -> [Ge_element002]
  conduct = 2
  density = 1
  expand = 3
  formula = Ge
  name = G4_Ge
  specific = 4
FEATURE [App::DocumentObjectGroupPython] As_element003  label="As_element : 002"  # scripted group (container) (typed FeaturePython)
  n = 1
  ref = As_element
FEATURE [App::DocumentObjectGroupPython] G4_As  # scripted group (container) (typed FeaturePython)
  Dunit = g/cm3
  Dvalue = 5.73
  Group = -> [As_element003]
  conduct = 2
  density = 1
  expand = 3
  formula = As
  name = G4_As
  specific = 4
FEATURE [App::DocumentObjectGroupPython] Se_element001  label="Se_element : 1"  # scripted group (container) (typed FeaturePython)
  n = 1
  ref = Se_element
FEATURE [App::DocumentObjectGroupPython] G4_Se  # scripted group (container) (typed FeaturePython)
  Dunit = g/cm3
  Dvalue = 4.5
  Group = -> [Se_element001]
  conduct = 2
  density = 1
  expand = 3
  formula = Se
  name = G4_Se
  specific = 4
FEATURE [App::DocumentObjectGroupPython] Br_element007  label="Br_element : 004"  # scripted group (container) (typed FeaturePython)
  n = 1
  ref = Br_element
FEATURE [App::DocumentObjectGroupPython] G4_Br  # scripted group (container) (typed FeaturePython)
  Dunit = g/cm3
  Dvalue = 0.0070721
  Group = -> [Br_element007]
  conduct = 2
  density = 1
  expand = 3
  formula = Br
  name = G4_Br
  specific = 4
FEATURE [App::DocumentObjectGroupPython] Kr_element001  label="Kr_element : 1"  # scripted group (container) (typed FeaturePython)
  n = 1
  ref = Kr_element
FEATURE [App::DocumentObjectGroupPython] G4_Kr  # scripted group (container) (typed FeaturePython)
  Dunit = g/cm3
  Dvalue = 0.00347832
  Group = -> [Kr_element001]
  conduct = 2
  density = 1
  expand = 3
  formula = Kr
  name = G4_Kr
  specific = 4
FEATURE [App::DocumentObjectGroupPython] Rb_element001  label="Rb_element : 1"  # scripted group (container) (typed FeaturePython)
  n = 1
  ref = Rb_element
FEATURE [App::DocumentObjectGroupPython] G4_Rb  # scripted group (container) (typed FeaturePython)
  Dunit = g/cm3
  Dvalue = 1.532
  Group = -> [Rb_element001]
  conduct = 2
  density = 1
  expand = 3
  formula = Rb
  name = G4_Rb
  specific = 4
FEATURE [App::DocumentObjectGroupPython] Sr_element001  label="Sr_element : 1"  # scripted group (container) (typed FeaturePython)
  n = 1
  ref = Sr_element
FEATURE [App::DocumentObjectGroupPython] G4_Sr  # scripted group (container) (typed FeaturePython)
  Dunit = g/cm3
  Dvalue = 2.54
  Group = -> [Sr_element001]
  conduct = 2
  density = 1
  expand = 3
  formula = Sr
  name = G4_Sr
  specific = 4
FEATURE [App::DocumentObjectGroupPython] Y_element001  label="Y_element : 1"  # scripted group (container) (typed FeaturePython)
  n = 1
  ref = Y_element
FEATURE [App::DocumentObjectGroupPython] G4_Y  # scripted group (container) (typed FeaturePython)
  Dunit = g/cm3
  Dvalue = 4.469
  Group = -> [Y_element001]
  conduct = 2
  density = 1
  expand = 3
  formula = Y
  name = G4_Y
  specific = 4
FEATURE [App::DocumentObjectGroupPython] Zr_element001  label="Zr_element : 1"  # scripted group (container) (typed FeaturePython)
  n = 1
  ref = Zr_element
FEATURE [App::DocumentObjectGroupPython] G4_Zr  # scripted group (container) (typed FeaturePython)
  Dunit = g/cm3
  Dvalue = 6.506
  Group = -> [Zr_element001]
  conduct = 2
  density = 1
  expand = 3
  formula = Zr
  name = G4_Zr
  specific = 4
FEATURE [App::DocumentObjectGroupPython] Nb_element001  label="Nb_element : 1"  # scripted group (container) (typed FeaturePython)
  n = 1
  ref = Nb_element
FEATURE [App::DocumentObjectGroupPython] G4_Nb  # scripted group (container) (typed FeaturePython)
  Dunit = g/cm3
  Dvalue = 8.57
  Group = -> [Nb_element001]
  conduct = 2
  density = 1
  expand = 3
  formula = Nb
  name = G4_Nb
  specific = 4
FEATURE [App::DocumentObjectGroupPython] Mo_element001  label="Mo_element : 1"  # scripted group (container) (typed FeaturePython)
  n = 1
  ref = Mo_element
FEATURE [App::DocumentObjectGroupPython] G4_Mo  # scripted group (container) (typed FeaturePython)
  Dunit = g/cm3
  Dvalue = 10.22
  Group = -> [Mo_element001]
  conduct = 2
  density = 1
  expand = 3
  formula = Mo
  name = G4_Mo
  specific = 4
FEATURE [App::DocumentObjectGroupPython] Tc_element001  label="Tc_element : 1"  # scripted group (container) (typed FeaturePython)
  n = 1
  ref = Tc_element
FEATURE [App::DocumentObjectGroupPython] G4_Tc  # scripted group (container) (typed FeaturePython)
  Dunit = g/cm3
  Dvalue = 11.5
  Group = -> [Tc_element001]
  conduct = 2
  density = 1
  expand = 3
  formula = Tc
  name = G4_Tc
  specific = 4
FEATURE [App::DocumentObjectGroupPython] Ru_element001  label="Ru_element : 1"  # scripted group (container) (typed FeaturePython)
  n = 1
  ref = Ru_element
FEATURE [App::DocumentObjectGroupPython] G4_Ru  # scripted group (container) (typed FeaturePython)
  Dunit = g/cm3
  Dvalue = 12.41
  Group = -> [Ru_element001]
  conduct = 2
  density = 1
  expand = 3
  formula = Ru
  name = G4_Ru
  specific = 4
FEATURE [App::DocumentObjectGroupPython] Rh_element001  label="Rh_element : 1"  # scripted group (container) (typed FeaturePython)
  n = 1
  ref = Rh_element
FEATURE [App::DocumentObjectGroupPython] G4_Rh  # scripted group (container) (typed FeaturePython)
  Dunit = g/cm3
  Dvalue = 12.41
  Group = -> [Rh_element001]
  conduct = 2
  density = 1
  expand = 3
  formula = Rh
  name = G4_Rh
  specific = 4
FEATURE [App::DocumentObjectGroupPython] Pd_element001  label="Pd_element : 1"  # scripted group (container) (typed FeaturePython)
  n = 1
  ref = Pd_element
FEATURE [App::DocumentObjectGroupPython] G4_Pd  # scripted group (container) (typed FeaturePython)
  Dunit = g/cm3
  Dvalue = 12.02
  Group = -> [Pd_element001]
  conduct = 2
  density = 1
  expand = 3
  formula = Pd
  name = G4_Pd
  specific = 4
FEATURE [App::DocumentObjectGroupPython] Ag_element006  label="Ag_element : 004"  # scripted group (container) (typed FeaturePython)
  n = 1
  ref = Ag_element
FEATURE [App::DocumentObjectGroupPython] G4_Ag  # scripted group (container) (typed FeaturePython)
  Dunit = g/cm3
  Dvalue = 10.5
  Group = -> [Ag_element006]
  conduct = 2
  density = 1
  expand = 3
  formula = Ag
  name = G4_Ag
  specific = 4
FEATURE [App::DocumentObjectGroupPython] Cd_element003  label="Cd_element : 003"  # scripted group (container) (typed FeaturePython)
  n = 1
  ref = Cd_element
FEATURE [App::DocumentObjectGroupPython] G4_Cd  # scripted group (container) (typed FeaturePython)
  Dunit = g/cm3
  Dvalue = 8.65
  Group = -> [Cd_element003]
  conduct = 2
  density = 1
  expand = 3
  formula = Cd
  name = G4_Cd
  specific = 4
FEATURE [App::DocumentObjectGroupPython] In_element001  label="In_element : 1"  # scripted group (container) (typed FeaturePython)
  n = 1
  ref = In_element
FEATURE [App::DocumentObjectGroupPython] G4_In  # scripted group (container) (typed FeaturePython)
  Dunit = g/cm3
  Dvalue = 7.31
  Group = -> [In_element001]
  conduct = 2
  density = 1
  expand = 3
  formula = In
  name = G4_In
  specific = 4
FEATURE [App::DocumentObjectGroupPython] Sn_element001  label="Sn_element : 1"  # scripted group (container) (typed FeaturePython)
  n = 1
  ref = Sn_element
FEATURE [App::DocumentObjectGroupPython] G4_Sn  # scripted group (container) (typed FeaturePython)
  Dunit = g/cm3
  Dvalue = 7.31
  Group = -> [Sn_element001]
  conduct = 2
  density = 1
  expand = 3
  formula = Sn
  name = G4_Sn
  specific = 4
FEATURE [App::DocumentObjectGroupPython] Sb_element001  label="Sb_element : 1"  # scripted group (container) (typed FeaturePython)
  n = 1
  ref = Sb_element
FEATURE [App::DocumentObjectGroupPython] G4_Sb  # scripted group (container) (typed FeaturePython)
  Dunit = g/cm3
  Dvalue = 6.691
  Group = -> [Sb_element001]
  conduct = 2
  density = 1
  expand = 3
  formula = Sb
  name = G4_Sb
  specific = 4
FEATURE [App::DocumentObjectGroupPython] Te_element002  label="Te_element : 002"  # scripted group (container) (typed FeaturePython)
  n = 1
  ref = Te_element
FEATURE [App::DocumentObjectGroupPython] G4_Te  # scripted group (container) (typed FeaturePython)
  Dunit = g/cm3
  Dvalue = 6.24
  Group = -> [Te_element002]
  conduct = 2
  density = 1
  expand = 3
  formula = Te
  name = G4_Te
  specific = 4
FEATURE [App::DocumentObjectGroupPython] I_element010  label="I_element : 006"  # scripted group (container) (typed FeaturePython)
  n = 1
  ref = I_element
FEATURE [App::DocumentObjectGroupPython] G4_I  # scripted group (container) (typed FeaturePython)
  Dunit = g/cm3
  Dvalue = 4.93
  Group = -> [I_element010]
  conduct = 2
  density = 1
  expand = 3
  formula = I
  name = G4_I
  specific = 4
FEATURE [App::DocumentObjectGroupPython] Xe_element001  label="Xe_element : 1"  # scripted group (container) (typed FeaturePython)
  n = 1
  ref = Xe_element
FEATURE [App::DocumentObjectGroupPython] G4_Xe  # scripted group (container) (typed FeaturePython)
  Dunit = g/cm3
  Dvalue = 0.00548536
  Group = -> [Xe_element001]
  conduct = 2
  density = 1
  expand = 3
  formula = Xe
  name = G4_Xe
  specific = 4
FEATURE [App::DocumentObjectGroupPython] Cs_element003  label="Cs_element : 003"  # scripted group (container) (typed FeaturePython)
  n = 1
  ref = Cs_element
FEATURE [App::DocumentObjectGroupPython] G4_Cs  # scripted group (container) (typed FeaturePython)
  Dunit = g/cm3
  Dvalue = 1.873
  Group = -> [Cs_element003]
  conduct = 2
  density = 1
  expand = 3
  formula = Cs
  name = G4_Cs
  specific = 4
FEATURE [App::DocumentObjectGroupPython] Ba_element003  label="Ba_element : 003"  # scripted group (container) (typed FeaturePython)
  n = 1
  ref = Ba_element
FEATURE [App::DocumentObjectGroupPython] G4_Ba  # scripted group (container) (typed FeaturePython)
  Dunit = g/cm3
  Dvalue = 3.5
  Group = -> [Ba_element003]
  conduct = 2
  density = 1
  expand = 3
  formula = Ba
  name = G4_Ba
  specific = 4
FEATURE [App::DocumentObjectGroupPython] La_element003  label="La_element : 003"  # scripted group (container) (typed FeaturePython)
  n = 1
  ref = La_element
FEATURE [App::DocumentObjectGroupPython] G4_La  # scripted group (container) (typed FeaturePython)
  Dunit = g/cm3
  Dvalue = 6.154
  Group = -> [La_element003]
  conduct = 2
  density = 1
  expand = 3
  formula = La
  name = G4_La
  specific = 4
FEATURE [App::DocumentObjectGroupPython] Ce_element002  label="Ce_element : 1"  # scripted group (container) (typed FeaturePython)
  n = 1
  ref = Ce_element
FEATURE [App::DocumentObjectGroupPython] G4_Ce  # scripted group (container) (typed FeaturePython)
  Dunit = g/cm3
  Dvalue = 6.657
  Group = -> [Ce_element002]
  conduct = 2
  density = 1
  expand = 3
  formula = Ce
  name = G4_Ce
  specific = 4
FEATURE [App::DocumentObjectGroupPython] Pr_element001  label="Pr_element : 1"  # scripted group (container) (typed FeaturePython)
  n = 1
  ref = Pr_element
FEATURE [App::DocumentObjectGroupPython] G4_Pr  # scripted group (container) (typed FeaturePython)
  Dunit = g/cm3
  Dvalue = 6.71
  Group = -> [Pr_element001]
  conduct = 2
  density = 1
  expand = 3
  formula = Pr
  name = G4_Pr
  specific = 4
FEATURE [App::DocumentObjectGroupPython] Nd_element001  label="Nd_element : 1"  # scripted group (container) (typed FeaturePython)
  n = 1
  ref = Nd_element
FEATURE [App::DocumentObjectGroupPython] G4_Nd  # scripted group (container) (typed FeaturePython)
  Dunit = g/cm3
  Dvalue = 6.9
  Group = -> [Nd_element001]
  conduct = 2
  density = 1
  expand = 3
  formula = Nd
  name = G4_Nd
  specific = 4
FEATURE [App::DocumentObjectGroupPython] Pm_element001  label="Pm_element : 1"  # scripted group (container) (typed FeaturePython)
  n = 1
  ref = Pm_element
FEATURE [App::DocumentObjectGroupPython] G4_Pm  # scripted group (container) (typed FeaturePython)
  Dunit = g/cm3
  Dvalue = 7.22
  Group = -> [Pm_element001]
  conduct = 2
  density = 1
  expand = 3
  formula = Pm
  name = G4_Pm
  specific = 4
FEATURE [App::DocumentObjectGroupPython] Sm_element001  label="Sm_element : 1"  # scripted group (container) (typed FeaturePython)
  n = 1
  ref = Sm_element
FEATURE [App::DocumentObjectGroupPython] G4_Sm  # scripted group (container) (typed FeaturePython)
  Dunit = g/cm3
  Dvalue = 7.46
  Group = -> [Sm_element001]
  conduct = 2
  density = 1
  expand = 3
  formula = Sm
  name = G4_Sm
  specific = 4
FEATURE [App::DocumentObjectGroupPython] Eu_element001  label="Eu_element : 1"  # scripted group (container) (typed FeaturePython)
  n = 1
  ref = Eu_element
FEATURE [App::DocumentObjectGroupPython] G4_Eu  # scripted group (container) (typed FeaturePython)
  Dunit = g/cm3
  Dvalue = 5.243
  Group = -> [Eu_element001]
  conduct = 2
  density = 1
  expand = 3
  formula = Eu
  name = G4_Eu
  specific = 4
FEATURE [App::DocumentObjectGroupPython] Gd_element002  label="Gd_element : 1"  # scripted group (container) (typed FeaturePython)
  n = 1
  ref = Gd_element
FEATURE [App::DocumentObjectGroupPython] G4_Gd  # scripted group (container) (typed FeaturePython)
  Dunit = g/cm3
  Dvalue = 7.9004
  Group = -> [Gd_element002]
  conduct = 2
  density = 1
  expand = 3
  formula = Gd
  name = G4_Gd
  specific = 4
FEATURE [App::DocumentObjectGroupPython] Tb_element001  label="Tb_element : 1"  # scripted group (container) (typed FeaturePython)
  n = 1
  ref = Tb_element
FEATURE [App::DocumentObjectGroupPython] G4_Tb  # scripted group (container) (typed FeaturePython)
  Dunit = g/cm3
  Dvalue = 8.229
  Group = -> [Tb_element001]
  conduct = 2
  density = 1
  expand = 3
  formula = Tb
  name = G4_Tb
  specific = 4
FEATURE [App::DocumentObjectGroupPython] Dy_element001  label="Dy_element : 1"  # scripted group (container) (typed FeaturePython)
  n = 1
  ref = Dy_element
FEATURE [App::DocumentObjectGroupPython] G4_Dy  # scripted group (container) (typed FeaturePython)
  Dunit = g/cm3
  Dvalue = 8.55
  Group = -> [Dy_element001]
  conduct = 2
  density = 1
  expand = 3
  formula = Dy
  name = G4_Dy
  specific = 4
FEATURE [App::DocumentObjectGroupPython] Ho_element001  label="Ho_element : 1"  # scripted group (container) (typed FeaturePython)
  n = 1
  ref = Ho_element
FEATURE [App::DocumentObjectGroupPython] G4_Ho  # scripted group (container) (typed FeaturePython)
  Dunit = g/cm3
  Dvalue = 8.795
  Group = -> [Ho_element001]
  conduct = 2
  density = 1
  expand = 3
  formula = Ho
  name = G4_Ho
  specific = 4
FEATURE [App::DocumentObjectGroupPython] Er_element001  label="Er_element : 1"  # scripted group (container) (typed FeaturePython)
  n = 1
  ref = Er_element
FEATURE [App::DocumentObjectGroupPython] G4_Er  # scripted group (container) (typed FeaturePython)
  Dunit = g/cm3
  Dvalue = 9.066
  Group = -> [Er_element001]
  conduct = 2
  density = 1
  expand = 3
  formula = Er
  name = G4_Er
  specific = 4
FEATURE [App::DocumentObjectGroupPython] Tm_element001  label="Tm_element : 1"  # scripted group (container) (typed FeaturePython)
  n = 1
  ref = Tm_element
FEATURE [App::DocumentObjectGroupPython] G4_Tm  # scripted group (container) (typed FeaturePython)
  Dunit = g/cm3
  Dvalue = 9.321
  Group = -> [Tm_element001]
  conduct = 2
  density = 1
  expand = 3
  formula = Tm
  name = G4_Tm
  specific = 4
FEATURE [App::DocumentObjectGroupPython] Yb_element001  label="Yb_element : 1"  # scripted group (container) (typed FeaturePython)
  n = 1
  ref = Yb_element
FEATURE [App::DocumentObjectGroupPython] G4_Yb  # scripted group (container) (typed FeaturePython)
  Dunit = g/cm3
  Dvalue = 6.73
  Group = -> [Yb_element001]
  conduct = 2
  density = 1
  expand = 3
  formula = Yb
  name = G4_Yb
  specific = 4
FEATURE [App::DocumentObjectGroupPython] Lu_element001  label="Lu_element : 1"  # scripted group (container) (typed FeaturePython)
  n = 1
  ref = Lu_element
FEATURE [App::DocumentObjectGroupPython] G4_Lu  # scripted group (container) (typed FeaturePython)
  Dunit = g/cm3
  Dvalue = 9.84
  Group = -> [Lu_element001]
  conduct = 2
  density = 1
  expand = 3
  formula = Lu
  name = G4_Lu
  specific = 4
FEATURE [App::DocumentObjectGroupPython] Hf_element001  label="Hf_element : 1"  # scripted group (container) (typed FeaturePython)
  n = 1
  ref = Hf_element
FEATURE [App::DocumentObjectGroupPython] G4_Hf  # scripted group (container) (typed FeaturePython)
  Dunit = g/cm3
  Dvalue = 13.31
  Group = -> [Hf_element001]
  conduct = 2
  density = 1
  expand = 3
  formula = Hf
  name = G4_Hf
  specific = 4
FEATURE [App::DocumentObjectGroupPython] Ta_element001  label="Ta_element : 1"  # scripted group (container) (typed FeaturePython)
  n = 1
  ref = Ta_element
FEATURE [App::DocumentObjectGroupPython] G4_Ta  # scripted group (container) (typed FeaturePython)
  Dunit = g/cm3
  Dvalue = 16.654
  Group = -> [Ta_element001]
  conduct = 2
  density = 1
  expand = 3
  formula = Ta
  name = G4_Ta
  specific = 4
FEATURE [App::DocumentObjectGroupPython] W_element004  label="W_element : 004"  # scripted group (container) (typed FeaturePython)
  n = 1
  ref = W_element
FEATURE [App::DocumentObjectGroupPython] G4_W  # scripted group (container) (typed FeaturePython)
  Dunit = g/cm3
  Dvalue = 19.3
  Group = -> [W_element004]
  conduct = 2
  density = 1
  expand = 3
  formula = W
  name = G4_W
  specific = 4
FEATURE [App::DocumentObjectGroupPython] Re_element001  label="Re_element : 1"  # scripted group (container) (typed FeaturePython)
  n = 1
  ref = Re_element
FEATURE [App::DocumentObjectGroupPython] G4_Re  # scripted group (container) (typed FeaturePython)
  Dunit = g/cm3
  Dvalue = 21.02
  Group = -> [Re_element001]
  conduct = 2
  density = 1
  expand = 3
  formula = Re
  name = G4_Re
  specific = 4
FEATURE [App::DocumentObjectGroupPython] Os_element001  label="Os_element : 1"  # scripted group (container) (typed FeaturePython)
  n = 1
  ref = Os_element
FEATURE [App::DocumentObjectGroupPython] G4_Os  # scripted group (container) (typed FeaturePython)
  Dunit = g/cm3
  Dvalue = 22.57
  Group = -> [Os_element001]
  conduct = 2
  density = 1
  expand = 3
  formula = Os
  name = G4_Os
  specific = 4
FEATURE [App::DocumentObjectGroupPython] Ir_element001  label="Ir_element : 1"  # scripted group (container) (typed FeaturePython)
  n = 1
  ref = Ir_element
FEATURE [App::DocumentObjectGroupPython] G4_Ir  # scripted group (container) (typed FeaturePython)
  Dunit = g/cm3
  Dvalue = 22.42
  Group = -> [Ir_element001]
  conduct = 2
  density = 1
  expand = 3
  formula = Ir
  name = G4_Ir
  specific = 4
FEATURE [App::DocumentObjectGroupPython] Pt_element001  label="Pt_element : 1"  # scripted group (container) (typed FeaturePython)
  n = 1
  ref = Pt_element
FEATURE [App::DocumentObjectGroupPython] G4_Pt  # scripted group (container) (typed FeaturePython)
  Dunit = g/cm3
  Dvalue = 21.45
  Group = -> [Pt_element001]
  conduct = 2
  density = 1
  expand = 3
  formula = Pt
  name = G4_Pt
  specific = 4
FEATURE [App::DocumentObjectGroupPython] Au_element001  label="Au_element : 1"  # scripted group (container) (typed FeaturePython)
  n = 1
  ref = Au_element
FEATURE [App::DocumentObjectGroupPython] G4_Au  # scripted group (container) (typed FeaturePython)
  Dunit = g/cm3
  Dvalue = 19.32
  Group = -> [Au_element001]
  conduct = 2
  density = 1
  expand = 3
  formula = Au
  name = G4_Au
  specific = 4
FEATURE [App::DocumentObjectGroupPython] Hg_element002  label="Hg_element : 002"  # scripted group (container) (typed FeaturePython)
  n = 1
  ref = Hg_element
FEATURE [App::DocumentObjectGroupPython] G4_Hg  # scripted group (container) (typed FeaturePython)
  Dunit = g/cm3
  Dvalue = 13.546
  Group = -> [Hg_element002]
  conduct = 2
  density = 1
  expand = 3
  formula = Hg
  name = G4_Hg
  specific = 4
FEATURE [App::DocumentObjectGroupPython] Tl_element002  label="Tl_element : 002"  # scripted group (container) (typed FeaturePython)
  n = 1
  ref = Tl_element
FEATURE [App::DocumentObjectGroupPython] G4_Tl  # scripted group (container) (typed FeaturePython)
  Dunit = g/cm3
  Dvalue = 11.72
  Group = -> [Tl_element002]
  conduct = 2
  density = 1
  expand = 3
  formula = Tl
  name = G4_Tl
  specific = 4
FEATURE [App::DocumentObjectGroupPython] Pb_element003  label="Pb_element : 1"  # scripted group (container) (typed FeaturePython)
  n = 1
  ref = Pb_element
FEATURE [App::DocumentObjectGroupPython] G4_Pb  # scripted group (container) (typed FeaturePython)
  Dunit = g/cm3
  Dvalue = 11.35
  Group = -> [Pb_element003]
  conduct = 2
  density = 1
  expand = 3
  formula = Pb
  name = G4_Pb
  specific = 4
FEATURE [App::DocumentObjectGroupPython] Bi_element002  label="Bi_element : 1"  # scripted group (container) (typed FeaturePython)
  n = 1
  ref = Bi_element
FEATURE [App::DocumentObjectGroupPython] G4_Bi  # scripted group (container) (typed FeaturePython)
  Dunit = g/cm3
  Dvalue = 9.747
  Group = -> [Bi_element002]
  conduct = 2
  density = 1
  expand = 3
  formula = Bi
  name = G4_Bi
  specific = 4
FEATURE [App::DocumentObjectGroupPython] Po_element001  label="Po_element : 1"  # scripted group (container) (typed FeaturePython)
  n = 1
  ref = Po_element
FEATURE [App::DocumentObjectGroupPython] G4_Po  # scripted group (container) (typed FeaturePython)
  Dunit = g/cm3
  Dvalue = 9.32
  Group = -> [Po_element001]
  conduct = 2
  density = 1
  expand = 3
  formula = Po
  name = G4_Po
  specific = 4
FEATURE [App::DocumentObjectGroupPython] At_element001  label="At_element : 1"  # scripted group (container) (typed FeaturePython)
  n = 1
  ref = At_element
FEATURE [App::DocumentObjectGroupPython] G4_At  # scripted group (container) (typed FeaturePython)
  Dunit = g/cm3
  Dvalue = 9.32
  Group = -> [At_element001]
  conduct = 2
  density = 1
  expand = 3
  formula = At
  name = G4_At
  specific = 4
FEATURE [App::DocumentObjectGroupPython] Rn_element001  label="Rn_element : 1"  # scripted group (container) (typed FeaturePython)
  n = 1
  ref = Rn_element
FEATURE [App::DocumentObjectGroupPython] G4_Rn  # scripted group (container) (typed FeaturePython)
  Dunit = g/cm3
  Dvalue = 0.00900662
  Group = -> [Rn_element001]
  conduct = 2
  density = 1
  expand = 3
  formula = Rn
  name = G4_Rn
  specific = 4
FEATURE [App::DocumentObjectGroupPython] Fr_element001  label="Fr_element : 1"  # scripted group (container) (typed FeaturePython)
  n = 1
  ref = Fr_element
FEATURE [App::DocumentObjectGroupPython] G4_Fr  # scripted group (container) (typed FeaturePython)
  Dunit = g/cm3
  Dvalue = 1
  Group = -> [Fr_element001]
  conduct = 2
  density = 1
  expand = 3
  formula = Fr
  name = G4_Fr
  specific = 4
FEATURE [App::DocumentObjectGroupPython] Ra_element001  label="Ra_element : 1"  # scripted group (container) (typed FeaturePython)
  n = 1
  ref = Ra_element
FEATURE [App::DocumentObjectGroupPython] G4_Ra  # scripted group (container) (typed FeaturePython)
  Dunit = g/cm3
  Dvalue = 5
  Group = -> [Ra_element001]
  conduct = 2
  density = 1
  expand = 3
  formula = Ra
  name = G4_Ra
  specific = 4
FEATURE [App::DocumentObjectGroupPython] Ac_element001  label="Ac_element : 1"  # scripted group (container) (typed FeaturePython)
  n = 1
  ref = Ac_element
FEATURE [App::DocumentObjectGroupPython] G4_Ac  # scripted group (container) (typed FeaturePython)
  Dunit = g/cm3
  Dvalue = 10.07
  Group = -> [Ac_element001]
  conduct = 2
  density = 1
  expand = 3
  formula = Ac
  name = G4_Ac
  specific = 4
FEATURE [App::DocumentObjectGroupPython] Th_element001  label="Th_element : 1"  # scripted group (container) (typed FeaturePython)
  n = 1
  ref = Th_element
FEATURE [App::DocumentObjectGroupPython] G4_Th  # scripted group (container) (typed FeaturePython)
  Dunit = g/cm3
  Dvalue = 11.72
  Group = -> [Th_element001]
  conduct = 2
  density = 1
  expand = 3
  formula = Th
  name = G4_Th
  specific = 4
FEATURE [App::DocumentObjectGroupPython] Pa_element001  label="Pa_element : 1"  # scripted group (container) (typed FeaturePython)
  n = 1
  ref = Pa_element
FEATURE [App::DocumentObjectGroupPython] G4_Pa  # scripted group (container) (typed FeaturePython)
  Dunit = g/cm3
  Dvalue = 15.37
  Group = -> [Pa_element001]
  conduct = 2
  density = 1
  expand = 3
  formula = Pa
  name = G4_Pa
  specific = 4
FEATURE [App::DocumentObjectGroupPython] U_element004  label="U_element : 004"  # scripted group (container) (typed FeaturePython)
  n = 1
  ref = U_element
FEATURE [App::DocumentObjectGroupPython] G4_U  # scripted group (container) (typed FeaturePython)
  Dunit = g/cm3
  Dvalue = 18.95
  Group = -> [U_element004]
  conduct = 2
  density = 1
  expand = 3
  formula = U
  name = G4_U
  specific = 4
FEATURE [App::DocumentObjectGroupPython] Np_element001  label="Np_element : 1"  # scripted group (container) (typed FeaturePython)
  n = 1
  ref = Np_element
FEATURE [App::DocumentObjectGroupPython] G4_Np  # scripted group (container) (typed FeaturePython)
  Dunit = g/cm3
  Dvalue = 20.25
  Group = -> [Np_element001]
  conduct = 2
  density = 1
  expand = 3
  formula = Np
  name = G4_Np
  specific = 4
FEATURE [App::DocumentObjectGroupPython] Pu_element002  label="Pu_element : 002"  # scripted group (container) (typed FeaturePython)
  n = 1
  ref = Pu_element
FEATURE [App::DocumentObjectGroupPython] G4_Pu  # scripted group (container) (typed FeaturePython)
  Dunit = g/cm3
  Dvalue = 19.84
  Group = -> [Pu_element002]
  conduct = 2
  density = 1
  expand = 3
  formula = Pu
  name = G4_Pu
  specific = 4
FEATURE [App::DocumentObjectGroupPython] Am_element001  label="Am_element : 1"  # scripted group (container) (typed FeaturePython)
  n = 1
  ref = Am_element
FEATURE [App::DocumentObjectGroupPython] G4_Am  # scripted group (container) (typed FeaturePython)
  Dunit = g/cm3
  Dvalue = 13.67
  Group = -> [Am_element001]
  conduct = 2
  density = 1
  expand = 3
  formula = Am
  name = G4_Am
  specific = 4
FEATURE [App::DocumentObjectGroupPython] Cm_element001  label="Cm_element : 1"  # scripted group (container) (typed FeaturePython)
  n = 1
  ref = Cm_element
FEATURE [App::DocumentObjectGroupPython] G4_Cm  # scripted group (container) (typed FeaturePython)
  Dunit = g/cm3
  Dvalue = 13.51
  Group = -> [Cm_element001]
  conduct = 2
  density = 1
  expand = 3
  formula = Cm
  name = G4_Cm
  specific = 4
FEATURE [App::DocumentObjectGroupPython] Bk_element001  label="Bk_element : 1"  # scripted group (container) (typed FeaturePython)
  n = 1
  ref = Bk_element
FEATURE [App::DocumentObjectGroupPython] G4_Bk  # scripted group (container) (typed FeaturePython)
  Dunit = g/cm3
  Dvalue = 14
  Group = -> [Bk_element001]
  conduct = 2
  density = 1
  expand = 3
  formula = Bk
  name = G4_Bk
  specific = 4
FEATURE [App::DocumentObjectGroupPython] Cf_element001  label="Cf_element : 1"  # scripted group (container) (typed FeaturePython)
  n = 1
  ref = Cf_element
FEATURE [App::DocumentObjectGroupPython] G4_Cf  # scripted group (container) (typed FeaturePython)
  Dunit = g/cm3
  Dvalue = 10
  Group = -> [Cf_element001]
  conduct = 2
  density = 1
  expand = 3
  formula = Cf
  name = G4_Cf
  specific = 4
FEATURE [App::DocumentObjectGroupPython] Element  # scripted group (container) (typed FeaturePython)
  Group = -> [G4_H,G4_He,G4_Li,G4_Be,G4_B,G4_C,G4_N,G4_O,G4_F,G4_Ne,G4_Na,G4_Mg,G4_Al,G4_Si,G4_P,G4_S,G4_Cl,G4_Ar,G4_K,G4_Ca,G4_Sc,G4_Ti,G4_V,G4_Cr,G4_Mn,G4_Fe,G4_Co,G4_Ni,G4_Cu,G4_Zn,G4_Ga,G4_Ge,G4_As,G4_Se,G4_Br,G4_Kr,G4_Rb,G4_Sr,G4_Y,G4_Zr,G4_Nb,G4_Mo,G4_Tc,G4_Ru,G4_Rh,G4_Pd,G4_Ag,G4_Cd,G4_In,G4_Sn,G4_Sb,G4_Te,G4_I,G4_Xe,G4_Cs,G4_Ba,G4_La,G4_Ce,G4_Pr,G4_Nd,G4_Pm,G4_Sm,G4_Eu,G4_Gd,G4_Tb,G4_Dy,G4_Ho,G4_Er,+30 more]
FEATURE [App::DocumentObjectGroupPython] H_element114  label="H_element : 063"  # scripted group (container) (typed FeaturePython)
  n = 2
  ref = H_element
FEATURE [App::DocumentObjectGroupPython] G4_lH2  # scripted group (container) (typed FeaturePython)
  Dunit = g/cm3
  Dvalue = 0.0708
  Group = -> [H_element114]
  conduct = 2
  density = 1
  expand = 3
  formula = G4_lH2
  name = G4_lH2
  specific = 4
FEATURE [App::DocumentObjectGroupPython] N_element049  label="N_element : 022"  # scripted group (container) (typed FeaturePython)
  n = 2
  ref = N_element
FEATURE [App::DocumentObjectGroupPython] G4_lN2  # scripted group (container) (typed FeaturePython)
  Dunit = g/cm3
  Dvalue = 0.807
  Group = -> [N_element049]
  conduct = 2
  density = 1
  expand = 3
  formula = G4_lN2
  name = G4_lN2
  specific = 4
FEATURE [App::DocumentObjectGroupPython] O_element106  label="O_element : 060"  # scripted group (container) (typed FeaturePython)
  n = 2
  ref = O_element
FEATURE [App::DocumentObjectGroupPython] G4_lO2  # scripted group (container) (typed FeaturePython)
  Dunit = g/cm3
  Dvalue = 1.141
  Group = -> [O_element106]
  conduct = 2
  density = 1
  expand = 3
  formula = G4_lO2
  name = G4_lO2
  specific = 4
FEATURE [App::DocumentObjectGroupPython] Ar  label="Ar : 1"  # scripted group (container) (typed FeaturePython)
  n = 1
  ref = Ar
FEATURE [App::DocumentObjectGroupPython] G4_lAr  # scripted group (container) (typed FeaturePython)
  Dunit = g/cm3
  Dvalue = 1.396
  Group = -> [Ar]
  conduct = 2
  density = 1
  expand = 3
  formula = G4_lAr
  name = G4_lAr
  specific = 4
FEATURE [App::DocumentObjectGroupPython] Br  label="Br : 1"  # scripted group (container) (typed FeaturePython)
  n = 1
  ref = Br
FEATURE [App::DocumentObjectGroupPython] G4_lBr  # scripted group (container) (typed FeaturePython)
  Dunit = g/cm3
  Dvalue = 3.1028
  Group = -> [Br]
  conduct = 2
  density = 1
  expand = 3
  formula = G4_lBr
  name = G4_lBr
  specific = 4
FEATURE [App::DocumentObjectGroupPython] Kr  label="Kr : 1"  # scripted group (container) (typed FeaturePython)
  n = 1
  ref = Kr
FEATURE [App::DocumentObjectGroupPython] G4_lKr  # scripted group (container) (typed FeaturePython)
  Dunit = g/cm3
  Dvalue = 2.418
  Group = -> [Kr]
  conduct = 2
  density = 1
  expand = 3
  formula = G4_lKr
  name = G4_lKr
  specific = 4
FEATURE [App::DocumentObjectGroupPython] Xe  label="Xe : 1"  # scripted group (container) (typed FeaturePython)
  n = 1
  ref = Xe
FEATURE [App::DocumentObjectGroupPython] G4_lXe  # scripted group (container) (typed FeaturePython)
  Dunit = g/cm3
  Dvalue = 2.953
  Group = -> [Xe]
  conduct = 2
  density = 1
  expand = 3
  formula = G4_lXe
  name = G4_lXe
  specific = 4
FEATURE [App::DocumentObjectGroupPython] O_element107  label="O_element : 061"  # scripted group (container) (typed FeaturePython)
  n = 4
  ref = O_element
FEATURE [App::DocumentObjectGroupPython] Pb_element004  label="Pb_element : 002"  # scripted group (container) (typed FeaturePython)
  n = 1
  ref = Pb_element
FEATURE [App::DocumentObjectGroupPython] W_element005  label="W_element : 005"  # scripted group (container) (typed FeaturePython)
  n = 1
  ref = W_element
FEATURE [App::DocumentObjectGroupPython] G4_PbWO4  # scripted group (container) (typed FeaturePython)
  Dunit = g/cm3
  Dvalue = 8.28
  Group = -> [O_element107,Pb_element004,W_element005]
  conduct = 2
  density = 1
  expand = 3
  formula = G4_PbWO4
  name = G4_PbWO4
  specific = 4
FEATURE [App::DocumentObjectGroupPython] alactic  label="alactic : 1"  # scripted group (container) (typed FeaturePython)
  n = 1
  ref = alactic
FEATURE [App::DocumentObjectGroupPython] G4_Galactic  # scripted group (container) (typed FeaturePython)
  Dunit = g/cm3
  Dvalue = 0
  Group = -> [alactic]
  conduct = 2
  density = 1
  expand = 3
  formula = G4_Galactic
  name = G4_Galactic
  specific = 4
FEATURE [App::DocumentObjectGroupPython] RAPHITE_POROUS  label="RAPHITE_POROUS : 1"  # scripted group (container) (typed FeaturePython)
  n = 1
  ref = RAPHITE_POROUS
FEATURE [App::DocumentObjectGroupPython] G4_GRAPHITE_POROUS  # scripted group (container) (typed FeaturePython)
  Dunit = g/cm3
  Dvalue = 1.7
  Group = -> [RAPHITE_POROUS]
  conduct = 2
  density = 1
  expand = 3
  formula = G4_GRAPHITE_POROUS
  name = G4_GRAPHITE_POROUS
  specific = 4
FEATURE [App::DocumentObjectGroupPython] H_element115  label="H_element : 0.150"  # scripted group (container) (typed FeaturePython)
  n = 0.080538
FEATURE [App::DocumentObjectGroupPython] C_element125  label="C_element : 0.600"  # scripted group (container) (typed FeaturePython)
  n = 0.599848
FEATURE [App::DocumentObjectGroupPython] O_element108  label="O_element : 0.320"  # scripted group (container) (typed FeaturePython)
  n = 0.319614
FEATURE [App::DocumentObjectGroupPython] G4_LUCITE  # scripted group (container) (typed FeaturePython)
  Dunit = g/cm3
  Dvalue = 1.19
  Group = -> [H_element115,C_element125,O_element108]
  conduct = 2
  density = 1
  expand = 3
  formula = G4_LUCITE
  name = G4_LUCITE
  specific = 4
FEATURE [App::DocumentObjectGroupPython] Cu_element002  label="Cu_element : 62"  # scripted group (container) (typed FeaturePython)
  n = 62
  ref = Cu_element
FEATURE [App::DocumentObjectGroupPython] Zn_element002  label="Zn_element : 35"  # scripted group (container) (typed FeaturePython)
  n = 35
  ref = Zn_element
FEATURE [App::DocumentObjectGroupPython] Pb_element005  label="Pb_element : 3"  # scripted group (container) (typed FeaturePython)
  n = 3
  ref = Pb_element
FEATURE [App::DocumentObjectGroupPython] G4_BRASS  # scripted group (container) (typed FeaturePython)
  Dunit = g/cm3
  Dvalue = 8.52
  Group = -> [Cu_element002,Zn_element002,Pb_element005]
  conduct = 2
  density = 1
  expand = 3
  formula = G4_BRASS
  name = G4_BRASS
  specific = 4
FEATURE [App::DocumentObjectGroupPython] Cu_element003  label="Cu_element : 89"  # scripted group (container) (typed FeaturePython)
  n = 89
  ref = Cu_element
FEATURE [App::DocumentObjectGroupPython] Zn_element003  label="Zn_element : 9"  # scripted group (container) (typed FeaturePython)
  n = 9
  ref = Zn_element
FEATURE [App::DocumentObjectGroupPython] Pb_element006  label="Pb_element : 2"  # scripted group (container) (typed FeaturePython)
  n = 2
  ref = Pb_element
FEATURE [App::DocumentObjectGroupPython] G4_BRONZE  # scripted group (container) (typed FeaturePython)
  Dunit = g/cm3
  Dvalue = 8.82
  Group = -> [Cu_element003,Zn_element003,Pb_element006]
  conduct = 2
  density = 1
  expand = 3
  formula = G4_BRONZE
  name = G4_BRONZE
  specific = 4
FEATURE [App::DocumentObjectGroupPython] Fe_element008  label="Fe_element : 74"  # scripted group (container) (typed FeaturePython)
  n = 74
  ref = Fe_element
FEATURE [App::DocumentObjectGroupPython] Cr_element002  label="Cr_element : 18"  # scripted group (container) (typed FeaturePython)
  n = 18
  ref = Cr_element
FEATURE [App::DocumentObjectGroupPython] Ni_element002  label="Ni_element : 8"  # scripted group (container) (typed FeaturePython)
  n = 8
  ref = Ni_element
FEATURE [App::DocumentObjectGroupPython] G4_STAINLESS_STEEL  label="G4_STAINLESS-STEEL"  # scripted group (container) (typed FeaturePython)
  Dunit = g/cm3
  Dvalue = 8
  Group = -> [Fe_element008,Cr_element002,Ni_element002]
  conduct = 2
  density = 1
  expand = 3
  formula = G4_STAINLESS-STEEL
  name = G4_STAINLESS-STEEL
  specific = 4
FEATURE [App::DocumentObjectGroupPython] H_element116  label="H_element : 064"  # scripted group (container) (typed FeaturePython)
  n = 18
  ref = H_element
FEATURE [App::DocumentObjectGroupPython] C_element126  label="C_element : 071"  # scripted group (container) (typed FeaturePython)
  n = 12
  ref = C_element
FEATURE [App::DocumentObjectGroupPython] O_element109  label="O_element : 062"  # scripted group (container) (typed FeaturePython)
  n = 7
  ref = O_element
FEATURE [App::DocumentObjectGroupPython] G4_CR39  # scripted group (container) (typed FeaturePython)
  Dunit = g/cm3
  Dvalue = 1.32
  Group = -> [H_element116,C_element126,O_element109]
  conduct = 2
  density = 1
  expand = 3
  formula = G4_CR39
  name = G4_CR39
  specific = 4
FEATURE [App::DocumentObjectGroupPython] H_element117  label="H_element : 38"  # scripted group (container) (typed FeaturePython)
  n = 38
  ref = H_element
FEATURE [App::DocumentObjectGroupPython] C_element127  label="C_element : 072"  # scripted group (container) (typed FeaturePython)
  n = 18
  ref = C_element
FEATURE [App::DocumentObjectGroupPython] O_element110  label="O_element : 063"  # scripted group (container) (typed FeaturePython)
  n = 1
  ref = O_element
FEATURE [App::DocumentObjectGroupPython] G4_OCTADECANOL  # scripted group (container) (typed FeaturePython)
  Dunit = g/cm3
  Dvalue = 0.812
  Group = -> [H_element117,C_element127,O_element110]
  conduct = 2
  density = 1
  expand = 3
  formula = G4_OCTADECANOL
  name = G4_OCTADECANOL
  specific = 4
FEATURE [App::DocumentObjectGroupPython] HEP  # scripted group (container) (typed FeaturePython)
  Group = -> [G4_lH2,G4_lN2,G4_lO2,G4_lAr,G4_lBr,G4_lKr,G4_lXe,G4_PbWO4,G4_Galactic,G4_GRAPHITE_POROUS,G4_LUCITE,G4_BRASS,G4_BRONZE,G4_STAINLESS_STEEL,G4_CR39,G4_OCTADECANOL]
FEATURE [App::DocumentObjectGroupPython] C_element128  label="C_element : 073"  # scripted group (container) (typed FeaturePython)
  n = 14
  ref = C_element
FEATURE [App::DocumentObjectGroupPython] H_element118  label="H_element : 065"  # scripted group (container) (typed FeaturePython)
  n = 10
  ref = H_element
FEATURE [App::DocumentObjectGroupPython] O_element111  label="O_element : 064"  # scripted group (container) (typed FeaturePython)
  n = 2
  ref = O_element
FEATURE [App::DocumentObjectGroupPython] N_element050  label="N_element : 023"  # scripted group (container) (typed FeaturePython)
  n = 2
  ref = N_element
FEATURE [App::DocumentObjectGroupPython] G4_KEVLAR  # scripted group (container) (typed FeaturePython)
  Dunit = g/cm3
  Dvalue = 1.44
  Group = -> [C_element128,H_element118,O_element111,N_element050]
  conduct = 2
  density = 1
  expand = 3
  formula = G4_KEVLAR
  name = G4_KEVLAR
  specific = 4
FEATURE [App::DocumentObjectGroupPython] C_element129  label="C_element : 074"  # scripted group (container) (typed FeaturePython)
  n = 10
  ref = C_element
FEATURE [App::DocumentObjectGroupPython] H_element119  label="H_element : 066"  # scripted group (container) (typed FeaturePython)
  n = 8
  ref = H_element
FEATURE [App::DocumentObjectGroupPython] O_element112  label="O_element : 065"  # scripted group (container) (typed FeaturePython)
  n = 4
  ref = O_element
FEATURE [App::DocumentObjectGroupPython] G4_DACRON  # scripted group (container) (typed FeaturePython)
  Dunit = g/cm3
  Dvalue = 1.4
  Group = -> [C_element129,H_element119,O_element112]
  conduct = 2
  density = 1
  expand = 3
  formula = G4_DACRON
  name = G4_DACRON
  specific = 4
FEATURE [App::DocumentObjectGroupPython] C_element130  label="C_element : 075"  # scripted group (container) (typed FeaturePython)
  n = 4
  ref = C_element
FEATURE [App::DocumentObjectGroupPython] H_element120  label="H_element : 067"  # scripted group (container) (typed FeaturePython)
  n = 5
  ref = H_element
FEATURE [App::DocumentObjectGroupPython] Cl_element030  label="Cl_element : 016"  # scripted group (container) (typed FeaturePython)
  n = 1
  ref = Cl_element
FEATURE [App::DocumentObjectGroupPython] G4_NEOPRENE  # scripted group (container) (typed FeaturePython)
  Dunit = g/cm3
  Dvalue = 1.23
  Group = -> [C_element130,H_element120,Cl_element030]
  conduct = 2
  density = 1
  expand = 3
  formula = G4_NEOPRENE
  name = G4_NEOPRENE
  specific = 4
FEATURE [App::DocumentObjectGroupPython] Space  # scripted group (container) (typed FeaturePython)
  Group = -> [G4_KEVLAR,G4_DACRON,G4_NEOPRENE]
FEATURE [App::DocumentObjectGroupPython] H_element121  label="H_element : 068"  # scripted group (container) (typed FeaturePython)
  n = 5
  ref = H_element
FEATURE [App::DocumentObjectGroupPython] C_element131  label="C_element : 076"  # scripted group (container) (typed FeaturePython)
  n = 4
  ref = C_element
FEATURE [App::DocumentObjectGroupPython] N_element051  label="N_element : 3"  # scripted group (container) (typed FeaturePython)
  n = 3
  ref = N_element
FEATURE [App::DocumentObjectGroupPython] O_element113  label="O_element : 066"  # scripted group (container) (typed FeaturePython)
  n = 1
  ref = O_element
FEATURE [App::DocumentObjectGroupPython] G4_CYTOSINE  # scripted group (container) (typed FeaturePython)
  Dunit = g/cm3
  Dvalue = 1.55
  Group = -> [H_element121,C_element131,N_element051,O_element113]
  conduct = 2
  density = 1
  expand = 3
  formula = G4_CYTOSINE
  name = G4_CYTOSINE
  specific = 4
FEATURE [App::DocumentObjectGroupPython] H_element122  label="H_element : 069"  # scripted group (container) (typed FeaturePython)
  n = 6
  ref = H_element
FEATURE [App::DocumentObjectGroupPython] C_element132  label="C_element : 077"  # scripted group (container) (typed FeaturePython)
  n = 5
  ref = C_element
FEATURE [App::DocumentObjectGroupPython] N_element052  label="N_element : 024"  # scripted group (container) (typed FeaturePython)
  n = 2
  ref = N_element
FEATURE [App::DocumentObjectGroupPython] O_element114  label="O_element : 067"  # scripted group (container) (typed FeaturePython)
  n = 2
  ref = O_element
FEATURE [App::DocumentObjectGroupPython] G4_THYMINE  # scripted group (container) (typed FeaturePython)
  Dunit = g/cm3
  Dvalue = 1.23
  Group = -> [H_element122,C_element132,N_element052,O_element114]
  conduct = 2
  density = 1
  expand = 3
  formula = G4_THYMINE
  name = G4_THYMINE
  specific = 4
FEATURE [App::DocumentObjectGroupPython] H_element123  label="H_element : 070"  # scripted group (container) (typed FeaturePython)
  n = 4
  ref = H_element
FEATURE [App::DocumentObjectGroupPython] C_element133  label="C_element : 078"  # scripted group (container) (typed FeaturePython)
  n = 4
  ref = C_element
FEATURE [App::DocumentObjectGroupPython] N_element053  label="N_element : 025"  # scripted group (container) (typed FeaturePython)
  n = 2
  ref = N_element
FEATURE [App::DocumentObjectGroupPython] O_element115  label="O_element : 068"  # scripted group (container) (typed FeaturePython)
  n = 2
  ref = O_element
FEATURE [App::DocumentObjectGroupPython] G4_URACIL  # scripted group (container) (typed FeaturePython)
  Dunit = g/cm3
  Dvalue = 1.32
  Group = -> [H_element123,C_element133,N_element053,O_element115]
  conduct = 2
  density = 1
  expand = 3
  formula = G4_URACIL
  name = G4_URACIL
  specific = 4
FEATURE [App::DocumentObjectGroupPython] H_element124  label="H_element : 071"  # scripted group (container) (typed FeaturePython)
  n = 4
  ref = H_element
FEATURE [App::DocumentObjectGroupPython] C_element134  label="C_element : 079"  # scripted group (container) (typed FeaturePython)
  n = 5
  ref = C_element
FEATURE [App::DocumentObjectGroupPython] N_element054  label="N_element : 026"  # scripted group (container) (typed FeaturePython)
  n = 5
  ref = N_element
FEATURE [App::DocumentObjectGroupPython] G4_DNA_ADENINE  # scripted group (container) (typed FeaturePython)
  Dunit = g/cm3
  Dvalue = 1
  Group = -> [H_element124,C_element134,N_element054]
  conduct = 2
  density = 1
  expand = 3
  formula = G4_DNA_ADENINE
  name = G4_DNA_ADENINE
  specific = 4
FEATURE [App::DocumentObjectGroupPython] H_element125  label="H_element : 072"  # scripted group (container) (typed FeaturePython)
  n = 4
  ref = H_element
FEATURE [App::DocumentObjectGroupPython] C_element135  label="C_element : 080"  # scripted group (container) (typed FeaturePython)
  n = 5
  ref = C_element
FEATURE [App::DocumentObjectGroupPython] N_element055  label="N_element : 027"  # scripted group (container) (typed FeaturePython)
  n = 5
  ref = N_element
FEATURE [App::DocumentObjectGroupPython] O_element116  label="O_element : 069"  # scripted group (container) (typed FeaturePython)
  n = 1
  ref = O_element
FEATURE [App::DocumentObjectGroupPython] G4_DNA_GUANINE  # scripted group (container) (typed FeaturePython)
  Dunit = g/cm3
  Dvalue = 1
  Group = -> [H_element125,C_element135,N_element055,O_element116]
  conduct = 2
  density = 1
  expand = 3
  formula = G4_DNA_GUANINE
  name = G4_DNA_GUANINE
  specific = 4
FEATURE [App::DocumentObjectGroupPython] H_element126  label="H_element : 073"  # scripted group (container) (typed FeaturePython)
  n = 4
  ref = H_element
FEATURE [App::DocumentObjectGroupPython] C_element136  label="C_element : 081"  # scripted group (container) (typed FeaturePython)
  n = 4
  ref = C_element
FEATURE [App::DocumentObjectGroupPython] N_element056  label="N_element : 028"  # scripted group (container) (typed FeaturePython)
  n = 3
  ref = N_element
FEATURE [App::DocumentObjectGroupPython] O_element117  label="O_element : 070"  # scripted group (container) (typed FeaturePython)
  n = 1
  ref = O_element
FEATURE [App::DocumentObjectGroupPython] G4_DNA_CYTOSINE  # scripted group (container) (typed FeaturePython)
  Dunit = g/cm3
  Dvalue = 1
  Group = -> [H_element126,C_element136,N_element056,O_element117]
  conduct = 2
  density = 1
  expand = 3
  formula = G4_DNA_CYTOSINE
  name = G4_DNA_CYTOSINE
  specific = 4
FEATURE [App::DocumentObjectGroupPython] H_element127  label="H_element : 074"  # scripted group (container) (typed FeaturePython)
  n = 5
  ref = H_element
FEATURE [App::DocumentObjectGroupPython] C_element137  label="C_element : 082"  # scripted group (container) (typed FeaturePython)
  n = 5
  ref = C_element
FEATURE [App::DocumentObjectGroupPython] N_element057  label="N_element : 029"  # scripted group (container) (typed FeaturePython)
  n = 2
  ref = N_element
FEATURE [App::DocumentObjectGroupPython] O_element118  label="O_element : 071"  # scripted group (container) (typed FeaturePython)
  n = 2
  ref = O_element
FEATURE [App::DocumentObjectGroupPython] G4_DNA_THYMINE  # scripted group (container) (typed FeaturePython)
  Dunit = g/cm3
  Dvalue = 1
  Group = -> [H_element127,C_element137,N_element057,O_element118]
  conduct = 2
  density = 1
  expand = 3
  formula = G4_DNA_THYMINE
  name = G4_DNA_THYMINE
  specific = 4
FEATURE [App::DocumentObjectGroupPython] H_element128  label="H_element : 075"  # scripted group (container) (typed FeaturePython)
  n = 3
  ref = H_element
FEATURE [App::DocumentObjectGroupPython] C_element138  label="C_element : 083"  # scripted group (container) (typed FeaturePython)
  n = 4
  ref = C_element
FEATURE [App::DocumentObjectGroupPython] N_element058  label="N_element : 030"  # scripted group (container) (typed FeaturePython)
  n = 2
  ref = N_element
FEATURE [App::DocumentObjectGroupPython] O_element119  label="O_element : 072"  # scripted group (container) (typed FeaturePython)
  n = 2
  ref = O_element
FEATURE [App::DocumentObjectGroupPython] G4_DNA_URACIL  # scripted group (container) (typed FeaturePython)
  Dunit = g/cm3
  Dvalue = 1
  Group = -> [H_element128,C_element138,N_element058,O_element119]
  conduct = 2
  density = 1
  expand = 3
  formula = G4_DNA_URACIL
  name = G4_DNA_URACIL
  specific = 4
FEATURE [App::DocumentObjectGroupPython] H_element129  label="H_element : 076"  # scripted group (container) (typed FeaturePython)
  n = 10
  ref = H_element
FEATURE [App::DocumentObjectGroupPython] C_element139  label="C_element : 084"  # scripted group (container) (typed FeaturePython)
  n = 10
  ref = C_element
FEATURE [App::DocumentObjectGroupPython] N_element059  label="N_element : 031"  # scripted group (container) (typed FeaturePython)
  n = 5
  ref = N_element
FEATURE [App::DocumentObjectGroupPython] O_element120  label="O_element : 073"  # scripted group (container) (typed FeaturePython)
  n = 4
  ref = O_element
FEATURE [App::DocumentObjectGroupPython] G4_DNA_ADENOSINE  # scripted group (container) (typed FeaturePython)
  Dunit = g/cm3
  Dvalue = 1
  Group = -> [H_element129,C_element139,N_element059,O_element120]
  conduct = 2
  density = 1
  expand = 3
  formula = G4_DNA_ADENOSINE
  name = G4_DNA_ADENOSINE
  specific = 4
FEATURE [App::DocumentObjectGroupPython] H_element130  label="H_element : 077"  # scripted group (container) (typed FeaturePython)
  n = 10
  ref = H_element
FEATURE [App::DocumentObjectGroupPython] C_element140  label="C_element : 085"  # scripted group (container) (typed FeaturePython)
  n = 10
  ref = C_element
FEATURE [App::DocumentObjectGroupPython] N_element060  label="N_element : 032"  # scripted group (container) (typed FeaturePython)
  n = 5
  ref = N_element
FEATURE [App::DocumentObjectGroupPython] O_element121  label="O_element : 074"  # scripted group (container) (typed FeaturePython)
  n = 5
  ref = O_element
FEATURE [App::DocumentObjectGroupPython] G4_DNA_GUANOSINE  # scripted group (container) (typed FeaturePython)
  Dunit = g/cm3
  Dvalue = 1
  Group = -> [H_element130,C_element140,N_element060,O_element121]
  conduct = 2
  density = 1
  expand = 3
  formula = G4_DNA_GUANOSINE
  name = G4_DNA_GUANOSINE
  specific = 4
FEATURE [App::DocumentObjectGroupPython] H_element131  label="H_element : 078"  # scripted group (container) (typed FeaturePython)
  n = 10
  ref = H_element
FEATURE [App::DocumentObjectGroupPython] C_element141  label="C_element : 086"  # scripted group (container) (typed FeaturePython)
  n = 9
  ref = C_element
FEATURE [App::DocumentObjectGroupPython] N_element061  label="N_element : 033"  # scripted group (container) (typed FeaturePython)
  n = 3
  ref = N_element
FEATURE [App::DocumentObjectGroupPython] O_element122  label="O_element : 075"  # scripted group (container) (typed FeaturePython)
  n = 5
  ref = O_element
FEATURE [App::DocumentObjectGroupPython] G4_DNA_CYTIDINE  # scripted group (container) (typed FeaturePython)
  Dunit = g/cm3
  Dvalue = 1
  Group = -> [H_element131,C_element141,N_element061,O_element122]
  conduct = 2
  density = 1
  expand = 3
  formula = G4_DNA_CYTIDINE
  name = G4_DNA_CYTIDINE
  specific = 4
FEATURE [App::DocumentObjectGroupPython] H_element132  label="H_element : 079"  # scripted group (container) (typed FeaturePython)
  n = 9
  ref = H_element
FEATURE [App::DocumentObjectGroupPython] C_element142  label="C_element : 087"  # scripted group (container) (typed FeaturePython)
  n = 9
  ref = C_element
FEATURE [App::DocumentObjectGroupPython] N_element062  label="N_element : 034"  # scripted group (container) (typed FeaturePython)
  n = 2
  ref = N_element
FEATURE [App::DocumentObjectGroupPython] O_element123  label="O_element : 076"  # scripted group (container) (typed FeaturePython)
  n = 6
  ref = O_element
FEATURE [App::DocumentObjectGroupPython] G4_DNA_URIDINE  # scripted group (container) (typed FeaturePython)
  Dunit = g/cm3
  Dvalue = 1
  Group = -> [H_element132,C_element142,N_element062,O_element123]
  conduct = 2
  density = 1
  expand = 3
  formula = G4_DNA_URIDINE
  name = G4_DNA_URIDINE
  specific = 4
FEATURE [App::DocumentObjectGroupPython] H_element133  label="H_element : 080"  # scripted group (container) (typed FeaturePython)
  n = 11
  ref = H_element
FEATURE [App::DocumentObjectGroupPython] C_element143  label="C_element : 088"  # scripted group (container) (typed FeaturePython)
  n = 10
  ref = C_element
FEATURE [App::DocumentObjectGroupPython] N_element063  label="N_element : 035"  # scripted group (container) (typed FeaturePython)
  n = 2
  ref = N_element
FEATURE [App::DocumentObjectGroupPython] O_element124  label="O_element : 077"  # scripted group (container) (typed FeaturePython)
  n = 6
  ref = O_element
FEATURE [App::DocumentObjectGroupPython] G4_DNA_METHYLURIDINE  # scripted group (container) (typed FeaturePython)
  Dunit = g/cm3
  Dvalue = 1
  Group = -> [H_element133,C_element143,N_element063,O_element124]
  conduct = 2
  density = 1
  expand = 3
  formula = G4_DNA_METHYLURIDINE
  name = G4_DNA_METHYLURIDINE
  specific = 4
FEATURE [App::DocumentObjectGroupPython] P_element014  label="P_element : 003"  # scripted group (container) (typed FeaturePython)
  n = 1
  ref = P_element
FEATURE [App::DocumentObjectGroupPython] O_element125  label="O_element : 078"  # scripted group (container) (typed FeaturePython)
  n = 3
  ref = O_element
FEATURE [App::DocumentObjectGroupPython] G4_DNA_MONOPHOSPHATE  # scripted group (container) (typed FeaturePython)
  Dunit = g/cm3
  Dvalue = 1
  Group = -> [P_element014,O_element125]
  conduct = 2
  density = 1
  expand = 3
  formula = G4_DNA_MONOPHOSPHATE
  name = G4_DNA_MONOPHOSPHATE
  specific = 4
FEATURE [App::DocumentObjectGroupPython] H_element134  label="H_element : 081"  # scripted group (container) (typed FeaturePython)
  n = 10
  ref = H_element
FEATURE [App::DocumentObjectGroupPython] C_element144  label="C_element : 089"  # scripted group (container) (typed FeaturePython)
  n = 10
  ref = C_element
FEATURE [App::DocumentObjectGroupPython] N_element064  label="N_element : 036"  # scripted group (container) (typed FeaturePython)
  n = 5
  ref = N_element
FEATURE [App::DocumentObjectGroupPython] O_element126  label="O_element : 079"  # scripted group (container) (typed FeaturePython)
  n = 7
  ref = O_element
FEATURE [App::DocumentObjectGroupPython] P_element015  label="P_element : 004"  # scripted group (container) (typed FeaturePython)
  n = 1
  ref = P_element
FEATURE [App::DocumentObjectGroupPython] G4_DNA_A  # scripted group (container) (typed FeaturePython)
  Dunit = g/cm3
  Dvalue = 1
  Group = -> [H_element134,C_element144,N_element064,O_element126,P_element015]
  conduct = 2
  density = 1
  expand = 3
  formula = G4_DNA_A
  name = G4_DNA_A
  specific = 4
FEATURE [App::DocumentObjectGroupPython] H_element135  label="H_element : 082"  # scripted group (container) (typed FeaturePython)
  n = 10
  ref = H_element
FEATURE [App::DocumentObjectGroupPython] C_element145  label="C_element : 090"  # scripted group (container) (typed FeaturePython)
  n = 10
  ref = C_element
FEATURE [App::DocumentObjectGroupPython] N_element065  label="N_element : 037"  # scripted group (container) (typed FeaturePython)
  n = 5
  ref = N_element
FEATURE [App::DocumentObjectGroupPython] O_element127  label="O_element : 8"  # scripted group (container) (typed FeaturePython)
  n = 8
  ref = O_element
FEATURE [App::DocumentObjectGroupPython] P_element016  label="P_element : 005"  # scripted group (container) (typed FeaturePython)
  n = 1
  ref = P_element
FEATURE [App::DocumentObjectGroupPython] G4_DNA_G  # scripted group (container) (typed FeaturePython)
  Dunit = g/cm3
  Dvalue = 1
  Group = -> [H_element135,C_element145,N_element065,O_element127,P_element016]
  conduct = 2
  density = 1
  expand = 3
  formula = G4_DNA_G
  name = G4_DNA_G
  specific = 4
FEATURE [App::DocumentObjectGroupPython] H_element136  label="H_element : 083"  # scripted group (container) (typed FeaturePython)
  n = 10
  ref = H_element
FEATURE [App::DocumentObjectGroupPython] C_element146  label="C_element : 091"  # scripted group (container) (typed FeaturePython)
  n = 9
  ref = C_element
FEATURE [App::DocumentObjectGroupPython] N_element066  label="N_element : 038"  # scripted group (container) (typed FeaturePython)
  n = 3
  ref = N_element
FEATURE [App::DocumentObjectGroupPython] O_element128  label="O_element : 080"  # scripted group (container) (typed FeaturePython)
  n = 8
  ref = O_element
FEATURE [App::DocumentObjectGroupPython] P_element017  label="P_element : 006"  # scripted group (container) (typed FeaturePython)
  n = 1
  ref = P_element
FEATURE [App::DocumentObjectGroupPython] G4_DNA_C  # scripted group (container) (typed FeaturePython)
  Dunit = g/cm3
  Dvalue = 1
  Group = -> [H_element136,C_element146,N_element066,O_element128,P_element017]
  conduct = 2
  density = 1
  expand = 3
  formula = G4_DNA_C
  name = G4_DNA_C
  specific = 4
FEATURE [App::DocumentObjectGroupPython] H_element137  label="H_element : 084"  # scripted group (container) (typed FeaturePython)
  n = 9
  ref = H_element
FEATURE [App::DocumentObjectGroupPython] C_element147  label="C_element : 092"  # scripted group (container) (typed FeaturePython)
  n = 9
  ref = C_element
FEATURE [App::DocumentObjectGroupPython] N_element067  label="N_element : 039"  # scripted group (container) (typed FeaturePython)
  n = 2
  ref = N_element
FEATURE [App::DocumentObjectGroupPython] O_element129  label="O_element : 9"  # scripted group (container) (typed FeaturePython)
  n = 9
  ref = O_element
FEATURE [App::DocumentObjectGroupPython] P_element018  label="P_element : 007"  # scripted group (container) (typed FeaturePython)
  n = 1
  ref = P_element
FEATURE [App::DocumentObjectGroupPython] G4_DNA_U  # scripted group (container) (typed FeaturePython)
  Dunit = g/cm3
  Dvalue = 1
  Group = -> [H_element137,C_element147,N_element067,O_element129,P_element018]
  conduct = 2
  density = 1
  expand = 3
  formula = G4_DNA_U
  name = G4_DNA_U
  specific = 4
FEATURE [App::DocumentObjectGroupPython] H_element138  label="H_element : 085"  # scripted group (container) (typed FeaturePython)
  n = 11
  ref = H_element
FEATURE [App::DocumentObjectGroupPython] C_element148  label="C_element : 093"  # scripted group (container) (typed FeaturePython)
  n = 10
  ref = C_element
FEATURE [App::DocumentObjectGroupPython] N_element068  label="N_element : 040"  # scripted group (container) (typed FeaturePython)
  n = 2
  ref = N_element
FEATURE [App::DocumentObjectGroupPython] O_element130  label="O_element : 081"  # scripted group (container) (typed FeaturePython)
  n = 9
  ref = O_element
FEATURE [App::DocumentObjectGroupPython] P_element019  label="P_element : 008"  # scripted group (container) (typed FeaturePython)
  n = 1
  ref = P_element
FEATURE [App::DocumentObjectGroupPython] G4_DNA_MU  # scripted group (container) (typed FeaturePython)
  Dunit = g/cm3
  Dvalue = 1
  Group = -> [H_element138,C_element148,N_element068,O_element130,P_element019]
  conduct = 2
  density = 1
  expand = 3
  formula = G4_DNA_MU
  name = G4_DNA_MU
  specific = 4
FEATURE [App::DocumentObjectGroupPython] BioChemical  # scripted group (container) (typed FeaturePython)
  Group = -> [G4_CYTOSINE,G4_THYMINE,G4_URACIL,G4_DNA_ADENINE,G4_DNA_GUANINE,G4_DNA_CYTOSINE,G4_DNA_THYMINE,G4_DNA_URACIL,G4_DNA_ADENOSINE,G4_DNA_GUANOSINE,G4_DNA_CYTIDINE,G4_DNA_URIDINE,G4_DNA_METHYLURIDINE,G4_DNA_MONOPHOSPHATE,G4_DNA_A,G4_DNA_G,G4_DNA_C,G4_DNA_U,G4_DNA_MU]
FEATURE [App::DocumentObjectGroupPython] G4Materials  # scripted group (container) (typed FeaturePython)
  Group = -> [NIST,Element,HEP,Space,BioChemical]
  version = 1
FEATURE [App::DocumentObjectGroupPython] Geant4  # scripted group (container) (typed FeaturePython)
  Group = -> [G4Isotopes,G4Elements,G4Materials]
FEATURE [App::DocumentObjectGroupPython] Materials  # scripted group (container) (typed FeaturePython)
  Group = -> [Geant4]
FEATURE [Part::FeaturePython] GDMLBox_WorldBox  # WARN: FeaturePython — macro-defined, semantics opaque (R4)
  lunit = 2
  material = 5
  x = 273
  y = 273
  z = 130
FEATURE [Part::FeaturePython] GDMLBox_Box  # WARN: FeaturePython — macro-defined, semantics opaque (R4)
  Placement = pos=(20,0,0) rot=(0,0,1;0rad)
  lunit = 2
  material = 0
  x = 10
  y = 10
  z = 10
FEATURE [Part::FeaturePython] GDMLTube  # WARN: FeaturePython — macro-defined, semantics opaque (R4)
  Placement = pos=(17,-4,0) rot=(0,0,1;0rad)
  aunit = 1
  deltaphi = 90
  lunit = 2
  material = 0
  rmax = 7
  rmin = 5
  startphi = 0
  z = 7
FEATURE [App::Part] LV_Tube
  Group = -> [GDMLTube]
  Origin = -> Origin003
  SkinSurface = 0
FEATURE [App::Part] LV_Box
  Group = -> [GDMLBox_Box,LV_Tube]
  Origin = -> Origin002
  Placement = pos=(0,0,0) rot=(0,0,1;-0.523599rad)
FEATURE [Part::FeaturePython] Array  # Draft array (typed FeaturePython)
  AlwaysSyncPlacement = false
  Angle = 180
  ArrayType = 1
  Axis = (0,0,1)
  Base = -> LV_Box
  Center = (0,0,0)
  Count = 5
  ExpandArray = false
  Fuse = false
  IntervalAxis = (0,0,0)
  IntervalX = (100,0,0)
  IntervalY = (0,100,0)
  IntervalZ = (0,0,100)
  NumberCircles = 3
  NumberPolar = 5
  NumberX = 2
  NumberY = 2
  NumberZ = 1
  Placement = pos=(-20,-20,0) rot=(0,0,1;0rad)
  PlacementList = 5 placements: [(0,0,0),(0,0,0),(0,0,0),(0,0,0),(0,0,0)]
  RadialDistance = 50
  ScaleList = (5) [(1,1,1),(1,1,1),(1,1,1),(1,1,1),(1,1,1)]
  Symmetry = 1
  TangentialDistance = 25
FEATURE [App::Part] Part  label="experiment"
  Group = -> [LV_Box,Array]
  Origin = -> Origin001
FEATURE [Part::Sphere] Sphere
  Angle1 = -90
  Angle2 = 90
  Angle3 = 360
  AttacherType = Attacher::AttachEngine3D
  Placement = pos=(-20,-20,0) rot=(0,0,1;0rad)
  Radius = 1
FEATURE [App::Part] Part001
  Group = -> [Sphere]
  Origin = -> Origin004
FEATURE [App::Part] worldVOL
  Group = -> [GDMLBox_WorldBox,Part,Part001]
  Origin = -> Origin
